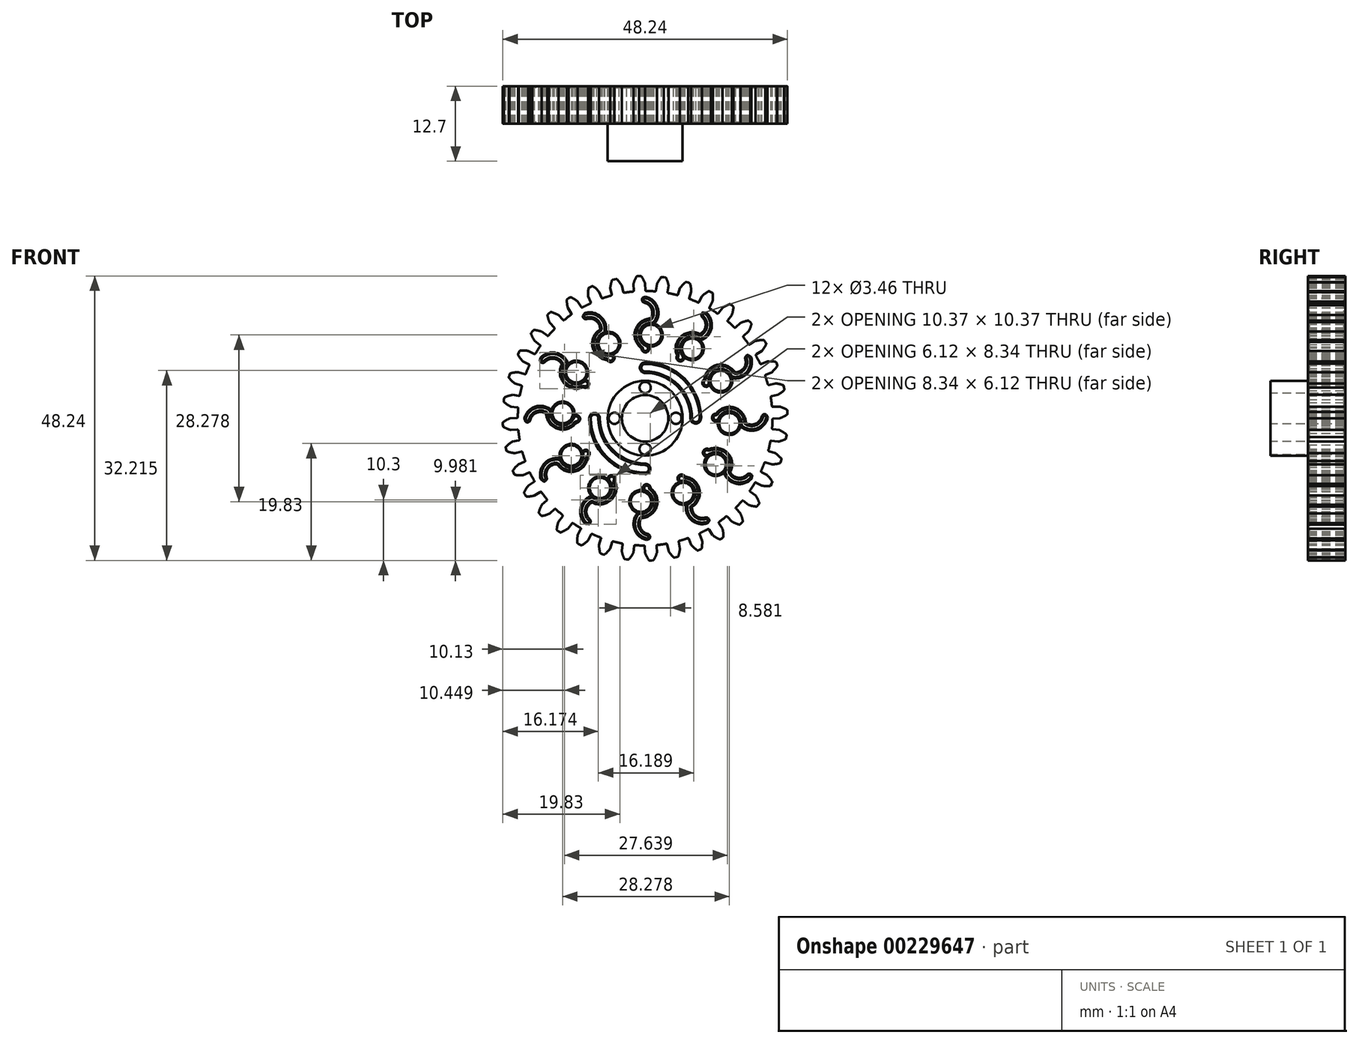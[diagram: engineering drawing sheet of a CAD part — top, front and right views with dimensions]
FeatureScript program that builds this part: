
annotation { "Feature Type Name" : "Feature", "Feature Type Description" : "" }
export const myFeature = defineFeature(function(context is Context, id is Id, definition is map)
    precondition{}
    {
        {
            var Q0;
            Q0=qCreatedBy(makeId("Front.planeOp"),FACE);
            var sketch = newSketch(context, id + "F0", { "sketchPlane" : qUnion([Q0])});
            skArc(sketch, "E0", {"start": v(-2.08, 21.49) * mm, "mid": v(-2.82, 21.4) * mm, "end": v(-3.55, 21.3) * mm});
            skArc(sketch, "E1.trimOffspring", {"start": v(0, 22.86) * mm, "mid": v(-0.28, 23.48) * mm, "end": v(-0.63, 24.05) * mm});
            skLineSegment(sketch, "E2", {"start": v(-0.76, 24.12) * mm, "end": v(-1.05, 24.12) * mm});
            skLineSegment(sketch, "E3", {"start": v(0, 22.86) * mm, "end": v(0.05, 21.73) * mm});
            skLineSegment(sketch, "E4.MirrorCS", {"start": v(-1.35, 24.1) * mm, "end": v(-1.05, 24.12) * mm});
            skArc(sketch, "E5.MirrorCS", {"start": v(-2, 22.77) * mm, "mid": v(-1.77, 23.41) * mm, "end": v(-1.47, 24.02) * mm});
            skLineSegment(sketch, "E6.MirrorCS", {"start": v(-2, 22.77) * mm, "end": v(-1.94, 21.65) * mm});
            skPoint(sketch, "E7.visualSharp", {"position": v(-1.94, 21.5) * mm});
            skArc(sketch, "E7.filletArc", {"start": v(-2.08, 21.49) * mm, "mid": v(-1.98, 21.54) * mm, "end": v(-1.94, 21.65) * mm});
            skPoint(sketch, "E8.visualSharp", {"position": v(0.06, 21.59) * mm});
            skArc(sketch, "E8.filletArc", {"start": v(0.05, 21.73) * mm, "mid": v(0.1, 21.63) * mm, "end": v(0.2, 21.59) * mm});
            skPoint(sketch, "E9.visualSharp", {"position": v(-0.68, 24.12) * mm});
            skArc(sketch, "E9.filletArc", {"start": v(-0.63, 24.05) * mm, "mid": v(-0.69, 24.1) * mm, "end": v(-0.76, 24.12) * mm});
            skPoint(sketch, "E10.visualSharp", {"position": v(-1.43, 24.09) * mm});
            skArc(sketch, "E10.filletArc", {"start": v(-1.35, 24.1) * mm, "mid": v(-1.42, 24.07) * mm, "end": v(-1.47, 24.02) * mm});
            skArc(sketch, "E11.1.0", {"start": v(-5.78, 20.8) * mm, "mid": v(-5.7, 20.87) * mm, "end": v(-5.67, 20.98) * mm});
            skArc(sketch, "E11.1.1", {"start": v(-3.73, 21.41) * mm, "mid": v(-3.66, 21.32) * mm, "end": v(-3.55, 21.3) * mm});
            skPoint(sketch, "E11.1.2", {"position": v(-4.85, 23.64) * mm});
            skLineSegment(sketch, "E11.1.3", {"start": v(-5.92, 22.08) * mm, "end": v(-5.67, 20.98) * mm});
            skArc(sketch, "E11.1.4", {"start": v(-5.92, 22.08) * mm, "mid": v(-5.8, 22.75) * mm, "end": v(-5.62, 23.4) * mm});
            skLineSegment(sketch, "E11.1.5", {"start": v(-5.51, 23.5) * mm, "end": v(-5.23, 23.57) * mm});
            skLineSegment(sketch, "E11.1.6", {"start": v(-3.97, 22.51) * mm, "end": v(-3.73, 21.41) * mm});
            skLineSegment(sketch, "E11.1.7", {"start": v(-4.93, 23.62) * mm, "end": v(-5.23, 23.57) * mm});
            skArc(sketch, "E11.1.8", {"start": v(-3.97, 22.51) * mm, "mid": v(-4.35, 23.07) * mm, "end": v(-4.8, 23.58) * mm});
            skPoint(sketch, "E11.1.9", {"position": v(-5.59, 23.47) * mm});
            skArc(sketch, "E11.1.10", {"start": v(-5.51, 23.5) * mm, "mid": v(-5.58, 23.46) * mm, "end": v(-5.62, 23.4) * mm});
            skArc(sketch, "E11.1.11", {"start": v(-4.8, 23.58) * mm, "mid": v(-4.86, 23.62) * mm, "end": v(-4.93, 23.62) * mm});
            skArc(sketch, "E11.2.0", {"start": v(-9.3, 19.48) * mm, "mid": v(-9.23, 19.56) * mm, "end": v(-9.23, 19.68) * mm});
            skArc(sketch, "E11.2.1", {"start": v(-7.39, 20.44) * mm, "mid": v(-7.3, 20.36) * mm, "end": v(-7.2, 20.36) * mm});
            skPoint(sketch, "E11.2.2", {"position": v(-8.89, 22.43) * mm});
            skLineSegment(sketch, "E11.2.3", {"start": v(-9.66, 20.72) * mm, "end": v(-9.23, 19.68) * mm});
            skArc(sketch, "E11.2.4", {"start": v(-9.66, 20.72) * mm, "mid": v(-9.67, 21.4) * mm, "end": v(-9.6, 22.07) * mm});
            skLineSegment(sketch, "E11.2.5", {"start": v(-9.5, 22.18) * mm, "end": v(-9.24, 22.3) * mm});
            skLineSegment(sketch, "E11.2.6", {"start": v(-7.82, 21.48) * mm, "end": v(-7.39, 20.44) * mm});
            skLineSegment(sketch, "E11.2.7", {"start": v(-8.96, 22.4) * mm, "end": v(-9.24, 22.3) * mm});
            skArc(sketch, "E11.2.8", {"start": v(-7.82, 21.48) * mm, "mid": v(-8.3, 21.96) * mm, "end": v(-8.82, 22.39) * mm});
            skPoint(sketch, "E11.2.9", {"position": v(-9.58, 22.15) * mm});
            skArc(sketch, "E11.2.10", {"start": v(-9.5, 22.18) * mm, "mid": v(-9.57, 22.13) * mm, "end": v(-9.6, 22.07) * mm});
            skArc(sketch, "E11.2.11", {"start": v(-8.82, 22.39) * mm, "mid": v(-8.89, 22.42) * mm, "end": v(-8.96, 22.4) * mm});
            skArc(sketch, "E11.3.0", {"start": v(-12.55, 17.57) * mm, "mid": v(-12.49, 17.66) * mm, "end": v(-12.5, 17.78) * mm});
            skArc(sketch, "E11.3.1", {"start": v(-10.82, 18.85) * mm, "mid": v(-10.73, 18.78) * mm, "end": v(-10.62, 18.8) * mm});
            skPoint(sketch, "E11.3.2", {"position": v(-12.65, 20.55) * mm});
            skLineSegment(sketch, "E11.3.3", {"start": v(-13.11, 18.73) * mm, "end": v(-12.5, 17.78) * mm});
            skArc(sketch, "E11.3.4", {"start": v(-13.11, 18.73) * mm, "mid": v(-13.24, 19.4) * mm, "end": v(-13.28, 20.07) * mm});
            skLineSegment(sketch, "E11.3.5", {"start": v(-13.22, 20.2) * mm, "end": v(-12.97, 20.36) * mm});
            skLineSegment(sketch, "E11.3.6", {"start": v(-11.43, 19.8) * mm, "end": v(-10.82, 18.85) * mm});
            skLineSegment(sketch, "E11.3.7", {"start": v(-12.71, 20.51) * mm, "end": v(-12.97, 20.36) * mm});
            skArc(sketch, "E11.3.8", {"start": v(-11.43, 19.8) * mm, "mid": v(-11.98, 20.2) * mm, "end": v(-12.57, 20.52) * mm});
            skPoint(sketch, "E11.3.9", {"position": v(-13.28, 20.15) * mm});
            skArc(sketch, "E11.3.10", {"start": v(-13.22, 20.2) * mm, "mid": v(-13.26, 20.14) * mm, "end": v(-13.28, 20.07) * mm});
            skArc(sketch, "E11.3.11", {"start": v(-12.57, 20.52) * mm, "mid": v(-12.64, 20.53) * mm, "end": v(-12.71, 20.51) * mm});
            skArc(sketch, "E11.4.0", {"start": v(-15.4, 15.12) * mm, "mid": v(-15.36, 15.23) * mm, "end": v(-15.4, 15.33) * mm});
            skArc(sketch, "E11.4.1", {"start": v(-13.93, 16.68) * mm, "mid": v(-13.83, 16.63) * mm, "end": v(-13.72, 16.67) * mm});
            skPoint(sketch, "E11.4.2", {"position": v(-16.02, 18.04) * mm});
            skLineSegment(sketch, "E11.4.3", {"start": v(-16.16, 16.16) * mm, "end": v(-15.4, 15.33) * mm});
            skArc(sketch, "E11.4.4", {"start": v(-16.16, 16.16) * mm, "mid": v(-16.4, 16.8) * mm, "end": v(-16.56, 17.46) * mm});
            skLineSegment(sketch, "E11.4.5", {"start": v(-16.52, 17.6) * mm, "end": v(-16.31, 17.8) * mm});
            skLineSegment(sketch, "E11.4.6", {"start": v(-14.7, 17.51) * mm, "end": v(-13.93, 16.68) * mm});
            skLineSegment(sketch, "E11.4.7", {"start": v(-16.08, 18) * mm, "end": v(-16.31, 17.8) * mm});
            skArc(sketch, "E11.4.8", {"start": v(-14.7, 17.51) * mm, "mid": v(-15.3, 17.8) * mm, "end": v(-15.95, 18.02) * mm});
            skPoint(sketch, "E11.4.9", {"position": v(-16.58, 17.53) * mm});
            skArc(sketch, "E11.4.10", {"start": v(-16.52, 17.6) * mm, "mid": v(-16.56, 17.53) * mm, "end": v(-16.56, 17.46) * mm});
            skArc(sketch, "E11.4.11", {"start": v(-15.95, 18.02) * mm, "mid": v(-16.02, 18.02) * mm, "end": v(-16.08, 18) * mm});
            skArc(sketch, "E11.5.0", {"start": v(-17.8, 12.22) * mm, "mid": v(-17.77, 12.33) * mm, "end": v(-17.83, 12.43) * mm});
            skArc(sketch, "E11.5.1", {"start": v(-16.62, 14) * mm, "mid": v(-16.5, 13.98) * mm, "end": v(-16.4, 14.03) * mm});
            skPoint(sketch, "E11.5.2", {"position": v(-18.91, 14.99) * mm});
            skLineSegment(sketch, "E11.5.3", {"start": v(-18.73, 13.11) * mm, "end": v(-17.83, 12.43) * mm});
            skArc(sketch, "E11.5.4", {"start": v(-18.73, 13.11) * mm, "mid": v(-19.07, 13.7) * mm, "end": v(-19.34, 14.31) * mm});
            skLineSegment(sketch, "E11.5.5", {"start": v(-19.32, 14.45) * mm, "end": v(-19.15, 14.7) * mm});
            skLineSegment(sketch, "E11.5.6", {"start": v(-17.51, 14.7) * mm, "end": v(-16.62, 14) * mm});
            skLineSegment(sketch, "E11.5.7", {"start": v(-18.96, 14.93) * mm, "end": v(-19.15, 14.7) * mm});
            skArc(sketch, "E11.5.8", {"start": v(-17.51, 14.7) * mm, "mid": v(-18.16, 14.88) * mm, "end": v(-18.83, 14.98) * mm});
            skPoint(sketch, "E11.5.9", {"position": v(-19.37, 14.39) * mm});
            skArc(sketch, "E11.5.10", {"start": v(-19.32, 14.45) * mm, "mid": v(-19.35, 14.39) * mm, "end": v(-19.34, 14.31) * mm});
            skArc(sketch, "E11.5.11", {"start": v(-18.83, 14.98) * mm, "mid": v(-18.9, 14.97) * mm, "end": v(-18.96, 14.93) * mm});
            skArc(sketch, "E11.6.0", {"start": v(-19.65, 8.94) * mm, "mid": v(-19.65, 9.06) * mm, "end": v(-19.72, 9.14) * mm});
            skArc(sketch, "E11.6.1", {"start": v(-18.8, 10.9) * mm, "mid": v(-18.69, 10.9) * mm, "end": v(-18.6, 10.97) * mm});
            skPoint(sketch, "E11.6.2", {"position": v(-21.23, 11.47) * mm});
            skLineSegment(sketch, "E11.6.3", {"start": v(-20.72, 9.66) * mm, "end": v(-19.72, 9.14) * mm});
            skArc(sketch, "E11.6.4", {"start": v(-20.72, 9.66) * mm, "mid": v(-21.16, 10.18) * mm, "end": v(-21.53, 10.74) * mm});
            skLineSegment(sketch, "E11.6.5", {"start": v(-21.54, 10.88) * mm, "end": v(-21.42, 11.15) * mm});
            skLineSegment(sketch, "E11.6.6", {"start": v(-19.8, 11.43) * mm, "end": v(-18.8, 10.9) * mm});
            skLineSegment(sketch, "E11.6.7", {"start": v(-21.27, 11.4) * mm, "end": v(-21.42, 11.15) * mm});
            skArc(sketch, "E11.6.8", {"start": v(-19.8, 11.43) * mm, "mid": v(-20.47, 11.5) * mm, "end": v(-21.15, 11.48) * mm});
            skPoint(sketch, "E11.6.9", {"position": v(-21.57, 10.8) * mm});
            skArc(sketch, "E11.6.10", {"start": v(-21.54, 10.88) * mm, "mid": v(-21.56, 10.8) * mm, "end": v(-21.53, 10.74) * mm});
            skArc(sketch, "E11.6.11", {"start": v(-21.15, 11.48) * mm, "mid": v(-21.22, 11.46) * mm, "end": v(-21.27, 11.4) * mm});
            skArc(sketch, "E11.7.0", {"start": v(-20.9, 5.4) * mm, "mid": v(-20.92, 5.5) * mm, "end": v(-21, 5.58) * mm});
            skArc(sketch, "E11.7.1", {"start": v(-20.4, 7.48) * mm, "mid": v(-20.3, 7.49) * mm, "end": v(-20.22, 7.57) * mm});
            skPoint(sketch, "E11.7.2", {"position": v(-22.9, 7.61) * mm});
            skLineSegment(sketch, "E11.7.3", {"start": v(-22.08, 5.92) * mm, "end": v(-21, 5.58) * mm});
            skArc(sketch, "E11.7.4", {"start": v(-22.08, 5.92) * mm, "mid": v(-22.6, 6.35) * mm, "end": v(-23.07, 6.83) * mm});
            skLineSegment(sketch, "E11.7.5", {"start": v(-23.1, 6.97) * mm, "end": v(-23.03, 7.26) * mm});
            skLineSegment(sketch, "E11.7.6", {"start": v(-21.48, 7.82) * mm, "end": v(-20.4, 7.48) * mm});
            skLineSegment(sketch, "E11.7.7", {"start": v(-22.92, 7.54) * mm, "end": v(-23.03, 7.26) * mm});
            skArc(sketch, "E11.7.8", {"start": v(-21.48, 7.82) * mm, "mid": v(-22.16, 7.77) * mm, "end": v(-22.82, 7.63) * mm});
            skPoint(sketch, "E11.7.9", {"position": v(-23.12, 6.9) * mm});
            skArc(sketch, "E11.7.10", {"start": v(-23.1, 6.97) * mm, "mid": v(-23.1, 6.9) * mm, "end": v(-23.07, 6.83) * mm});
            skArc(sketch, "E11.7.11", {"start": v(-22.82, 7.63) * mm, "mid": v(-22.88, 7.6) * mm, "end": v(-22.92, 7.54) * mm});
            skArc(sketch, "E11.8.0", {"start": v(-21.52, 1.68) * mm, "mid": v(-21.56, 1.8) * mm, "end": v(-21.66, 1.85) * mm});
            skArc(sketch, "E11.8.1", {"start": v(-21.4, 3.82) * mm, "mid": v(-21.29, 3.85) * mm, "end": v(-21.23, 3.95) * mm});
            skPoint(sketch, "E11.8.2", {"position": v(-23.87, 3.52) * mm});
            skLineSegment(sketch, "E11.8.3", {"start": v(-22.77, 2) * mm, "end": v(-21.66, 1.85) * mm});
            skArc(sketch, "E11.8.4", {"start": v(-22.77, 2) * mm, "mid": v(-23.36, 2.32) * mm, "end": v(-23.9, 2.72) * mm});
            skLineSegment(sketch, "E11.8.5", {"start": v(-23.96, 2.86) * mm, "end": v(-23.94, 3.15) * mm});
            skLineSegment(sketch, "E11.8.6", {"start": v(-22.51, 3.97) * mm, "end": v(-21.4, 3.82) * mm});
            skLineSegment(sketch, "E11.8.7", {"start": v(-23.89, 3.44) * mm, "end": v(-23.94, 3.15) * mm});
            skArc(sketch, "E11.8.8", {"start": v(-22.51, 3.97) * mm, "mid": v(-23.17, 3.8) * mm, "end": v(-23.8, 3.56) * mm});
            skPoint(sketch, "E11.8.9", {"position": v(-23.97, 2.78) * mm});
            skArc(sketch, "E11.8.10", {"start": v(-23.96, 2.86) * mm, "mid": v(-23.95, 2.78) * mm, "end": v(-23.9, 2.72) * mm});
            skArc(sketch, "E11.8.11", {"start": v(-23.8, 3.56) * mm, "mid": v(-23.86, 3.51) * mm, "end": v(-23.89, 3.44) * mm});
            skArc(sketch, "E11.9.0", {"start": v(-21.49, -2.08) * mm, "mid": v(-21.54, -1.98) * mm, "end": v(-21.65, -1.94) * mm});
            skArc(sketch, "E11.9.1", {"start": v(-21.73, 0.05) * mm, "mid": v(-21.63, 0.1) * mm, "end": v(-21.59, 0.2) * mm});
            skPoint(sketch, "E11.9.2", {"position": v(-24.12, -0.68) * mm});
            skLineSegment(sketch, "E11.9.3", {"start": v(-22.77, -2) * mm, "end": v(-21.65, -1.94) * mm});
            skArc(sketch, "E11.9.4", {"start": v(-22.77, -2) * mm, "mid": v(-23.41, -1.77) * mm, "end": v(-24.02, -1.47) * mm});
            skLineSegment(sketch, "E11.9.5", {"start": v(-24.1, -1.35) * mm, "end": v(-24.12, -1.05) * mm});
            skLineSegment(sketch, "E11.9.6", {"start": v(-22.86, 0) * mm, "end": v(-21.73, 0.05) * mm});
            skLineSegment(sketch, "E11.9.7", {"start": v(-24.12, -0.76) * mm, "end": v(-24.12, -1.05) * mm});
            skArc(sketch, "E11.9.8", {"start": v(-22.86, 0) * mm, "mid": v(-23.48, -0.28) * mm, "end": v(-24.05, -0.63) * mm});
            skPoint(sketch, "E11.9.9", {"position": v(-24.09, -1.43) * mm});
            skArc(sketch, "E11.9.10", {"start": v(-24.1, -1.35) * mm, "mid": v(-24.07, -1.42) * mm, "end": v(-24.02, -1.47) * mm});
            skArc(sketch, "E11.9.11", {"start": v(-24.05, -0.63) * mm, "mid": v(-24.1, -0.69) * mm, "end": v(-24.12, -0.76) * mm});
            skArc(sketch, "E11.10.0", {"start": v(-20.8, -5.78) * mm, "mid": v(-20.87, -5.7) * mm, "end": v(-20.98, -5.67) * mm});
            skArc(sketch, "E11.10.1", {"start": v(-21.41, -3.73) * mm, "mid": v(-21.32, -3.66) * mm, "end": v(-21.3, -3.55) * mm});
            skPoint(sketch, "E11.10.2", {"position": v(-23.64, -4.85) * mm});
            skLineSegment(sketch, "E11.10.3", {"start": v(-22.08, -5.92) * mm, "end": v(-20.98, -5.67) * mm});
            skArc(sketch, "E11.10.4", {"start": v(-22.08, -5.92) * mm, "mid": v(-22.75, -5.8) * mm, "end": v(-23.4, -5.62) * mm});
            skLineSegment(sketch, "E11.10.5", {"start": v(-23.5, -5.51) * mm, "end": v(-23.57, -5.23) * mm});
            skLineSegment(sketch, "E11.10.6", {"start": v(-22.51, -3.97) * mm, "end": v(-21.41, -3.73) * mm});
            skLineSegment(sketch, "E11.10.7", {"start": v(-23.62, -4.93) * mm, "end": v(-23.57, -5.23) * mm});
            skArc(sketch, "E11.10.8", {"start": v(-22.51, -3.97) * mm, "mid": v(-23.07, -4.35) * mm, "end": v(-23.58, -4.8) * mm});
            skPoint(sketch, "E11.10.9", {"position": v(-23.47, -5.59) * mm});
            skArc(sketch, "E11.10.10", {"start": v(-23.5, -5.51) * mm, "mid": v(-23.46, -5.58) * mm, "end": v(-23.4, -5.62) * mm});
            skArc(sketch, "E11.10.11", {"start": v(-23.58, -4.8) * mm, "mid": v(-23.62, -4.86) * mm, "end": v(-23.62, -4.93) * mm});
            skArc(sketch, "E11.11.0", {"start": v(-19.48, -9.3) * mm, "mid": v(-19.56, -9.23) * mm, "end": v(-19.68, -9.23) * mm});
            skArc(sketch, "E11.11.1", {"start": v(-20.44, -7.39) * mm, "mid": v(-20.36, -7.3) * mm, "end": v(-20.36, -7.2) * mm});
            skPoint(sketch, "E11.11.2", {"position": v(-22.43, -8.89) * mm});
            skLineSegment(sketch, "E11.11.3", {"start": v(-20.72, -9.66) * mm, "end": v(-19.68, -9.23) * mm});
            skArc(sketch, "E11.11.4", {"start": v(-20.72, -9.66) * mm, "mid": v(-21.4, -9.67) * mm, "end": v(-22.07, -9.6) * mm});
            skLineSegment(sketch, "E11.11.5", {"start": v(-22.18, -9.5) * mm, "end": v(-22.3, -9.24) * mm});
            skLineSegment(sketch, "E11.11.6", {"start": v(-21.48, -7.82) * mm, "end": v(-20.44, -7.39) * mm});
            skLineSegment(sketch, "E11.11.7", {"start": v(-22.4, -8.96) * mm, "end": v(-22.3, -9.24) * mm});
            skArc(sketch, "E11.11.8", {"start": v(-21.48, -7.82) * mm, "mid": v(-21.96, -8.3) * mm, "end": v(-22.39, -8.82) * mm});
            skPoint(sketch, "E11.11.9", {"position": v(-22.15, -9.58) * mm});
            skArc(sketch, "E11.11.10", {"start": v(-22.18, -9.5) * mm, "mid": v(-22.13, -9.57) * mm, "end": v(-22.07, -9.6) * mm});
            skArc(sketch, "E11.11.11", {"start": v(-22.39, -8.82) * mm, "mid": v(-22.42, -8.89) * mm, "end": v(-22.4, -8.96) * mm});
            skArc(sketch, "E11.12.0", {"start": v(-17.57, -12.55) * mm, "mid": v(-17.66, -12.49) * mm, "end": v(-17.78, -12.5) * mm});
            skArc(sketch, "E11.12.1", {"start": v(-18.85, -10.82) * mm, "mid": v(-18.78, -10.73) * mm, "end": v(-18.8, -10.62) * mm});
            skPoint(sketch, "E11.12.2", {"position": v(-20.55, -12.65) * mm});
            skLineSegment(sketch, "E11.12.3", {"start": v(-18.73, -13.11) * mm, "end": v(-17.78, -12.5) * mm});
            skArc(sketch, "E11.12.4", {"start": v(-18.73, -13.11) * mm, "mid": v(-19.4, -13.24) * mm, "end": v(-20.07, -13.28) * mm});
            skLineSegment(sketch, "E11.12.5", {"start": v(-20.2, -13.22) * mm, "end": v(-20.36, -12.97) * mm});
            skLineSegment(sketch, "E11.12.6", {"start": v(-19.8, -11.43) * mm, "end": v(-18.85, -10.82) * mm});
            skLineSegment(sketch, "E11.12.7", {"start": v(-20.51, -12.71) * mm, "end": v(-20.36, -12.97) * mm});
            skArc(sketch, "E11.12.8", {"start": v(-19.8, -11.43) * mm, "mid": v(-20.2, -11.98) * mm, "end": v(-20.52, -12.57) * mm});
            skPoint(sketch, "E11.12.9", {"position": v(-20.15, -13.28) * mm});
            skArc(sketch, "E11.12.10", {"start": v(-20.2, -13.22) * mm, "mid": v(-20.14, -13.26) * mm, "end": v(-20.07, -13.28) * mm});
            skArc(sketch, "E11.12.11", {"start": v(-20.52, -12.57) * mm, "mid": v(-20.53, -12.64) * mm, "end": v(-20.51, -12.71) * mm});
            skArc(sketch, "E11.13.0", {"start": v(-15.12, -15.4) * mm, "mid": v(-15.23, -15.36) * mm, "end": v(-15.33, -15.4) * mm});
            skArc(sketch, "E11.13.1", {"start": v(-16.68, -13.93) * mm, "mid": v(-16.63, -13.83) * mm, "end": v(-16.67, -13.72) * mm});
            skPoint(sketch, "E11.13.2", {"position": v(-18.04, -16.02) * mm});
            skLineSegment(sketch, "E11.13.3", {"start": v(-16.16, -16.16) * mm, "end": v(-15.33, -15.4) * mm});
            skArc(sketch, "E11.13.4", {"start": v(-16.16, -16.16) * mm, "mid": v(-16.8, -16.4) * mm, "end": v(-17.46, -16.56) * mm});
            skLineSegment(sketch, "E11.13.5", {"start": v(-17.6, -16.52) * mm, "end": v(-17.8, -16.31) * mm});
            skLineSegment(sketch, "E11.13.6", {"start": v(-17.51, -14.7) * mm, "end": v(-16.68, -13.93) * mm});
            skLineSegment(sketch, "E11.13.7", {"start": v(-18, -16.08) * mm, "end": v(-17.8, -16.31) * mm});
            skArc(sketch, "E11.13.8", {"start": v(-17.51, -14.7) * mm, "mid": v(-17.8, -15.3) * mm, "end": v(-18.02, -15.95) * mm});
            skPoint(sketch, "E11.13.9", {"position": v(-17.53, -16.58) * mm});
            skArc(sketch, "E11.13.10", {"start": v(-17.6, -16.52) * mm, "mid": v(-17.53, -16.56) * mm, "end": v(-17.46, -16.56) * mm});
            skArc(sketch, "E11.13.11", {"start": v(-18.02, -15.95) * mm, "mid": v(-18.02, -16.02) * mm, "end": v(-18, -16.08) * mm});
            skArc(sketch, "E11.14.0", {"start": v(-12.22, -17.8) * mm, "mid": v(-12.33, -17.77) * mm, "end": v(-12.43, -17.83) * mm});
            skArc(sketch, "E11.14.1", {"start": v(-14, -16.62) * mm, "mid": v(-13.98, -16.5) * mm, "end": v(-14.03, -16.4) * mm});
            skPoint(sketch, "E11.14.2", {"position": v(-14.99, -18.91) * mm});
            skLineSegment(sketch, "E11.14.3", {"start": v(-13.11, -18.73) * mm, "end": v(-12.43, -17.83) * mm});
            skArc(sketch, "E11.14.4", {"start": v(-13.11, -18.73) * mm, "mid": v(-13.7, -19.07) * mm, "end": v(-14.31, -19.34) * mm});
            skLineSegment(sketch, "E11.14.5", {"start": v(-14.45, -19.32) * mm, "end": v(-14.7, -19.15) * mm});
            skLineSegment(sketch, "E11.14.6", {"start": v(-14.7, -17.51) * mm, "end": v(-14, -16.62) * mm});
            skLineSegment(sketch, "E11.14.7", {"start": v(-14.93, -18.96) * mm, "end": v(-14.7, -19.15) * mm});
            skArc(sketch, "E11.14.8", {"start": v(-14.7, -17.51) * mm, "mid": v(-14.88, -18.16) * mm, "end": v(-14.98, -18.83) * mm});
            skPoint(sketch, "E11.14.9", {"position": v(-14.39, -19.37) * mm});
            skArc(sketch, "E11.14.10", {"start": v(-14.45, -19.32) * mm, "mid": v(-14.39, -19.35) * mm, "end": v(-14.31, -19.34) * mm});
            skArc(sketch, "E11.14.11", {"start": v(-14.98, -18.83) * mm, "mid": v(-14.97, -18.9) * mm, "end": v(-14.93, -18.96) * mm});
            skArc(sketch, "E11.15.0", {"start": v(-8.94, -19.65) * mm, "mid": v(-9.06, -19.65) * mm, "end": v(-9.14, -19.72) * mm});
            skArc(sketch, "E11.15.1", {"start": v(-10.9, -18.8) * mm, "mid": v(-10.9, -18.69) * mm, "end": v(-10.97, -18.6) * mm});
            skPoint(sketch, "E11.15.2", {"position": v(-11.47, -21.23) * mm});
            skLineSegment(sketch, "E11.15.3", {"start": v(-9.66, -20.72) * mm, "end": v(-9.14, -19.72) * mm});
            skArc(sketch, "E11.15.4", {"start": v(-9.66, -20.72) * mm, "mid": v(-10.18, -21.16) * mm, "end": v(-10.74, -21.53) * mm});
            skLineSegment(sketch, "E11.15.5", {"start": v(-10.88, -21.54) * mm, "end": v(-11.15, -21.42) * mm});
            skLineSegment(sketch, "E11.15.6", {"start": v(-11.43, -19.8) * mm, "end": v(-10.9, -18.8) * mm});
            skLineSegment(sketch, "E11.15.7", {"start": v(-11.4, -21.27) * mm, "end": v(-11.15, -21.42) * mm});
            skArc(sketch, "E11.15.8", {"start": v(-11.43, -19.8) * mm, "mid": v(-11.5, -20.47) * mm, "end": v(-11.48, -21.15) * mm});
            skPoint(sketch, "E11.15.9", {"position": v(-10.8, -21.57) * mm});
            skArc(sketch, "E11.15.10", {"start": v(-10.88, -21.54) * mm, "mid": v(-10.8, -21.56) * mm, "end": v(-10.74, -21.53) * mm});
            skArc(sketch, "E11.15.11", {"start": v(-11.48, -21.15) * mm, "mid": v(-11.46, -21.22) * mm, "end": v(-11.4, -21.27) * mm});
            skArc(sketch, "E11.16.0", {"start": v(-5.4, -20.9) * mm, "mid": v(-5.5, -20.92) * mm, "end": v(-5.58, -21) * mm});
            skArc(sketch, "E11.16.1", {"start": v(-7.48, -20.4) * mm, "mid": v(-7.49, -20.3) * mm, "end": v(-7.57, -20.22) * mm});
            skPoint(sketch, "E11.16.2", {"position": v(-7.61, -22.9) * mm});
            skLineSegment(sketch, "E11.16.3", {"start": v(-5.92, -22.08) * mm, "end": v(-5.58, -21) * mm});
            skArc(sketch, "E11.16.4", {"start": v(-5.92, -22.08) * mm, "mid": v(-6.35, -22.6) * mm, "end": v(-6.83, -23.07) * mm});
            skLineSegment(sketch, "E11.16.5", {"start": v(-6.97, -23.1) * mm, "end": v(-7.26, -23.03) * mm});
            skLineSegment(sketch, "E11.16.6", {"start": v(-7.82, -21.48) * mm, "end": v(-7.48, -20.4) * mm});
            skLineSegment(sketch, "E11.16.7", {"start": v(-7.54, -22.92) * mm, "end": v(-7.26, -23.03) * mm});
            skArc(sketch, "E11.16.8", {"start": v(-7.82, -21.48) * mm, "mid": v(-7.77, -22.16) * mm, "end": v(-7.63, -22.82) * mm});
            skPoint(sketch, "E11.16.9", {"position": v(-6.9, -23.12) * mm});
            skArc(sketch, "E11.16.10", {"start": v(-6.97, -23.1) * mm, "mid": v(-6.9, -23.1) * mm, "end": v(-6.83, -23.07) * mm});
            skArc(sketch, "E11.16.11", {"start": v(-7.63, -22.82) * mm, "mid": v(-7.6, -22.88) * mm, "end": v(-7.54, -22.92) * mm});
            skArc(sketch, "E11.17.0", {"start": v(-1.68, -21.52) * mm, "mid": v(-1.8, -21.56) * mm, "end": v(-1.85, -21.66) * mm});
            skArc(sketch, "E11.17.1", {"start": v(-3.82, -21.4) * mm, "mid": v(-3.85, -21.29) * mm, "end": v(-3.95, -21.23) * mm});
            skPoint(sketch, "E11.17.2", {"position": v(-3.52, -23.87) * mm});
            skLineSegment(sketch, "E11.17.3", {"start": v(-2, -22.77) * mm, "end": v(-1.85, -21.66) * mm});
            skArc(sketch, "E11.17.4", {"start": v(-2, -22.77) * mm, "mid": v(-2.32, -23.36) * mm, "end": v(-2.72, -23.9) * mm});
            skLineSegment(sketch, "E11.17.5", {"start": v(-2.86, -23.96) * mm, "end": v(-3.15, -23.94) * mm});
            skLineSegment(sketch, "E11.17.6", {"start": v(-3.97, -22.51) * mm, "end": v(-3.82, -21.4) * mm});
            skLineSegment(sketch, "E11.17.7", {"start": v(-3.44, -23.89) * mm, "end": v(-3.15, -23.94) * mm});
            skArc(sketch, "E11.17.8", {"start": v(-3.97, -22.51) * mm, "mid": v(-3.8, -23.17) * mm, "end": v(-3.56, -23.8) * mm});
            skPoint(sketch, "E11.17.9", {"position": v(-2.78, -23.97) * mm});
            skArc(sketch, "E11.17.10", {"start": v(-2.86, -23.96) * mm, "mid": v(-2.78, -23.95) * mm, "end": v(-2.72, -23.9) * mm});
            skArc(sketch, "E11.17.11", {"start": v(-3.56, -23.8) * mm, "mid": v(-3.51, -23.86) * mm, "end": v(-3.44, -23.89) * mm});
            skArc(sketch, "E11.18.0", {"start": v(2.08, -21.49) * mm, "mid": v(1.98, -21.54) * mm, "end": v(1.94, -21.65) * mm});
            skArc(sketch, "E11.18.1", {"start": v(-0.05, -21.73) * mm, "mid": v(-0.1, -21.63) * mm, "end": v(-0.2, -21.59) * mm});
            skPoint(sketch, "E11.18.2", {"position": v(0.68, -24.12) * mm});
            skLineSegment(sketch, "E11.18.3", {"start": v(2, -22.77) * mm, "end": v(1.94, -21.65) * mm});
            skArc(sketch, "E11.18.4", {"start": v(2, -22.77) * mm, "mid": v(1.77, -23.41) * mm, "end": v(1.47, -24.02) * mm});
            skLineSegment(sketch, "E11.18.5", {"start": v(1.35, -24.1) * mm, "end": v(1.05, -24.12) * mm});
            skLineSegment(sketch, "E11.18.6", {"start": v(0, -22.86) * mm, "end": v(-0.05, -21.73) * mm});
            skLineSegment(sketch, "E11.18.7", {"start": v(0.76, -24.12) * mm, "end": v(1.05, -24.12) * mm});
            skArc(sketch, "E11.18.8", {"start": v(0, -22.86) * mm, "mid": v(0.28, -23.48) * mm, "end": v(0.63, -24.05) * mm});
            skPoint(sketch, "E11.18.9", {"position": v(1.43, -24.09) * mm});
            skArc(sketch, "E11.18.10", {"start": v(1.35, -24.1) * mm, "mid": v(1.42, -24.07) * mm, "end": v(1.47, -24.02) * mm});
            skArc(sketch, "E11.18.11", {"start": v(0.63, -24.05) * mm, "mid": v(0.69, -24.1) * mm, "end": v(0.76, -24.12) * mm});
            skArc(sketch, "E11.19.0", {"start": v(5.78, -20.8) * mm, "mid": v(5.7, -20.87) * mm, "end": v(5.67, -20.98) * mm});
            skArc(sketch, "E11.19.1", {"start": v(3.73, -21.41) * mm, "mid": v(3.66, -21.32) * mm, "end": v(3.55, -21.3) * mm});
            skPoint(sketch, "E11.19.2", {"position": v(4.85, -23.64) * mm});
            skLineSegment(sketch, "E11.19.3", {"start": v(5.92, -22.08) * mm, "end": v(5.67, -20.98) * mm});
            skArc(sketch, "E11.19.4", {"start": v(5.92, -22.08) * mm, "mid": v(5.8, -22.75) * mm, "end": v(5.62, -23.4) * mm});
            skLineSegment(sketch, "E11.19.5", {"start": v(5.51, -23.5) * mm, "end": v(5.23, -23.57) * mm});
            skLineSegment(sketch, "E11.19.6", {"start": v(3.97, -22.51) * mm, "end": v(3.73, -21.41) * mm});
            skLineSegment(sketch, "E11.19.7", {"start": v(4.93, -23.62) * mm, "end": v(5.23, -23.57) * mm});
            skArc(sketch, "E11.19.8", {"start": v(3.97, -22.51) * mm, "mid": v(4.35, -23.07) * mm, "end": v(4.8, -23.58) * mm});
            skPoint(sketch, "E11.19.9", {"position": v(5.59, -23.47) * mm});
            skArc(sketch, "E11.19.10", {"start": v(5.51, -23.5) * mm, "mid": v(5.58, -23.46) * mm, "end": v(5.62, -23.4) * mm});
            skArc(sketch, "E11.19.11", {"start": v(4.8, -23.58) * mm, "mid": v(4.86, -23.62) * mm, "end": v(4.93, -23.62) * mm});
            skArc(sketch, "E11.20.0", {"start": v(9.3, -19.48) * mm, "mid": v(9.23, -19.56) * mm, "end": v(9.23, -19.68) * mm});
            skArc(sketch, "E11.20.1", {"start": v(7.39, -20.44) * mm, "mid": v(7.3, -20.36) * mm, "end": v(7.2, -20.36) * mm});
            skPoint(sketch, "E11.20.2", {"position": v(8.89, -22.43) * mm});
            skLineSegment(sketch, "E11.20.3", {"start": v(9.66, -20.72) * mm, "end": v(9.23, -19.68) * mm});
            skArc(sketch, "E11.20.4", {"start": v(9.66, -20.72) * mm, "mid": v(9.67, -21.4) * mm, "end": v(9.6, -22.07) * mm});
            skLineSegment(sketch, "E11.20.5", {"start": v(9.5, -22.18) * mm, "end": v(9.24, -22.3) * mm});
            skLineSegment(sketch, "E11.20.6", {"start": v(7.82, -21.48) * mm, "end": v(7.39, -20.44) * mm});
            skLineSegment(sketch, "E11.20.7", {"start": v(8.96, -22.4) * mm, "end": v(9.24, -22.3) * mm});
            skArc(sketch, "E11.20.8", {"start": v(7.82, -21.48) * mm, "mid": v(8.3, -21.96) * mm, "end": v(8.82, -22.39) * mm});
            skPoint(sketch, "E11.20.9", {"position": v(9.58, -22.15) * mm});
            skArc(sketch, "E11.20.10", {"start": v(9.5, -22.18) * mm, "mid": v(9.57, -22.13) * mm, "end": v(9.6, -22.07) * mm});
            skArc(sketch, "E11.20.11", {"start": v(8.82, -22.39) * mm, "mid": v(8.89, -22.42) * mm, "end": v(8.96, -22.4) * mm});
            skArc(sketch, "E11.21.0", {"start": v(12.55, -17.57) * mm, "mid": v(12.49, -17.66) * mm, "end": v(12.5, -17.78) * mm});
            skArc(sketch, "E11.21.1", {"start": v(10.82, -18.85) * mm, "mid": v(10.73, -18.78) * mm, "end": v(10.62, -18.8) * mm});
            skPoint(sketch, "E11.21.2", {"position": v(12.65, -20.55) * mm});
            skLineSegment(sketch, "E11.21.3", {"start": v(13.11, -18.73) * mm, "end": v(12.5, -17.78) * mm});
            skArc(sketch, "E11.21.4", {"start": v(13.11, -18.73) * mm, "mid": v(13.24, -19.4) * mm, "end": v(13.28, -20.07) * mm});
            skLineSegment(sketch, "E11.21.5", {"start": v(13.22, -20.2) * mm, "end": v(12.97, -20.36) * mm});
            skLineSegment(sketch, "E11.21.6", {"start": v(11.43, -19.8) * mm, "end": v(10.82, -18.85) * mm});
            skLineSegment(sketch, "E11.21.7", {"start": v(12.71, -20.51) * mm, "end": v(12.97, -20.36) * mm});
            skArc(sketch, "E11.21.8", {"start": v(11.43, -19.8) * mm, "mid": v(11.98, -20.2) * mm, "end": v(12.57, -20.52) * mm});
            skPoint(sketch, "E11.21.9", {"position": v(13.28, -20.15) * mm});
            skArc(sketch, "E11.21.10", {"start": v(13.22, -20.2) * mm, "mid": v(13.26, -20.14) * mm, "end": v(13.28, -20.07) * mm});
            skArc(sketch, "E11.21.11", {"start": v(12.57, -20.52) * mm, "mid": v(12.64, -20.53) * mm, "end": v(12.71, -20.51) * mm});
            skArc(sketch, "E11.22.0", {"start": v(15.4, -15.12) * mm, "mid": v(15.36, -15.23) * mm, "end": v(15.4, -15.33) * mm});
            skArc(sketch, "E11.22.1", {"start": v(13.93, -16.68) * mm, "mid": v(13.83, -16.63) * mm, "end": v(13.72, -16.67) * mm});
            skPoint(sketch, "E11.22.2", {"position": v(16.02, -18.04) * mm});
            skLineSegment(sketch, "E11.22.3", {"start": v(16.16, -16.16) * mm, "end": v(15.4, -15.33) * mm});
            skArc(sketch, "E11.22.4", {"start": v(16.16, -16.16) * mm, "mid": v(16.4, -16.8) * mm, "end": v(16.56, -17.46) * mm});
            skLineSegment(sketch, "E11.22.5", {"start": v(16.52, -17.6) * mm, "end": v(16.31, -17.8) * mm});
            skLineSegment(sketch, "E11.22.6", {"start": v(14.7, -17.51) * mm, "end": v(13.93, -16.68) * mm});
            skLineSegment(sketch, "E11.22.7", {"start": v(16.08, -18) * mm, "end": v(16.31, -17.8) * mm});
            skArc(sketch, "E11.22.8", {"start": v(14.7, -17.51) * mm, "mid": v(15.3, -17.8) * mm, "end": v(15.95, -18.02) * mm});
            skPoint(sketch, "E11.22.9", {"position": v(16.58, -17.53) * mm});
            skArc(sketch, "E11.22.10", {"start": v(16.52, -17.6) * mm, "mid": v(16.56, -17.53) * mm, "end": v(16.56, -17.46) * mm});
            skArc(sketch, "E11.22.11", {"start": v(15.95, -18.02) * mm, "mid": v(16.02, -18.02) * mm, "end": v(16.08, -18) * mm});
            skArc(sketch, "E11.23.0", {"start": v(17.8, -12.22) * mm, "mid": v(17.77, -12.33) * mm, "end": v(17.83, -12.43) * mm});
            skArc(sketch, "E11.23.1", {"start": v(16.62, -14) * mm, "mid": v(16.5, -13.98) * mm, "end": v(16.4, -14.03) * mm});
            skPoint(sketch, "E11.23.2", {"position": v(18.91, -14.99) * mm});
            skLineSegment(sketch, "E11.23.3", {"start": v(18.73, -13.11) * mm, "end": v(17.83, -12.43) * mm});
            skArc(sketch, "E11.23.4", {"start": v(18.73, -13.11) * mm, "mid": v(19.07, -13.7) * mm, "end": v(19.34, -14.31) * mm});
            skLineSegment(sketch, "E11.23.5", {"start": v(19.32, -14.45) * mm, "end": v(19.15, -14.7) * mm});
            skLineSegment(sketch, "E11.23.6", {"start": v(17.51, -14.7) * mm, "end": v(16.62, -14) * mm});
            skLineSegment(sketch, "E11.23.7", {"start": v(18.96, -14.93) * mm, "end": v(19.15, -14.7) * mm});
            skArc(sketch, "E11.23.8", {"start": v(17.51, -14.7) * mm, "mid": v(18.16, -14.88) * mm, "end": v(18.83, -14.98) * mm});
            skPoint(sketch, "E11.23.9", {"position": v(19.37, -14.39) * mm});
            skArc(sketch, "E11.23.10", {"start": v(19.32, -14.45) * mm, "mid": v(19.35, -14.39) * mm, "end": v(19.34, -14.31) * mm});
            skArc(sketch, "E11.23.11", {"start": v(18.83, -14.98) * mm, "mid": v(18.9, -14.97) * mm, "end": v(18.96, -14.93) * mm});
            skArc(sketch, "E11.24.0", {"start": v(19.65, -8.94) * mm, "mid": v(19.65, -9.06) * mm, "end": v(19.72, -9.14) * mm});
            skArc(sketch, "E11.24.1", {"start": v(18.8, -10.9) * mm, "mid": v(18.69, -10.9) * mm, "end": v(18.6, -10.97) * mm});
            skPoint(sketch, "E11.24.2", {"position": v(21.23, -11.47) * mm});
            skLineSegment(sketch, "E11.24.3", {"start": v(20.72, -9.66) * mm, "end": v(19.72, -9.14) * mm});
            skArc(sketch, "E11.24.4", {"start": v(20.72, -9.66) * mm, "mid": v(21.16, -10.18) * mm, "end": v(21.53, -10.74) * mm});
            skLineSegment(sketch, "E11.24.5", {"start": v(21.54, -10.88) * mm, "end": v(21.42, -11.15) * mm});
            skLineSegment(sketch, "E11.24.6", {"start": v(19.8, -11.43) * mm, "end": v(18.8, -10.9) * mm});
            skLineSegment(sketch, "E11.24.7", {"start": v(21.27, -11.4) * mm, "end": v(21.42, -11.15) * mm});
            skArc(sketch, "E11.24.8", {"start": v(19.8, -11.43) * mm, "mid": v(20.47, -11.5) * mm, "end": v(21.15, -11.48) * mm});
            skPoint(sketch, "E11.24.9", {"position": v(21.57, -10.8) * mm});
            skArc(sketch, "E11.24.10", {"start": v(21.54, -10.88) * mm, "mid": v(21.56, -10.8) * mm, "end": v(21.53, -10.74) * mm});
            skArc(sketch, "E11.24.11", {"start": v(21.15, -11.48) * mm, "mid": v(21.22, -11.46) * mm, "end": v(21.27, -11.4) * mm});
            skArc(sketch, "E11.25.0", {"start": v(20.9, -5.4) * mm, "mid": v(20.92, -5.5) * mm, "end": v(21, -5.58) * mm});
            skArc(sketch, "E11.25.1", {"start": v(20.4, -7.48) * mm, "mid": v(20.3, -7.49) * mm, "end": v(20.22, -7.57) * mm});
            skPoint(sketch, "E11.25.2", {"position": v(22.9, -7.61) * mm});
            skLineSegment(sketch, "E11.25.3", {"start": v(22.08, -5.92) * mm, "end": v(21, -5.58) * mm});
            skArc(sketch, "E11.25.4", {"start": v(22.08, -5.92) * mm, "mid": v(22.6, -6.35) * mm, "end": v(23.07, -6.83) * mm});
            skLineSegment(sketch, "E11.25.5", {"start": v(23.1, -6.97) * mm, "end": v(23.03, -7.26) * mm});
            skLineSegment(sketch, "E11.25.6", {"start": v(21.48, -7.82) * mm, "end": v(20.4, -7.48) * mm});
            skLineSegment(sketch, "E11.25.7", {"start": v(22.92, -7.54) * mm, "end": v(23.03, -7.26) * mm});
            skArc(sketch, "E11.25.8", {"start": v(21.48, -7.82) * mm, "mid": v(22.16, -7.77) * mm, "end": v(22.82, -7.63) * mm});
            skPoint(sketch, "E11.25.9", {"position": v(23.12, -6.9) * mm});
            skArc(sketch, "E11.25.10", {"start": v(23.1, -6.97) * mm, "mid": v(23.1, -6.9) * mm, "end": v(23.07, -6.83) * mm});
            skArc(sketch, "E11.25.11", {"start": v(22.82, -7.63) * mm, "mid": v(22.88, -7.6) * mm, "end": v(22.92, -7.54) * mm});
            skArc(sketch, "E11.26.0", {"start": v(21.52, -1.68) * mm, "mid": v(21.56, -1.8) * mm, "end": v(21.66, -1.85) * mm});
            skArc(sketch, "E11.26.1", {"start": v(21.4, -3.82) * mm, "mid": v(21.29, -3.85) * mm, "end": v(21.23, -3.95) * mm});
            skPoint(sketch, "E11.26.2", {"position": v(23.87, -3.52) * mm});
            skLineSegment(sketch, "E11.26.3", {"start": v(22.77, -2) * mm, "end": v(21.66, -1.85) * mm});
            skArc(sketch, "E11.26.4", {"start": v(22.77, -2) * mm, "mid": v(23.36, -2.32) * mm, "end": v(23.9, -2.72) * mm});
            skLineSegment(sketch, "E11.26.5", {"start": v(23.96, -2.86) * mm, "end": v(23.94, -3.15) * mm});
            skLineSegment(sketch, "E11.26.6", {"start": v(22.51, -3.97) * mm, "end": v(21.4, -3.82) * mm});
            skLineSegment(sketch, "E11.26.7", {"start": v(23.89, -3.44) * mm, "end": v(23.94, -3.15) * mm});
            skArc(sketch, "E11.26.8", {"start": v(22.51, -3.97) * mm, "mid": v(23.17, -3.8) * mm, "end": v(23.8, -3.56) * mm});
            skPoint(sketch, "E11.26.9", {"position": v(23.97, -2.78) * mm});
            skArc(sketch, "E11.26.10", {"start": v(23.96, -2.86) * mm, "mid": v(23.95, -2.78) * mm, "end": v(23.9, -2.72) * mm});
            skArc(sketch, "E11.26.11", {"start": v(23.8, -3.56) * mm, "mid": v(23.86, -3.51) * mm, "end": v(23.89, -3.44) * mm});
            skArc(sketch, "E11.27.0", {"start": v(21.49, 2.08) * mm, "mid": v(21.54, 1.98) * mm, "end": v(21.65, 1.94) * mm});
            skArc(sketch, "E11.27.1", {"start": v(21.73, -0.05) * mm, "mid": v(21.63, -0.1) * mm, "end": v(21.59, -0.2) * mm});
            skPoint(sketch, "E11.27.2", {"position": v(24.12, 0.68) * mm});
            skLineSegment(sketch, "E11.27.3", {"start": v(22.77, 2) * mm, "end": v(21.65, 1.94) * mm});
            skArc(sketch, "E11.27.4", {"start": v(22.77, 2) * mm, "mid": v(23.41, 1.77) * mm, "end": v(24.02, 1.47) * mm});
            skLineSegment(sketch, "E11.27.5", {"start": v(24.1, 1.35) * mm, "end": v(24.12, 1.05) * mm});
            skLineSegment(sketch, "E11.27.6", {"start": v(22.86, 0) * mm, "end": v(21.73, -0.05) * mm});
            skLineSegment(sketch, "E11.27.7", {"start": v(24.12, 0.76) * mm, "end": v(24.12, 1.05) * mm});
            skArc(sketch, "E11.27.8", {"start": v(22.86, 0) * mm, "mid": v(23.48, 0.28) * mm, "end": v(24.05, 0.63) * mm});
            skPoint(sketch, "E11.27.9", {"position": v(24.09, 1.43) * mm});
            skArc(sketch, "E11.27.10", {"start": v(24.1, 1.35) * mm, "mid": v(24.07, 1.42) * mm, "end": v(24.02, 1.47) * mm});
            skArc(sketch, "E11.27.11", {"start": v(24.05, 0.63) * mm, "mid": v(24.1, 0.69) * mm, "end": v(24.12, 0.76) * mm});
            skArc(sketch, "E11.28.0", {"start": v(20.8, 5.78) * mm, "mid": v(20.87, 5.7) * mm, "end": v(20.98, 5.67) * mm});
            skArc(sketch, "E11.28.1", {"start": v(21.41, 3.73) * mm, "mid": v(21.32, 3.66) * mm, "end": v(21.3, 3.55) * mm});
            skPoint(sketch, "E11.28.2", {"position": v(23.64, 4.85) * mm});
            skLineSegment(sketch, "E11.28.3", {"start": v(22.08, 5.92) * mm, "end": v(20.98, 5.67) * mm});
            skArc(sketch, "E11.28.4", {"start": v(22.08, 5.92) * mm, "mid": v(22.75, 5.8) * mm, "end": v(23.4, 5.62) * mm});
            skLineSegment(sketch, "E11.28.5", {"start": v(23.5, 5.51) * mm, "end": v(23.57, 5.23) * mm});
            skLineSegment(sketch, "E11.28.6", {"start": v(22.51, 3.97) * mm, "end": v(21.41, 3.73) * mm});
            skLineSegment(sketch, "E11.28.7", {"start": v(23.62, 4.93) * mm, "end": v(23.57, 5.23) * mm});
            skArc(sketch, "E11.28.8", {"start": v(22.51, 3.97) * mm, "mid": v(23.07, 4.35) * mm, "end": v(23.58, 4.8) * mm});
            skPoint(sketch, "E11.28.9", {"position": v(23.47, 5.59) * mm});
            skArc(sketch, "E11.28.10", {"start": v(23.5, 5.51) * mm, "mid": v(23.46, 5.58) * mm, "end": v(23.4, 5.62) * mm});
            skArc(sketch, "E11.28.11", {"start": v(23.58, 4.8) * mm, "mid": v(23.62, 4.86) * mm, "end": v(23.62, 4.93) * mm});
            skArc(sketch, "E11.29.0", {"start": v(19.48, 9.3) * mm, "mid": v(19.56, 9.23) * mm, "end": v(19.68, 9.23) * mm});
            skArc(sketch, "E11.29.1", {"start": v(20.44, 7.39) * mm, "mid": v(20.36, 7.3) * mm, "end": v(20.36, 7.2) * mm});
            skPoint(sketch, "E11.29.2", {"position": v(22.43, 8.89) * mm});
            skLineSegment(sketch, "E11.29.3", {"start": v(20.72, 9.66) * mm, "end": v(19.68, 9.23) * mm});
            skArc(sketch, "E11.29.4", {"start": v(20.72, 9.66) * mm, "mid": v(21.4, 9.67) * mm, "end": v(22.07, 9.6) * mm});
            skLineSegment(sketch, "E11.29.5", {"start": v(22.18, 9.5) * mm, "end": v(22.3, 9.24) * mm});
            skLineSegment(sketch, "E11.29.6", {"start": v(21.48, 7.82) * mm, "end": v(20.44, 7.39) * mm});
            skLineSegment(sketch, "E11.29.7", {"start": v(22.4, 8.96) * mm, "end": v(22.3, 9.24) * mm});
            skArc(sketch, "E11.29.8", {"start": v(21.48, 7.82) * mm, "mid": v(21.96, 8.3) * mm, "end": v(22.39, 8.82) * mm});
            skPoint(sketch, "E11.29.9", {"position": v(22.15, 9.58) * mm});
            skArc(sketch, "E11.29.10", {"start": v(22.18, 9.5) * mm, "mid": v(22.13, 9.57) * mm, "end": v(22.07, 9.6) * mm});
            skArc(sketch, "E11.29.11", {"start": v(22.39, 8.82) * mm, "mid": v(22.42, 8.89) * mm, "end": v(22.4, 8.96) * mm});
            skArc(sketch, "E11.30.0", {"start": v(17.57, 12.55) * mm, "mid": v(17.66, 12.49) * mm, "end": v(17.78, 12.5) * mm});
            skArc(sketch, "E11.30.1", {"start": v(18.85, 10.82) * mm, "mid": v(18.78, 10.73) * mm, "end": v(18.8, 10.62) * mm});
            skPoint(sketch, "E11.30.2", {"position": v(20.55, 12.65) * mm});
            skLineSegment(sketch, "E11.30.3", {"start": v(18.73, 13.11) * mm, "end": v(17.78, 12.5) * mm});
            skArc(sketch, "E11.30.4", {"start": v(18.73, 13.11) * mm, "mid": v(19.4, 13.24) * mm, "end": v(20.07, 13.28) * mm});
            skLineSegment(sketch, "E11.30.5", {"start": v(20.2, 13.22) * mm, "end": v(20.36, 12.97) * mm});
            skLineSegment(sketch, "E11.30.6", {"start": v(19.8, 11.43) * mm, "end": v(18.85, 10.82) * mm});
            skLineSegment(sketch, "E11.30.7", {"start": v(20.51, 12.71) * mm, "end": v(20.36, 12.97) * mm});
            skArc(sketch, "E11.30.8", {"start": v(19.8, 11.43) * mm, "mid": v(20.2, 11.98) * mm, "end": v(20.52, 12.57) * mm});
            skPoint(sketch, "E11.30.9", {"position": v(20.15, 13.28) * mm});
            skArc(sketch, "E11.30.10", {"start": v(20.2, 13.22) * mm, "mid": v(20.14, 13.26) * mm, "end": v(20.07, 13.28) * mm});
            skArc(sketch, "E11.30.11", {"start": v(20.52, 12.57) * mm, "mid": v(20.53, 12.64) * mm, "end": v(20.51, 12.71) * mm});
            skArc(sketch, "E11.31.0", {"start": v(15.12, 15.4) * mm, "mid": v(15.23, 15.36) * mm, "end": v(15.33, 15.4) * mm});
            skArc(sketch, "E11.31.1", {"start": v(16.68, 13.93) * mm, "mid": v(16.63, 13.83) * mm, "end": v(16.67, 13.72) * mm});
            skPoint(sketch, "E11.31.2", {"position": v(18.04, 16.02) * mm});
            skLineSegment(sketch, "E11.31.3", {"start": v(16.16, 16.16) * mm, "end": v(15.33, 15.4) * mm});
            skArc(sketch, "E11.31.4", {"start": v(16.16, 16.16) * mm, "mid": v(16.8, 16.4) * mm, "end": v(17.46, 16.56) * mm});
            skLineSegment(sketch, "E11.31.5", {"start": v(17.6, 16.52) * mm, "end": v(17.8, 16.31) * mm});
            skLineSegment(sketch, "E11.31.6", {"start": v(17.51, 14.7) * mm, "end": v(16.68, 13.93) * mm});
            skLineSegment(sketch, "E11.31.7", {"start": v(18, 16.08) * mm, "end": v(17.8, 16.31) * mm});
            skArc(sketch, "E11.31.8", {"start": v(17.51, 14.7) * mm, "mid": v(17.8, 15.3) * mm, "end": v(18.02, 15.95) * mm});
            skPoint(sketch, "E11.31.9", {"position": v(17.53, 16.58) * mm});
            skArc(sketch, "E11.31.10", {"start": v(17.6, 16.52) * mm, "mid": v(17.53, 16.56) * mm, "end": v(17.46, 16.56) * mm});
            skArc(sketch, "E11.31.11", {"start": v(18.02, 15.95) * mm, "mid": v(18.02, 16.02) * mm, "end": v(18, 16.08) * mm});
            skArc(sketch, "E11.32.0", {"start": v(12.22, 17.8) * mm, "mid": v(12.33, 17.77) * mm, "end": v(12.43, 17.83) * mm});
            skArc(sketch, "E11.32.1", {"start": v(14, 16.62) * mm, "mid": v(13.98, 16.5) * mm, "end": v(14.03, 16.4) * mm});
            skPoint(sketch, "E11.32.2", {"position": v(14.99, 18.91) * mm});
            skLineSegment(sketch, "E11.32.3", {"start": v(13.11, 18.73) * mm, "end": v(12.43, 17.83) * mm});
            skArc(sketch, "E11.32.4", {"start": v(13.11, 18.73) * mm, "mid": v(13.7, 19.07) * mm, "end": v(14.31, 19.34) * mm});
            skLineSegment(sketch, "E11.32.5", {"start": v(14.45, 19.32) * mm, "end": v(14.7, 19.15) * mm});
            skLineSegment(sketch, "E11.32.6", {"start": v(14.7, 17.51) * mm, "end": v(14, 16.62) * mm});
            skLineSegment(sketch, "E11.32.7", {"start": v(14.93, 18.96) * mm, "end": v(14.7, 19.15) * mm});
            skArc(sketch, "E11.32.8", {"start": v(14.7, 17.51) * mm, "mid": v(14.88, 18.16) * mm, "end": v(14.98, 18.83) * mm});
            skPoint(sketch, "E11.32.9", {"position": v(14.39, 19.37) * mm});
            skArc(sketch, "E11.32.10", {"start": v(14.45, 19.32) * mm, "mid": v(14.39, 19.35) * mm, "end": v(14.31, 19.34) * mm});
            skArc(sketch, "E11.32.11", {"start": v(14.98, 18.83) * mm, "mid": v(14.97, 18.9) * mm, "end": v(14.93, 18.96) * mm});
            skArc(sketch, "E11.33.0", {"start": v(8.94, 19.65) * mm, "mid": v(9.06, 19.65) * mm, "end": v(9.14, 19.72) * mm});
            skArc(sketch, "E11.33.1", {"start": v(10.9, 18.8) * mm, "mid": v(10.9, 18.69) * mm, "end": v(10.97, 18.6) * mm});
            skPoint(sketch, "E11.33.2", {"position": v(11.47, 21.23) * mm});
            skLineSegment(sketch, "E11.33.3", {"start": v(9.66, 20.72) * mm, "end": v(9.14, 19.72) * mm});
            skArc(sketch, "E11.33.4", {"start": v(9.66, 20.72) * mm, "mid": v(10.18, 21.16) * mm, "end": v(10.74, 21.53) * mm});
            skLineSegment(sketch, "E11.33.5", {"start": v(10.88, 21.54) * mm, "end": v(11.15, 21.42) * mm});
            skLineSegment(sketch, "E11.33.6", {"start": v(11.43, 19.8) * mm, "end": v(10.9, 18.8) * mm});
            skLineSegment(sketch, "E11.33.7", {"start": v(11.4, 21.27) * mm, "end": v(11.15, 21.42) * mm});
            skArc(sketch, "E11.33.8", {"start": v(11.43, 19.8) * mm, "mid": v(11.5, 20.47) * mm, "end": v(11.48, 21.15) * mm});
            skPoint(sketch, "E11.33.9", {"position": v(10.8, 21.57) * mm});
            skArc(sketch, "E11.33.10", {"start": v(10.88, 21.54) * mm, "mid": v(10.8, 21.56) * mm, "end": v(10.74, 21.53) * mm});
            skArc(sketch, "E11.33.11", {"start": v(11.48, 21.15) * mm, "mid": v(11.46, 21.22) * mm, "end": v(11.4, 21.27) * mm});
            skArc(sketch, "E11.34.0", {"start": v(5.4, 20.9) * mm, "mid": v(5.5, 20.92) * mm, "end": v(5.58, 21) * mm});
            skArc(sketch, "E11.34.1", {"start": v(7.48, 20.4) * mm, "mid": v(7.49, 20.3) * mm, "end": v(7.57, 20.22) * mm});
            skPoint(sketch, "E11.34.2", {"position": v(7.61, 22.9) * mm});
            skLineSegment(sketch, "E11.34.3", {"start": v(5.92, 22.08) * mm, "end": v(5.58, 21) * mm});
            skArc(sketch, "E11.34.4", {"start": v(5.92, 22.08) * mm, "mid": v(6.35, 22.6) * mm, "end": v(6.83, 23.07) * mm});
            skLineSegment(sketch, "E11.34.5", {"start": v(6.97, 23.1) * mm, "end": v(7.26, 23.03) * mm});
            skLineSegment(sketch, "E11.34.6", {"start": v(7.82, 21.48) * mm, "end": v(7.48, 20.4) * mm});
            skLineSegment(sketch, "E11.34.7", {"start": v(7.54, 22.92) * mm, "end": v(7.26, 23.03) * mm});
            skArc(sketch, "E11.34.8", {"start": v(7.82, 21.48) * mm, "mid": v(7.77, 22.16) * mm, "end": v(7.63, 22.82) * mm});
            skPoint(sketch, "E11.34.9", {"position": v(6.9, 23.12) * mm});
            skArc(sketch, "E11.34.10", {"start": v(6.97, 23.1) * mm, "mid": v(6.9, 23.1) * mm, "end": v(6.83, 23.07) * mm});
            skArc(sketch, "E11.34.11", {"start": v(7.63, 22.82) * mm, "mid": v(7.6, 22.88) * mm, "end": v(7.54, 22.92) * mm});
            skArc(sketch, "E11.35.0", {"start": v(1.68, 21.52) * mm, "mid": v(1.8, 21.56) * mm, "end": v(1.85, 21.66) * mm});
            skArc(sketch, "E11.35.1", {"start": v(3.82, 21.4) * mm, "mid": v(3.85, 21.29) * mm, "end": v(3.95, 21.23) * mm});
            skPoint(sketch, "E11.35.2", {"position": v(3.52, 23.87) * mm});
            skLineSegment(sketch, "E11.35.3", {"start": v(2, 22.77) * mm, "end": v(1.85, 21.66) * mm});
            skArc(sketch, "E11.35.4", {"start": v(2, 22.77) * mm, "mid": v(2.32, 23.36) * mm, "end": v(2.72, 23.9) * mm});
            skLineSegment(sketch, "E11.35.5", {"start": v(2.86, 23.96) * mm, "end": v(3.15, 23.94) * mm});
            skLineSegment(sketch, "E11.35.6", {"start": v(3.97, 22.51) * mm, "end": v(3.82, 21.4) * mm});
            skLineSegment(sketch, "E11.35.7", {"start": v(3.44, 23.89) * mm, "end": v(3.15, 23.94) * mm});
            skArc(sketch, "E11.35.8", {"start": v(3.97, 22.51) * mm, "mid": v(3.8, 23.17) * mm, "end": v(3.56, 23.8) * mm});
            skPoint(sketch, "E11.35.9", {"position": v(2.78, 23.97) * mm});
            skArc(sketch, "E11.35.10", {"start": v(2.86, 23.96) * mm, "mid": v(2.78, 23.95) * mm, "end": v(2.72, 23.9) * mm});
            skArc(sketch, "E11.35.11", {"start": v(3.56, 23.8) * mm, "mid": v(3.51, 23.86) * mm, "end": v(3.44, 23.89) * mm});
            skArc(sketch, "E12.trimOffspring", {"start": v(-5.78, 20.8) * mm, "mid": v(-6.5, 20.6) * mm, "end": v(-7.2, 20.36) * mm});
            skArc(sketch, "E13.trimOffspring", {"start": v(-9.3, 19.48) * mm, "mid": v(-9.97, 19.15) * mm, "end": v(-10.62, 18.8) * mm});
            skArc(sketch, "E14.trimOffspring", {"start": v(-12.55, 17.57) * mm, "mid": v(-13.14, 17.13) * mm, "end": v(-13.72, 16.67) * mm});
            skArc(sketch, "E15.trimOffspring", {"start": v(-15.4, 15.12) * mm, "mid": v(-15.92, 14.59) * mm, "end": v(-16.4, 14.03) * mm});
            skArc(sketch, "E16.trimOffspring", {"start": v(-17.8, 12.22) * mm, "mid": v(-18.2, 11.6) * mm, "end": v(-18.6, 10.97) * mm});
            skArc(sketch, "E17.trimOffspring", {"start": v(-19.65, 8.94) * mm, "mid": v(-19.95, 8.26) * mm, "end": v(-20.22, 7.57) * mm});
            skArc(sketch, "E18.trimOffspring", {"start": v(-20.9, 5.4) * mm, "mid": v(-21.08, 4.67) * mm, "end": v(-21.23, 3.95) * mm});
            skArc(sketch, "E19.trimOffspring", {"start": v(-21.52, 1.68) * mm, "mid": v(-21.57, 0.94) * mm, "end": v(-21.59, 0.2) * mm});
            skArc(sketch, "E20.trimOffspring", {"start": v(-21.49, -2.08) * mm, "mid": v(-21.4, -2.82) * mm, "end": v(-21.3, -3.55) * mm});
            skArc(sketch, "E21.trimOffspring", {"start": v(-20.8, -5.78) * mm, "mid": v(-20.6, -6.5) * mm, "end": v(-20.36, -7.2) * mm});
            skArc(sketch, "E22.trimOffspring", {"start": v(-19.48, -9.3) * mm, "mid": v(-19.15, -9.97) * mm, "end": v(-18.8, -10.62) * mm});
            skArc(sketch, "E23.trimOffspring", {"start": v(-17.57, -12.55) * mm, "mid": v(-17.13, -13.14) * mm, "end": v(-16.67, -13.72) * mm});
            skArc(sketch, "E24.trimOffspring", {"start": v(-15.12, -15.4) * mm, "mid": v(-14.59, -15.92) * mm, "end": v(-14.03, -16.4) * mm});
            skArc(sketch, "E25.trimOffspring", {"start": v(-12.22, -17.8) * mm, "mid": v(-11.6, -18.2) * mm, "end": v(-10.97, -18.6) * mm});
            skArc(sketch, "E26.trimOffspring", {"start": v(-8.94, -19.65) * mm, "mid": v(-8.26, -19.95) * mm, "end": v(-7.57, -20.22) * mm});
            skArc(sketch, "E27.trimOffspring", {"start": v(-5.4, -20.9) * mm, "mid": v(-4.67, -21.08) * mm, "end": v(-3.95, -21.23) * mm});
            skArc(sketch, "E28.trimOffspring", {"start": v(-1.68, -21.52) * mm, "mid": v(-0.94, -21.57) * mm, "end": v(-0.2, -21.59) * mm});
            skArc(sketch, "E29.trimOffspring", {"start": v(2.08, -21.49) * mm, "mid": v(2.82, -21.4) * mm, "end": v(3.55, -21.3) * mm});
            skArc(sketch, "E30.trimOffspring", {"start": v(5.78, -20.8) * mm, "mid": v(6.5, -20.6) * mm, "end": v(7.2, -20.36) * mm});
            skArc(sketch, "E31.trimOffspring", {"start": v(9.3, -19.48) * mm, "mid": v(9.97, -19.15) * mm, "end": v(10.62, -18.8) * mm});
            skArc(sketch, "E32.trimOffspring", {"start": v(12.55, -17.57) * mm, "mid": v(13.14, -17.13) * mm, "end": v(13.72, -16.67) * mm});
            skArc(sketch, "E33.trimOffspring", {"start": v(15.4, -15.12) * mm, "mid": v(15.92, -14.59) * mm, "end": v(16.4, -14.03) * mm});
            skArc(sketch, "E34.trimOffspring", {"start": v(17.8, -12.22) * mm, "mid": v(18.2, -11.6) * mm, "end": v(18.6, -10.97) * mm});
            skArc(sketch, "E35.trimOffspring", {"start": v(19.65, -8.94) * mm, "mid": v(19.95, -8.26) * mm, "end": v(20.22, -7.57) * mm});
            skArc(sketch, "E36.trimOffspring", {"start": v(20.9, -5.4) * mm, "mid": v(21.08, -4.67) * mm, "end": v(21.23, -3.95) * mm});
            skArc(sketch, "E37.trimOffspring", {"start": v(21.52, -1.68) * mm, "mid": v(21.57, -0.94) * mm, "end": v(21.59, -0.2) * mm});
            skArc(sketch, "E38.trimOffspring", {"start": v(21.49, 2.08) * mm, "mid": v(21.4, 2.82) * mm, "end": v(21.3, 3.55) * mm});
            skArc(sketch, "E39.trimOffspring", {"start": v(20.8, 5.78) * mm, "mid": v(20.6, 6.5) * mm, "end": v(20.36, 7.2) * mm});
            skArc(sketch, "E40.trimOffspring", {"start": v(19.48, 9.3) * mm, "mid": v(19.15, 9.97) * mm, "end": v(18.8, 10.62) * mm});
            skArc(sketch, "E41.trimOffspring", {"start": v(15.12, 15.4) * mm, "mid": v(14.59, 15.92) * mm, "end": v(14.03, 16.4) * mm});
            skArc(sketch, "E42.trimOffspring", {"start": v(17.57, 12.55) * mm, "mid": v(17.13, 13.14) * mm, "end": v(16.67, 13.72) * mm});
            skArc(sketch, "E43.trimOffspring", {"start": v(12.22, 17.8) * mm, "mid": v(11.6, 18.2) * mm, "end": v(10.97, 18.6) * mm});
            skArc(sketch, "E44.trimOffspring", {"start": v(8.94, 19.65) * mm, "mid": v(8.26, 19.95) * mm, "end": v(7.57, 20.22) * mm});
            skArc(sketch, "E45.trimOffspring", {"start": v(5.4, 20.9) * mm, "mid": v(4.67, 21.08) * mm, "end": v(3.95, 21.23) * mm});
            skArc(sketch, "E46.trimOffspring", {"start": v(1.68, 21.52) * mm, "mid": v(0.94, 21.57) * mm, "end": v(0.2, 21.59) * mm});
            skSolve(sketch);
        }
        {
            var Q0;
            Q0 = qSketchRegion(id + "F0", true);
            var Q1;
            Q1=makeQuery(id+"F0.imprint","IMPRINT",FACE,{"disambiguationData":[TD([[makeQuery(id+"F0.imprint","IMPRINT",EDGE,{"derivedFrom":sQuery(id+"F0.wireOp",EDGE,"E0")}),1.0]])]});
            extrude(context, id + "F1", {"entities" : qUnion([Q0, Q1]), "depth" : 6.35 * mm});
        }
        {
            var Q0;
            Q0=makeQuery(id+"F1.opExtrude","CAP_FACE",FACE,{"disambiguationData":[OSD([sQuery(id+"F0.wireOp",EDGE,"E0"),sQuery(id+"F0.wireOp",EDGE,"E1.trimOffspring"),sQuery(id+"F0.wireOp",EDGE,"E2"),sQuery(id+"F0.wireOp",EDGE,"E3"),sQuery(id+"F0.wireOp",EDGE,"E4.MirrorCS"),sQuery(id+"F0.wireOp",EDGE,"E5.MirrorCS"),sQuery(id+"F0.wireOp",EDGE,"E6.MirrorCS"),sQuery(id+"F0.wireOp",EDGE,"E7.filletArc"),sQuery(id+"F0.wireOp",EDGE,"E8.filletArc"),sQuery(id+"F0.wireOp",EDGE,"E9.filletArc"),sQuery(id+"F0.wireOp",EDGE,"E10.filletArc"),sQuery(id+"F0.wireOp",EDGE,"E11.1.0"),sQuery(id+"F0.wireOp",EDGE,"E11.1.1"),sQuery(id+"F0.wireOp",EDGE,"E11.1.3"),sQuery(id+"F0.wireOp",EDGE,"E11.1.4"),sQuery(id+"F0.wireOp",EDGE,"E11.1.5"),sQuery(id+"F0.wireOp",EDGE,"E11.1.6"),sQuery(id+"F0.wireOp",EDGE,"E11.1.7"),sQuery(id+"F0.wireOp",EDGE,"E11.1.8"),sQuery(id+"F0.wireOp",EDGE,"E11.1.10"),sQuery(id+"F0.wireOp",EDGE,"E11.1.11"),sQuery(id+"F0.wireOp",EDGE,"E11.2.0"),sQuery(id+"F0.wireOp",EDGE,"E11.2.1"),sQuery(id+"F0.wireOp",EDGE,"E11.2.3"),sQuery(id+"F0.wireOp",EDGE,"E11.2.4"),sQuery(id+"F0.wireOp",EDGE,"E11.2.5"),sQuery(id+"F0.wireOp",EDGE,"E11.2.6"),sQuery(id+"F0.wireOp",EDGE,"E11.2.7"),sQuery(id+"F0.wireOp",EDGE,"E11.2.8"),sQuery(id+"F0.wireOp",EDGE,"E11.2.10"),sQuery(id+"F0.wireOp",EDGE,"E11.2.11"),sQuery(id+"F0.wireOp",EDGE,"E11.3.0"),sQuery(id+"F0.wireOp",EDGE,"E11.3.1"),sQuery(id+"F0.wireOp",EDGE,"E11.3.3"),sQuery(id+"F0.wireOp",EDGE,"E11.3.4"),sQuery(id+"F0.wireOp",EDGE,"E11.3.5"),sQuery(id+"F0.wireOp",EDGE,"E11.3.6"),sQuery(id+"F0.wireOp",EDGE,"E11.3.7"),sQuery(id+"F0.wireOp",EDGE,"E11.3.8"),sQuery(id+"F0.wireOp",EDGE,"E11.3.10"),sQuery(id+"F0.wireOp",EDGE,"E11.3.11"),sQuery(id+"F0.wireOp",EDGE,"E11.4.0"),sQuery(id+"F0.wireOp",EDGE,"E11.4.1"),sQuery(id+"F0.wireOp",EDGE,"E11.4.3"),sQuery(id+"F0.wireOp",EDGE,"E11.4.4"),sQuery(id+"F0.wireOp",EDGE,"E11.4.5"),sQuery(id+"F0.wireOp",EDGE,"E11.4.6"),sQuery(id+"F0.wireOp",EDGE,"E11.4.7"),sQuery(id+"F0.wireOp",EDGE,"E11.4.8"),sQuery(id+"F0.wireOp",EDGE,"E11.4.10"),sQuery(id+"F0.wireOp",EDGE,"E11.4.11"),sQuery(id+"F0.wireOp",EDGE,"E11.5.0"),sQuery(id+"F0.wireOp",EDGE,"E11.5.1"),sQuery(id+"F0.wireOp",EDGE,"E11.5.3"),sQuery(id+"F0.wireOp",EDGE,"E11.5.4"),sQuery(id+"F0.wireOp",EDGE,"E11.5.5"),sQuery(id+"F0.wireOp",EDGE,"E11.5.6"),sQuery(id+"F0.wireOp",EDGE,"E11.5.7"),sQuery(id+"F0.wireOp",EDGE,"E11.5.8"),sQuery(id+"F0.wireOp",EDGE,"E11.5.10"),sQuery(id+"F0.wireOp",EDGE,"E11.5.11"),sQuery(id+"F0.wireOp",EDGE,"E11.6.0"),sQuery(id+"F0.wireOp",EDGE,"E11.6.1"),sQuery(id+"F0.wireOp",EDGE,"E11.6.3"),sQuery(id+"F0.wireOp",EDGE,"E11.6.4"),sQuery(id+"F0.wireOp",EDGE,"E11.6.5"),sQuery(id+"F0.wireOp",EDGE,"E11.6.6"),sQuery(id+"F0.wireOp",EDGE,"E11.6.7"),sQuery(id+"F0.wireOp",EDGE,"E11.6.8"),sQuery(id+"F0.wireOp",EDGE,"E11.6.10"),sQuery(id+"F0.wireOp",EDGE,"E11.6.11"),sQuery(id+"F0.wireOp",EDGE,"E11.7.0"),sQuery(id+"F0.wireOp",EDGE,"E11.7.1"),sQuery(id+"F0.wireOp",EDGE,"E11.7.3"),sQuery(id+"F0.wireOp",EDGE,"E11.7.4"),sQuery(id+"F0.wireOp",EDGE,"E11.7.5"),sQuery(id+"F0.wireOp",EDGE,"E11.7.6"),sQuery(id+"F0.wireOp",EDGE,"E11.7.7"),sQuery(id+"F0.wireOp",EDGE,"E11.7.8"),sQuery(id+"F0.wireOp",EDGE,"E11.7.10"),sQuery(id+"F0.wireOp",EDGE,"E11.7.11"),sQuery(id+"F0.wireOp",EDGE,"E11.8.0"),sQuery(id+"F0.wireOp",EDGE,"E11.8.1"),sQuery(id+"F0.wireOp",EDGE,"E11.8.3"),sQuery(id+"F0.wireOp",EDGE,"E11.8.4"),sQuery(id+"F0.wireOp",EDGE,"E11.8.5"),sQuery(id+"F0.wireOp",EDGE,"E11.8.6"),sQuery(id+"F0.wireOp",EDGE,"E11.8.7"),sQuery(id+"F0.wireOp",EDGE,"E11.8.8"),sQuery(id+"F0.wireOp",EDGE,"E11.8.10"),sQuery(id+"F0.wireOp",EDGE,"E11.8.11"),sQuery(id+"F0.wireOp",EDGE,"E11.9.0"),sQuery(id+"F0.wireOp",EDGE,"E11.9.1"),sQuery(id+"F0.wireOp",EDGE,"E11.9.3"),sQuery(id+"F0.wireOp",EDGE,"E11.9.4"),sQuery(id+"F0.wireOp",EDGE,"E11.9.5"),sQuery(id+"F0.wireOp",EDGE,"E11.9.6"),sQuery(id+"F0.wireOp",EDGE,"E11.9.7"),sQuery(id+"F0.wireOp",EDGE,"E11.9.8"),sQuery(id+"F0.wireOp",EDGE,"E11.9.10"),sQuery(id+"F0.wireOp",EDGE,"E11.9.11"),sQuery(id+"F0.wireOp",EDGE,"E11.10.0"),sQuery(id+"F0.wireOp",EDGE,"E11.10.1"),sQuery(id+"F0.wireOp",EDGE,"E11.10.3"),sQuery(id+"F0.wireOp",EDGE,"E11.10.4"),sQuery(id+"F0.wireOp",EDGE,"E11.10.5"),sQuery(id+"F0.wireOp",EDGE,"E11.10.6"),sQuery(id+"F0.wireOp",EDGE,"E11.10.7"),sQuery(id+"F0.wireOp",EDGE,"E11.10.8"),sQuery(id+"F0.wireOp",EDGE,"E11.10.10"),sQuery(id+"F0.wireOp",EDGE,"E11.10.11"),sQuery(id+"F0.wireOp",EDGE,"E11.11.0"),sQuery(id+"F0.wireOp",EDGE,"E11.11.1"),sQuery(id+"F0.wireOp",EDGE,"E11.11.3"),sQuery(id+"F0.wireOp",EDGE,"E11.11.4"),sQuery(id+"F0.wireOp",EDGE,"E11.11.5"),sQuery(id+"F0.wireOp",EDGE,"E11.11.6"),sQuery(id+"F0.wireOp",EDGE,"E11.11.7"),sQuery(id+"F0.wireOp",EDGE,"E11.11.8"),sQuery(id+"F0.wireOp",EDGE,"E11.11.10"),sQuery(id+"F0.wireOp",EDGE,"E11.11.11"),sQuery(id+"F0.wireOp",EDGE,"E11.12.0"),sQuery(id+"F0.wireOp",EDGE,"E11.12.1"),sQuery(id+"F0.wireOp",EDGE,"E11.12.3"),sQuery(id+"F0.wireOp",EDGE,"E11.12.4"),sQuery(id+"F0.wireOp",EDGE,"E11.12.5"),sQuery(id+"F0.wireOp",EDGE,"E11.12.6"),sQuery(id+"F0.wireOp",EDGE,"E11.12.7"),sQuery(id+"F0.wireOp",EDGE,"E11.12.8"),sQuery(id+"F0.wireOp",EDGE,"E11.12.10"),sQuery(id+"F0.wireOp",EDGE,"E11.12.11"),sQuery(id+"F0.wireOp",EDGE,"E11.13.0"),sQuery(id+"F0.wireOp",EDGE,"E11.13.1"),sQuery(id+"F0.wireOp",EDGE,"E11.13.3"),sQuery(id+"F0.wireOp",EDGE,"E11.13.4"),sQuery(id+"F0.wireOp",EDGE,"E11.13.5"),sQuery(id+"F0.wireOp",EDGE,"E11.13.6"),sQuery(id+"F0.wireOp",EDGE,"E11.13.7"),sQuery(id+"F0.wireOp",EDGE,"E11.13.8"),sQuery(id+"F0.wireOp",EDGE,"E11.13.10"),sQuery(id+"F0.wireOp",EDGE,"E11.13.11"),sQuery(id+"F0.wireOp",EDGE,"E11.14.0"),sQuery(id+"F0.wireOp",EDGE,"E11.14.1"),sQuery(id+"F0.wireOp",EDGE,"E11.14.3"),sQuery(id+"F0.wireOp",EDGE,"E11.14.4"),sQuery(id+"F0.wireOp",EDGE,"E11.14.5"),sQuery(id+"F0.wireOp",EDGE,"E11.14.6"),sQuery(id+"F0.wireOp",EDGE,"E11.14.7"),sQuery(id+"F0.wireOp",EDGE,"E11.14.8"),sQuery(id+"F0.wireOp",EDGE,"E11.14.10"),sQuery(id+"F0.wireOp",EDGE,"E11.14.11"),sQuery(id+"F0.wireOp",EDGE,"E11.15.0"),sQuery(id+"F0.wireOp",EDGE,"E11.15.1"),sQuery(id+"F0.wireOp",EDGE,"E11.15.3"),sQuery(id+"F0.wireOp",EDGE,"E11.15.4"),sQuery(id+"F0.wireOp",EDGE,"E11.15.5"),sQuery(id+"F0.wireOp",EDGE,"E11.15.6"),sQuery(id+"F0.wireOp",EDGE,"E11.15.7"),sQuery(id+"F0.wireOp",EDGE,"E11.15.8"),sQuery(id+"F0.wireOp",EDGE,"E11.15.10"),sQuery(id+"F0.wireOp",EDGE,"E11.15.11"),sQuery(id+"F0.wireOp",EDGE,"E11.16.0"),sQuery(id+"F0.wireOp",EDGE,"E11.16.1"),sQuery(id+"F0.wireOp",EDGE,"E11.16.3"),sQuery(id+"F0.wireOp",EDGE,"E11.16.4"),sQuery(id+"F0.wireOp",EDGE,"E11.16.5"),sQuery(id+"F0.wireOp",EDGE,"E11.16.6"),sQuery(id+"F0.wireOp",EDGE,"E11.16.7"),sQuery(id+"F0.wireOp",EDGE,"E11.16.8"),sQuery(id+"F0.wireOp",EDGE,"E11.16.10"),sQuery(id+"F0.wireOp",EDGE,"E11.16.11"),sQuery(id+"F0.wireOp",EDGE,"E11.17.0"),sQuery(id+"F0.wireOp",EDGE,"E11.17.1"),sQuery(id+"F0.wireOp",EDGE,"E11.17.3"),sQuery(id+"F0.wireOp",EDGE,"E11.17.4"),sQuery(id+"F0.wireOp",EDGE,"E11.17.5"),sQuery(id+"F0.wireOp",EDGE,"E11.17.6"),sQuery(id+"F0.wireOp",EDGE,"E11.17.7"),sQuery(id+"F0.wireOp",EDGE,"E11.17.8"),sQuery(id+"F0.wireOp",EDGE,"E11.17.10"),sQuery(id+"F0.wireOp",EDGE,"E11.17.11"),sQuery(id+"F0.wireOp",EDGE,"E11.18.0"),sQuery(id+"F0.wireOp",EDGE,"E11.18.1"),sQuery(id+"F0.wireOp",EDGE,"E11.18.3"),sQuery(id+"F0.wireOp",EDGE,"E11.18.4"),sQuery(id+"F0.wireOp",EDGE,"E11.18.5"),sQuery(id+"F0.wireOp",EDGE,"E11.18.6"),sQuery(id+"F0.wireOp",EDGE,"E11.18.7"),sQuery(id+"F0.wireOp",EDGE,"E11.18.8"),sQuery(id+"F0.wireOp",EDGE,"E11.18.10"),sQuery(id+"F0.wireOp",EDGE,"E11.18.11"),sQuery(id+"F0.wireOp",EDGE,"E11.19.0"),sQuery(id+"F0.wireOp",EDGE,"E11.19.1"),sQuery(id+"F0.wireOp",EDGE,"E11.19.3"),sQuery(id+"F0.wireOp",EDGE,"E11.19.4"),sQuery(id+"F0.wireOp",EDGE,"E11.19.5"),sQuery(id+"F0.wireOp",EDGE,"E11.19.6"),sQuery(id+"F0.wireOp",EDGE,"E11.19.7"),sQuery(id+"F0.wireOp",EDGE,"E11.19.8"),sQuery(id+"F0.wireOp",EDGE,"E11.19.10"),sQuery(id+"F0.wireOp",EDGE,"E11.19.11"),sQuery(id+"F0.wireOp",EDGE,"E11.20.0"),sQuery(id+"F0.wireOp",EDGE,"E11.20.1"),sQuery(id+"F0.wireOp",EDGE,"E11.20.3"),sQuery(id+"F0.wireOp",EDGE,"E11.20.4"),sQuery(id+"F0.wireOp",EDGE,"E11.20.5"),sQuery(id+"F0.wireOp",EDGE,"E11.20.6"),sQuery(id+"F0.wireOp",EDGE,"E11.20.7"),sQuery(id+"F0.wireOp",EDGE,"E11.20.8"),sQuery(id+"F0.wireOp",EDGE,"E11.20.10"),sQuery(id+"F0.wireOp",EDGE,"E11.20.11"),sQuery(id+"F0.wireOp",EDGE,"E11.21.0"),sQuery(id+"F0.wireOp",EDGE,"E11.21.1"),sQuery(id+"F0.wireOp",EDGE,"E11.21.3"),sQuery(id+"F0.wireOp",EDGE,"E11.21.4"),sQuery(id+"F0.wireOp",EDGE,"E11.21.5"),sQuery(id+"F0.wireOp",EDGE,"E11.21.6"),sQuery(id+"F0.wireOp",EDGE,"E11.21.7"),sQuery(id+"F0.wireOp",EDGE,"E11.21.8"),sQuery(id+"F0.wireOp",EDGE,"E11.21.10"),sQuery(id+"F0.wireOp",EDGE,"E11.21.11"),sQuery(id+"F0.wireOp",EDGE,"E11.22.0"),sQuery(id+"F0.wireOp",EDGE,"E11.22.1"),sQuery(id+"F0.wireOp",EDGE,"E11.22.3"),sQuery(id+"F0.wireOp",EDGE,"E11.22.4"),sQuery(id+"F0.wireOp",EDGE,"E11.22.5"),sQuery(id+"F0.wireOp",EDGE,"E11.22.6"),sQuery(id+"F0.wireOp",EDGE,"E11.22.7"),sQuery(id+"F0.wireOp",EDGE,"E11.22.8"),sQuery(id+"F0.wireOp",EDGE,"E11.22.10"),sQuery(id+"F0.wireOp",EDGE,"E11.22.11"),sQuery(id+"F0.wireOp",EDGE,"E11.23.0"),sQuery(id+"F0.wireOp",EDGE,"E11.23.1"),sQuery(id+"F0.wireOp",EDGE,"E11.23.3"),sQuery(id+"F0.wireOp",EDGE,"E11.23.4"),sQuery(id+"F0.wireOp",EDGE,"E11.23.5"),sQuery(id+"F0.wireOp",EDGE,"E11.23.6"),sQuery(id+"F0.wireOp",EDGE,"E11.23.7"),sQuery(id+"F0.wireOp",EDGE,"E11.23.8"),sQuery(id+"F0.wireOp",EDGE,"E11.23.10"),sQuery(id+"F0.wireOp",EDGE,"E11.23.11"),sQuery(id+"F0.wireOp",EDGE,"E11.24.0"),sQuery(id+"F0.wireOp",EDGE,"E11.24.1"),sQuery(id+"F0.wireOp",EDGE,"E11.24.3"),sQuery(id+"F0.wireOp",EDGE,"E11.24.4"),sQuery(id+"F0.wireOp",EDGE,"E11.24.5"),sQuery(id+"F0.wireOp",EDGE,"E11.24.6"),sQuery(id+"F0.wireOp",EDGE,"E11.24.7"),sQuery(id+"F0.wireOp",EDGE,"E11.24.8"),sQuery(id+"F0.wireOp",EDGE,"E11.24.10"),sQuery(id+"F0.wireOp",EDGE,"E11.24.11"),sQuery(id+"F0.wireOp",EDGE,"E11.25.0"),sQuery(id+"F0.wireOp",EDGE,"E11.25.1"),sQuery(id+"F0.wireOp",EDGE,"E11.25.3"),sQuery(id+"F0.wireOp",EDGE,"E11.25.4"),sQuery(id+"F0.wireOp",EDGE,"E11.25.5"),sQuery(id+"F0.wireOp",EDGE,"E11.25.6"),sQuery(id+"F0.wireOp",EDGE,"E11.25.7"),sQuery(id+"F0.wireOp",EDGE,"E11.25.8"),sQuery(id+"F0.wireOp",EDGE,"E11.25.10"),sQuery(id+"F0.wireOp",EDGE,"E11.25.11"),sQuery(id+"F0.wireOp",EDGE,"E11.26.0"),sQuery(id+"F0.wireOp",EDGE,"E11.26.1"),sQuery(id+"F0.wireOp",EDGE,"E11.26.3"),sQuery(id+"F0.wireOp",EDGE,"E11.26.4"),sQuery(id+"F0.wireOp",EDGE,"E11.26.5"),sQuery(id+"F0.wireOp",EDGE,"E11.26.6"),sQuery(id+"F0.wireOp",EDGE,"E11.26.7"),sQuery(id+"F0.wireOp",EDGE,"E11.26.8"),sQuery(id+"F0.wireOp",EDGE,"E11.26.10"),sQuery(id+"F0.wireOp",EDGE,"E11.26.11"),sQuery(id+"F0.wireOp",EDGE,"E11.27.0"),sQuery(id+"F0.wireOp",EDGE,"E11.27.1"),sQuery(id+"F0.wireOp",EDGE,"E11.27.3"),sQuery(id+"F0.wireOp",EDGE,"E11.27.4"),sQuery(id+"F0.wireOp",EDGE,"E11.27.5"),sQuery(id+"F0.wireOp",EDGE,"E11.27.6"),sQuery(id+"F0.wireOp",EDGE,"E11.27.7"),sQuery(id+"F0.wireOp",EDGE,"E11.27.8"),sQuery(id+"F0.wireOp",EDGE,"E11.27.10"),sQuery(id+"F0.wireOp",EDGE,"E11.27.11"),sQuery(id+"F0.wireOp",EDGE,"E11.28.0"),sQuery(id+"F0.wireOp",EDGE,"E11.28.1"),sQuery(id+"F0.wireOp",EDGE,"E11.28.3"),sQuery(id+"F0.wireOp",EDGE,"E11.28.4"),sQuery(id+"F0.wireOp",EDGE,"E11.28.5"),sQuery(id+"F0.wireOp",EDGE,"E11.28.6"),sQuery(id+"F0.wireOp",EDGE,"E11.28.7"),sQuery(id+"F0.wireOp",EDGE,"E11.28.8"),sQuery(id+"F0.wireOp",EDGE,"E11.28.10"),sQuery(id+"F0.wireOp",EDGE,"E11.28.11"),sQuery(id+"F0.wireOp",EDGE,"E11.29.0"),sQuery(id+"F0.wireOp",EDGE,"E11.29.1"),sQuery(id+"F0.wireOp",EDGE,"E11.29.3"),sQuery(id+"F0.wireOp",EDGE,"E11.29.4"),sQuery(id+"F0.wireOp",EDGE,"E11.29.5"),sQuery(id+"F0.wireOp",EDGE,"E11.29.6"),sQuery(id+"F0.wireOp",EDGE,"E11.29.7"),sQuery(id+"F0.wireOp",EDGE,"E11.29.8"),sQuery(id+"F0.wireOp",EDGE,"E11.29.10"),sQuery(id+"F0.wireOp",EDGE,"E11.29.11"),sQuery(id+"F0.wireOp",EDGE,"E11.30.0"),sQuery(id+"F0.wireOp",EDGE,"E11.30.1"),sQuery(id+"F0.wireOp",EDGE,"E11.30.3"),sQuery(id+"F0.wireOp",EDGE,"E11.30.4"),sQuery(id+"F0.wireOp",EDGE,"E11.30.5"),sQuery(id+"F0.wireOp",EDGE,"E11.30.6"),sQuery(id+"F0.wireOp",EDGE,"E11.30.7"),sQuery(id+"F0.wireOp",EDGE,"E11.30.8"),sQuery(id+"F0.wireOp",EDGE,"E11.30.10"),sQuery(id+"F0.wireOp",EDGE,"E11.30.11"),sQuery(id+"F0.wireOp",EDGE,"E11.31.0"),sQuery(id+"F0.wireOp",EDGE,"E11.31.1"),sQuery(id+"F0.wireOp",EDGE,"E11.31.3"),sQuery(id+"F0.wireOp",EDGE,"E11.31.4"),sQuery(id+"F0.wireOp",EDGE,"E11.31.5"),sQuery(id+"F0.wireOp",EDGE,"E11.31.6"),sQuery(id+"F0.wireOp",EDGE,"E11.31.7"),sQuery(id+"F0.wireOp",EDGE,"E11.31.8"),sQuery(id+"F0.wireOp",EDGE,"E11.31.10"),sQuery(id+"F0.wireOp",EDGE,"E11.31.11"),sQuery(id+"F0.wireOp",EDGE,"E11.32.0"),sQuery(id+"F0.wireOp",EDGE,"E11.32.1"),sQuery(id+"F0.wireOp",EDGE,"E11.32.3"),sQuery(id+"F0.wireOp",EDGE,"E11.32.4"),sQuery(id+"F0.wireOp",EDGE,"E11.32.5"),sQuery(id+"F0.wireOp",EDGE,"E11.32.6"),sQuery(id+"F0.wireOp",EDGE,"E11.32.7"),sQuery(id+"F0.wireOp",EDGE,"E11.32.8"),sQuery(id+"F0.wireOp",EDGE,"E11.32.10"),sQuery(id+"F0.wireOp",EDGE,"E11.32.11"),sQuery(id+"F0.wireOp",EDGE,"E11.33.0"),sQuery(id+"F0.wireOp",EDGE,"E11.33.1"),sQuery(id+"F0.wireOp",EDGE,"E11.33.3"),sQuery(id+"F0.wireOp",EDGE,"E11.33.4"),sQuery(id+"F0.wireOp",EDGE,"E11.33.5"),sQuery(id+"F0.wireOp",EDGE,"E11.33.6"),sQuery(id+"F0.wireOp",EDGE,"E11.33.7"),sQuery(id+"F0.wireOp",EDGE,"E11.33.8"),sQuery(id+"F0.wireOp",EDGE,"E11.33.10"),sQuery(id+"F0.wireOp",EDGE,"E11.33.11"),sQuery(id+"F0.wireOp",EDGE,"E11.34.0"),sQuery(id+"F0.wireOp",EDGE,"E11.34.1"),sQuery(id+"F0.wireOp",EDGE,"E11.34.3"),sQuery(id+"F0.wireOp",EDGE,"E11.34.4"),sQuery(id+"F0.wireOp",EDGE,"E11.34.5"),sQuery(id+"F0.wireOp",EDGE,"E11.34.6"),sQuery(id+"F0.wireOp",EDGE,"E11.34.7"),sQuery(id+"F0.wireOp",EDGE,"E11.34.8"),sQuery(id+"F0.wireOp",EDGE,"E11.34.10"),sQuery(id+"F0.wireOp",EDGE,"E11.34.11"),sQuery(id+"F0.wireOp",EDGE,"E11.35.0"),sQuery(id+"F0.wireOp",EDGE,"E11.35.1"),sQuery(id+"F0.wireOp",EDGE,"E11.35.3"),sQuery(id+"F0.wireOp",EDGE,"E11.35.4"),sQuery(id+"F0.wireOp",EDGE,"E11.35.5"),sQuery(id+"F0.wireOp",EDGE,"E11.35.6"),sQuery(id+"F0.wireOp",EDGE,"E11.35.7"),sQuery(id+"F0.wireOp",EDGE,"E11.35.8"),sQuery(id+"F0.wireOp",EDGE,"E11.35.10"),sQuery(id+"F0.wireOp",EDGE,"E11.35.11"),sQuery(id+"F0.wireOp",EDGE,"E12.trimOffspring"),sQuery(id+"F0.wireOp",EDGE,"E13.trimOffspring"),sQuery(id+"F0.wireOp",EDGE,"E14.trimOffspring"),sQuery(id+"F0.wireOp",EDGE,"E15.trimOffspring"),sQuery(id+"F0.wireOp",EDGE,"E16.trimOffspring"),sQuery(id+"F0.wireOp",EDGE,"E17.trimOffspring"),sQuery(id+"F0.wireOp",EDGE,"E18.trimOffspring"),sQuery(id+"F0.wireOp",EDGE,"E19.trimOffspring"),sQuery(id+"F0.wireOp",EDGE,"E20.trimOffspring"),sQuery(id+"F0.wireOp",EDGE,"E21.trimOffspring"),sQuery(id+"F0.wireOp",EDGE,"E22.trimOffspring"),sQuery(id+"F0.wireOp",EDGE,"E23.trimOffspring"),sQuery(id+"F0.wireOp",EDGE,"E24.trimOffspring"),sQuery(id+"F0.wireOp",EDGE,"E25.trimOffspring"),sQuery(id+"F0.wireOp",EDGE,"E26.trimOffspring"),sQuery(id+"F0.wireOp",EDGE,"E27.trimOffspring"),sQuery(id+"F0.wireOp",EDGE,"E28.trimOffspring"),sQuery(id+"F0.wireOp",EDGE,"E29.trimOffspring"),sQuery(id+"F0.wireOp",EDGE,"E30.trimOffspring"),sQuery(id+"F0.wireOp",EDGE,"E31.trimOffspring"),sQuery(id+"F0.wireOp",EDGE,"E32.trimOffspring"),sQuery(id+"F0.wireOp",EDGE,"E33.trimOffspring"),sQuery(id+"F0.wireOp",EDGE,"E34.trimOffspring"),sQuery(id+"F0.wireOp",EDGE,"E35.trimOffspring"),sQuery(id+"F0.wireOp",EDGE,"E36.trimOffspring"),sQuery(id+"F0.wireOp",EDGE,"E37.trimOffspring"),sQuery(id+"F0.wireOp",EDGE,"E38.trimOffspring"),sQuery(id+"F0.wireOp",EDGE,"E39.trimOffspring"),sQuery(id+"F0.wireOp",EDGE,"E40.trimOffspring"),sQuery(id+"F0.wireOp",EDGE,"E41.trimOffspring"),sQuery(id+"F0.wireOp",EDGE,"E42.trimOffspring"),sQuery(id+"F0.wireOp",EDGE,"E43.trimOffspring"),sQuery(id+"F0.wireOp",EDGE,"E44.trimOffspring"),sQuery(id+"F0.wireOp",EDGE,"E45.trimOffspring"),sQuery(id+"F0.wireOp",EDGE,"E46.trimOffspring")])],"isStart":false});
            var sketch = newSketch(context, id + "F2", { "sketchPlane" : qUnion([Q0])});
            skCircle(sketch, "E47", {"center": v(0, 0) * mm, "radius": 6.35 * mm});
            skPoint(sketch, "E48", {"position": v(0, 17.07) * mm});
            skPoint(sketch, "E49", {"position": v(1.27, 15.16) * mm});
            skPoint(sketch, "E50", {"position": v(0, 13.26) * mm});
            skPoint(sketch, "E51", {"position": v(-1.27, 11.35) * mm});
            skPoint(sketch, "E52", {"position": v(0, 9.45) * mm});
            skArc(sketch, "E53", {"start": v(1.04, 13.4) * mm, "mid": v(-1.2, 11.88) * mm, "end": v(0, 9.45) * mm});
            skArc(sketch, "E54", {"start": v(0.83, 13.9) * mm, "mid": v(1.2, 15.69) * mm, "end": v(0, 17.07) * mm});
            skArc(sketch, "E55", {"start": v(1.04, 13.4) * mm, "mid": v(1.67, 15.77) * mm, "end": v(0, 17.58) * mm});
            skArc(sketch, "E56", {"start": v(0.83, 13.9) * mm, "mid": v(-1.71, 11.77) * mm, "end": v(0, 8.94) * mm});
            skArc(sketch, "E57", {"start": v(0, 8.94) * mm, "mid": v(0.17, 9.2) * mm, "end": v(0, 9.45) * mm});
            skPoint(sketch, "E57.second.point", {"position": v(0, 8.94) * mm});
            skPoint(sketch, "E57.third.point", {"position": v(0.09, 9) * mm});
            skArc(sketch, "E58", {"start": v(0, 17.58) * mm, "mid": v(-0.17, 17.32) * mm, "end": v(0, 17.07) * mm});
            skPoint(sketch, "E58.second.point", {"position": v(0, 17.58) * mm});
            skPoint(sketch, "E58.third.point", {"position": v(-0.17, 17.35) * mm});
            skCircle(sketch, "E59", {"center": v(0.8, 11.35) * mm, "radius": 1.73 * mm});
            skSolve(sketch);
        }
        {
            var Q0;
            Q0=makeQuery(id+"F2.imprint","IMPRINT",FACE,{"disambiguationData":[TD([[makeQuery(id+"F2.imprint","IMPRINT",EDGE,{"derivedFrom":sQuery(id+"F2.wireOp",EDGE,"E47")}),1.0]])]});
            extrude(context, id + "F3", {"entities" : qUnion([Q0]), "operationType" : NewBodyOperationType.ADD, "depth" : 6.35 * mm});
        }
        {
            var Q0;
            Q0=makeQuery(id+"F3.opExtrude","CAP_FACE",FACE,{"disambiguationData":[OSD([sQuery(id+"F2.wireOp",EDGE,"E47")])],"isStart":false});
            var sketch = newSketch(context, id + "F4", { "sketchPlane" : qUnion([Q0])});
            skPoint(sketch, "E60", {"position": v(0, 0) * mm});
            skPoint(sketch, "E61", {"position": v(0, 5.22) * mm});
            skPoint(sketch, "E62.1.0", {"position": v(-5.22, 0) * mm});
            skPoint(sketch, "E62.2.0", {"position": v(0, -5.22) * mm});
            skPoint(sketch, "E62.3.0", {"position": v(5.22, 0) * mm});
            skSolve(sketch);
        }
        {
            var Q0;
            Q0=sQuery(id+"F4.wireOp",VERTEX,"E60");
            var Q1;
            Q1=makeQuery(id+"F1.opExtrude","SWEPT_BODY",BODY,{"disambiguationData":[OSD([sQuery(id+"F0.wireOp",EDGE,"E0"),sQuery(id+"F0.wireOp",EDGE,"E1.trimOffspring"),sQuery(id+"F0.wireOp",EDGE,"E2"),sQuery(id+"F0.wireOp",EDGE,"E3"),sQuery(id+"F0.wireOp",EDGE,"E4.MirrorCS"),sQuery(id+"F0.wireOp",EDGE,"E5.MirrorCS"),sQuery(id+"F0.wireOp",EDGE,"E6.MirrorCS"),sQuery(id+"F0.wireOp",EDGE,"E7.filletArc"),sQuery(id+"F0.wireOp",EDGE,"E8.filletArc"),sQuery(id+"F0.wireOp",EDGE,"E9.filletArc"),sQuery(id+"F0.wireOp",EDGE,"E10.filletArc"),sQuery(id+"F0.wireOp",EDGE,"E11.1.0"),sQuery(id+"F0.wireOp",EDGE,"E11.1.1"),sQuery(id+"F0.wireOp",EDGE,"E11.1.3"),sQuery(id+"F0.wireOp",EDGE,"E11.1.4"),sQuery(id+"F0.wireOp",EDGE,"E11.1.5"),sQuery(id+"F0.wireOp",EDGE,"E11.1.6"),sQuery(id+"F0.wireOp",EDGE,"E11.1.7"),sQuery(id+"F0.wireOp",EDGE,"E11.1.8"),sQuery(id+"F0.wireOp",EDGE,"E11.1.10"),sQuery(id+"F0.wireOp",EDGE,"E11.1.11"),sQuery(id+"F0.wireOp",EDGE,"E11.2.0"),sQuery(id+"F0.wireOp",EDGE,"E11.2.1"),sQuery(id+"F0.wireOp",EDGE,"E11.2.3"),sQuery(id+"F0.wireOp",EDGE,"E11.2.4"),sQuery(id+"F0.wireOp",EDGE,"E11.2.5"),sQuery(id+"F0.wireOp",EDGE,"E11.2.6"),sQuery(id+"F0.wireOp",EDGE,"E11.2.7"),sQuery(id+"F0.wireOp",EDGE,"E11.2.8"),sQuery(id+"F0.wireOp",EDGE,"E11.2.10"),sQuery(id+"F0.wireOp",EDGE,"E11.2.11"),sQuery(id+"F0.wireOp",EDGE,"E11.3.0"),sQuery(id+"F0.wireOp",EDGE,"E11.3.1"),sQuery(id+"F0.wireOp",EDGE,"E11.3.3"),sQuery(id+"F0.wireOp",EDGE,"E11.3.4"),sQuery(id+"F0.wireOp",EDGE,"E11.3.5"),sQuery(id+"F0.wireOp",EDGE,"E11.3.6"),sQuery(id+"F0.wireOp",EDGE,"E11.3.7"),sQuery(id+"F0.wireOp",EDGE,"E11.3.8"),sQuery(id+"F0.wireOp",EDGE,"E11.3.10"),sQuery(id+"F0.wireOp",EDGE,"E11.3.11"),sQuery(id+"F0.wireOp",EDGE,"E11.4.0"),sQuery(id+"F0.wireOp",EDGE,"E11.4.1"),sQuery(id+"F0.wireOp",EDGE,"E11.4.3"),sQuery(id+"F0.wireOp",EDGE,"E11.4.4"),sQuery(id+"F0.wireOp",EDGE,"E11.4.5"),sQuery(id+"F0.wireOp",EDGE,"E11.4.6"),sQuery(id+"F0.wireOp",EDGE,"E11.4.7"),sQuery(id+"F0.wireOp",EDGE,"E11.4.8"),sQuery(id+"F0.wireOp",EDGE,"E11.4.10"),sQuery(id+"F0.wireOp",EDGE,"E11.4.11"),sQuery(id+"F0.wireOp",EDGE,"E11.5.0"),sQuery(id+"F0.wireOp",EDGE,"E11.5.1"),sQuery(id+"F0.wireOp",EDGE,"E11.5.3"),sQuery(id+"F0.wireOp",EDGE,"E11.5.4"),sQuery(id+"F0.wireOp",EDGE,"E11.5.5"),sQuery(id+"F0.wireOp",EDGE,"E11.5.6"),sQuery(id+"F0.wireOp",EDGE,"E11.5.7"),sQuery(id+"F0.wireOp",EDGE,"E11.5.8"),sQuery(id+"F0.wireOp",EDGE,"E11.5.10"),sQuery(id+"F0.wireOp",EDGE,"E11.5.11"),sQuery(id+"F0.wireOp",EDGE,"E11.6.0"),sQuery(id+"F0.wireOp",EDGE,"E11.6.1"),sQuery(id+"F0.wireOp",EDGE,"E11.6.3"),sQuery(id+"F0.wireOp",EDGE,"E11.6.4"),sQuery(id+"F0.wireOp",EDGE,"E11.6.5"),sQuery(id+"F0.wireOp",EDGE,"E11.6.6"),sQuery(id+"F0.wireOp",EDGE,"E11.6.7"),sQuery(id+"F0.wireOp",EDGE,"E11.6.8"),sQuery(id+"F0.wireOp",EDGE,"E11.6.10"),sQuery(id+"F0.wireOp",EDGE,"E11.6.11"),sQuery(id+"F0.wireOp",EDGE,"E11.7.0"),sQuery(id+"F0.wireOp",EDGE,"E11.7.1"),sQuery(id+"F0.wireOp",EDGE,"E11.7.3"),sQuery(id+"F0.wireOp",EDGE,"E11.7.4"),sQuery(id+"F0.wireOp",EDGE,"E11.7.5"),sQuery(id+"F0.wireOp",EDGE,"E11.7.6"),sQuery(id+"F0.wireOp",EDGE,"E11.7.7"),sQuery(id+"F0.wireOp",EDGE,"E11.7.8"),sQuery(id+"F0.wireOp",EDGE,"E11.7.10"),sQuery(id+"F0.wireOp",EDGE,"E11.7.11"),sQuery(id+"F0.wireOp",EDGE,"E11.8.0"),sQuery(id+"F0.wireOp",EDGE,"E11.8.1"),sQuery(id+"F0.wireOp",EDGE,"E11.8.3"),sQuery(id+"F0.wireOp",EDGE,"E11.8.4"),sQuery(id+"F0.wireOp",EDGE,"E11.8.5"),sQuery(id+"F0.wireOp",EDGE,"E11.8.6"),sQuery(id+"F0.wireOp",EDGE,"E11.8.7"),sQuery(id+"F0.wireOp",EDGE,"E11.8.8"),sQuery(id+"F0.wireOp",EDGE,"E11.8.10"),sQuery(id+"F0.wireOp",EDGE,"E11.8.11"),sQuery(id+"F0.wireOp",EDGE,"E11.9.0"),sQuery(id+"F0.wireOp",EDGE,"E11.9.1"),sQuery(id+"F0.wireOp",EDGE,"E11.9.3"),sQuery(id+"F0.wireOp",EDGE,"E11.9.4"),sQuery(id+"F0.wireOp",EDGE,"E11.9.5"),sQuery(id+"F0.wireOp",EDGE,"E11.9.6"),sQuery(id+"F0.wireOp",EDGE,"E11.9.7"),sQuery(id+"F0.wireOp",EDGE,"E11.9.8"),sQuery(id+"F0.wireOp",EDGE,"E11.9.10"),sQuery(id+"F0.wireOp",EDGE,"E11.9.11"),sQuery(id+"F0.wireOp",EDGE,"E11.10.0"),sQuery(id+"F0.wireOp",EDGE,"E11.10.1"),sQuery(id+"F0.wireOp",EDGE,"E11.10.3"),sQuery(id+"F0.wireOp",EDGE,"E11.10.4"),sQuery(id+"F0.wireOp",EDGE,"E11.10.5"),sQuery(id+"F0.wireOp",EDGE,"E11.10.6"),sQuery(id+"F0.wireOp",EDGE,"E11.10.7"),sQuery(id+"F0.wireOp",EDGE,"E11.10.8"),sQuery(id+"F0.wireOp",EDGE,"E11.10.10"),sQuery(id+"F0.wireOp",EDGE,"E11.10.11"),sQuery(id+"F0.wireOp",EDGE,"E11.11.0"),sQuery(id+"F0.wireOp",EDGE,"E11.11.1"),sQuery(id+"F0.wireOp",EDGE,"E11.11.3"),sQuery(id+"F0.wireOp",EDGE,"E11.11.4"),sQuery(id+"F0.wireOp",EDGE,"E11.11.5"),sQuery(id+"F0.wireOp",EDGE,"E11.11.6"),sQuery(id+"F0.wireOp",EDGE,"E11.11.7"),sQuery(id+"F0.wireOp",EDGE,"E11.11.8"),sQuery(id+"F0.wireOp",EDGE,"E11.11.10"),sQuery(id+"F0.wireOp",EDGE,"E11.11.11"),sQuery(id+"F0.wireOp",EDGE,"E11.12.0"),sQuery(id+"F0.wireOp",EDGE,"E11.12.1"),sQuery(id+"F0.wireOp",EDGE,"E11.12.3"),sQuery(id+"F0.wireOp",EDGE,"E11.12.4"),sQuery(id+"F0.wireOp",EDGE,"E11.12.5"),sQuery(id+"F0.wireOp",EDGE,"E11.12.6"),sQuery(id+"F0.wireOp",EDGE,"E11.12.7"),sQuery(id+"F0.wireOp",EDGE,"E11.12.8"),sQuery(id+"F0.wireOp",EDGE,"E11.12.10"),sQuery(id+"F0.wireOp",EDGE,"E11.12.11"),sQuery(id+"F0.wireOp",EDGE,"E11.13.0"),sQuery(id+"F0.wireOp",EDGE,"E11.13.1"),sQuery(id+"F0.wireOp",EDGE,"E11.13.3"),sQuery(id+"F0.wireOp",EDGE,"E11.13.4"),sQuery(id+"F0.wireOp",EDGE,"E11.13.5"),sQuery(id+"F0.wireOp",EDGE,"E11.13.6"),sQuery(id+"F0.wireOp",EDGE,"E11.13.7"),sQuery(id+"F0.wireOp",EDGE,"E11.13.8"),sQuery(id+"F0.wireOp",EDGE,"E11.13.10"),sQuery(id+"F0.wireOp",EDGE,"E11.13.11"),sQuery(id+"F0.wireOp",EDGE,"E11.14.0"),sQuery(id+"F0.wireOp",EDGE,"E11.14.1"),sQuery(id+"F0.wireOp",EDGE,"E11.14.3"),sQuery(id+"F0.wireOp",EDGE,"E11.14.4"),sQuery(id+"F0.wireOp",EDGE,"E11.14.5"),sQuery(id+"F0.wireOp",EDGE,"E11.14.6"),sQuery(id+"F0.wireOp",EDGE,"E11.14.7"),sQuery(id+"F0.wireOp",EDGE,"E11.14.8"),sQuery(id+"F0.wireOp",EDGE,"E11.14.10"),sQuery(id+"F0.wireOp",EDGE,"E11.14.11"),sQuery(id+"F0.wireOp",EDGE,"E11.15.0"),sQuery(id+"F0.wireOp",EDGE,"E11.15.1"),sQuery(id+"F0.wireOp",EDGE,"E11.15.3"),sQuery(id+"F0.wireOp",EDGE,"E11.15.4"),sQuery(id+"F0.wireOp",EDGE,"E11.15.5"),sQuery(id+"F0.wireOp",EDGE,"E11.15.6"),sQuery(id+"F0.wireOp",EDGE,"E11.15.7"),sQuery(id+"F0.wireOp",EDGE,"E11.15.8"),sQuery(id+"F0.wireOp",EDGE,"E11.15.10"),sQuery(id+"F0.wireOp",EDGE,"E11.15.11"),sQuery(id+"F0.wireOp",EDGE,"E11.16.0"),sQuery(id+"F0.wireOp",EDGE,"E11.16.1"),sQuery(id+"F0.wireOp",EDGE,"E11.16.3"),sQuery(id+"F0.wireOp",EDGE,"E11.16.4"),sQuery(id+"F0.wireOp",EDGE,"E11.16.5"),sQuery(id+"F0.wireOp",EDGE,"E11.16.6"),sQuery(id+"F0.wireOp",EDGE,"E11.16.7"),sQuery(id+"F0.wireOp",EDGE,"E11.16.8"),sQuery(id+"F0.wireOp",EDGE,"E11.16.10"),sQuery(id+"F0.wireOp",EDGE,"E11.16.11"),sQuery(id+"F0.wireOp",EDGE,"E11.17.0"),sQuery(id+"F0.wireOp",EDGE,"E11.17.1"),sQuery(id+"F0.wireOp",EDGE,"E11.17.3"),sQuery(id+"F0.wireOp",EDGE,"E11.17.4"),sQuery(id+"F0.wireOp",EDGE,"E11.17.5"),sQuery(id+"F0.wireOp",EDGE,"E11.17.6"),sQuery(id+"F0.wireOp",EDGE,"E11.17.7"),sQuery(id+"F0.wireOp",EDGE,"E11.17.8"),sQuery(id+"F0.wireOp",EDGE,"E11.17.10"),sQuery(id+"F0.wireOp",EDGE,"E11.17.11"),sQuery(id+"F0.wireOp",EDGE,"E11.18.0"),sQuery(id+"F0.wireOp",EDGE,"E11.18.1"),sQuery(id+"F0.wireOp",EDGE,"E11.18.3"),sQuery(id+"F0.wireOp",EDGE,"E11.18.4"),sQuery(id+"F0.wireOp",EDGE,"E11.18.5"),sQuery(id+"F0.wireOp",EDGE,"E11.18.6"),sQuery(id+"F0.wireOp",EDGE,"E11.18.7"),sQuery(id+"F0.wireOp",EDGE,"E11.18.8"),sQuery(id+"F0.wireOp",EDGE,"E11.18.10"),sQuery(id+"F0.wireOp",EDGE,"E11.18.11"),sQuery(id+"F0.wireOp",EDGE,"E11.19.0"),sQuery(id+"F0.wireOp",EDGE,"E11.19.1"),sQuery(id+"F0.wireOp",EDGE,"E11.19.3"),sQuery(id+"F0.wireOp",EDGE,"E11.19.4"),sQuery(id+"F0.wireOp",EDGE,"E11.19.5"),sQuery(id+"F0.wireOp",EDGE,"E11.19.6"),sQuery(id+"F0.wireOp",EDGE,"E11.19.7"),sQuery(id+"F0.wireOp",EDGE,"E11.19.8"),sQuery(id+"F0.wireOp",EDGE,"E11.19.10"),sQuery(id+"F0.wireOp",EDGE,"E11.19.11"),sQuery(id+"F0.wireOp",EDGE,"E11.20.0"),sQuery(id+"F0.wireOp",EDGE,"E11.20.1"),sQuery(id+"F0.wireOp",EDGE,"E11.20.3"),sQuery(id+"F0.wireOp",EDGE,"E11.20.4"),sQuery(id+"F0.wireOp",EDGE,"E11.20.5"),sQuery(id+"F0.wireOp",EDGE,"E11.20.6"),sQuery(id+"F0.wireOp",EDGE,"E11.20.7"),sQuery(id+"F0.wireOp",EDGE,"E11.20.8"),sQuery(id+"F0.wireOp",EDGE,"E11.20.10"),sQuery(id+"F0.wireOp",EDGE,"E11.20.11"),sQuery(id+"F0.wireOp",EDGE,"E11.21.0"),sQuery(id+"F0.wireOp",EDGE,"E11.21.1"),sQuery(id+"F0.wireOp",EDGE,"E11.21.3"),sQuery(id+"F0.wireOp",EDGE,"E11.21.4"),sQuery(id+"F0.wireOp",EDGE,"E11.21.5"),sQuery(id+"F0.wireOp",EDGE,"E11.21.6"),sQuery(id+"F0.wireOp",EDGE,"E11.21.7"),sQuery(id+"F0.wireOp",EDGE,"E11.21.8"),sQuery(id+"F0.wireOp",EDGE,"E11.21.10"),sQuery(id+"F0.wireOp",EDGE,"E11.21.11"),sQuery(id+"F0.wireOp",EDGE,"E11.22.0"),sQuery(id+"F0.wireOp",EDGE,"E11.22.1"),sQuery(id+"F0.wireOp",EDGE,"E11.22.3"),sQuery(id+"F0.wireOp",EDGE,"E11.22.4"),sQuery(id+"F0.wireOp",EDGE,"E11.22.5"),sQuery(id+"F0.wireOp",EDGE,"E11.22.6"),sQuery(id+"F0.wireOp",EDGE,"E11.22.7"),sQuery(id+"F0.wireOp",EDGE,"E11.22.8"),sQuery(id+"F0.wireOp",EDGE,"E11.22.10"),sQuery(id+"F0.wireOp",EDGE,"E11.22.11"),sQuery(id+"F0.wireOp",EDGE,"E11.23.0"),sQuery(id+"F0.wireOp",EDGE,"E11.23.1"),sQuery(id+"F0.wireOp",EDGE,"E11.23.3"),sQuery(id+"F0.wireOp",EDGE,"E11.23.4"),sQuery(id+"F0.wireOp",EDGE,"E11.23.5"),sQuery(id+"F0.wireOp",EDGE,"E11.23.6"),sQuery(id+"F0.wireOp",EDGE,"E11.23.7"),sQuery(id+"F0.wireOp",EDGE,"E11.23.8"),sQuery(id+"F0.wireOp",EDGE,"E11.23.10"),sQuery(id+"F0.wireOp",EDGE,"E11.23.11"),sQuery(id+"F0.wireOp",EDGE,"E11.24.0"),sQuery(id+"F0.wireOp",EDGE,"E11.24.1"),sQuery(id+"F0.wireOp",EDGE,"E11.24.3"),sQuery(id+"F0.wireOp",EDGE,"E11.24.4"),sQuery(id+"F0.wireOp",EDGE,"E11.24.5"),sQuery(id+"F0.wireOp",EDGE,"E11.24.6"),sQuery(id+"F0.wireOp",EDGE,"E11.24.7"),sQuery(id+"F0.wireOp",EDGE,"E11.24.8"),sQuery(id+"F0.wireOp",EDGE,"E11.24.10"),sQuery(id+"F0.wireOp",EDGE,"E11.24.11"),sQuery(id+"F0.wireOp",EDGE,"E11.25.0"),sQuery(id+"F0.wireOp",EDGE,"E11.25.1"),sQuery(id+"F0.wireOp",EDGE,"E11.25.3"),sQuery(id+"F0.wireOp",EDGE,"E11.25.4"),sQuery(id+"F0.wireOp",EDGE,"E11.25.5"),sQuery(id+"F0.wireOp",EDGE,"E11.25.6"),sQuery(id+"F0.wireOp",EDGE,"E11.25.7"),sQuery(id+"F0.wireOp",EDGE,"E11.25.8"),sQuery(id+"F0.wireOp",EDGE,"E11.25.10"),sQuery(id+"F0.wireOp",EDGE,"E11.25.11"),sQuery(id+"F0.wireOp",EDGE,"E11.26.0"),sQuery(id+"F0.wireOp",EDGE,"E11.26.1"),sQuery(id+"F0.wireOp",EDGE,"E11.26.3"),sQuery(id+"F0.wireOp",EDGE,"E11.26.4"),sQuery(id+"F0.wireOp",EDGE,"E11.26.5"),sQuery(id+"F0.wireOp",EDGE,"E11.26.6"),sQuery(id+"F0.wireOp",EDGE,"E11.26.7"),sQuery(id+"F0.wireOp",EDGE,"E11.26.8"),sQuery(id+"F0.wireOp",EDGE,"E11.26.10"),sQuery(id+"F0.wireOp",EDGE,"E11.26.11"),sQuery(id+"F0.wireOp",EDGE,"E11.27.0"),sQuery(id+"F0.wireOp",EDGE,"E11.27.1"),sQuery(id+"F0.wireOp",EDGE,"E11.27.3"),sQuery(id+"F0.wireOp",EDGE,"E11.27.4"),sQuery(id+"F0.wireOp",EDGE,"E11.27.5"),sQuery(id+"F0.wireOp",EDGE,"E11.27.6"),sQuery(id+"F0.wireOp",EDGE,"E11.27.7"),sQuery(id+"F0.wireOp",EDGE,"E11.27.8"),sQuery(id+"F0.wireOp",EDGE,"E11.27.10"),sQuery(id+"F0.wireOp",EDGE,"E11.27.11"),sQuery(id+"F0.wireOp",EDGE,"E11.28.0"),sQuery(id+"F0.wireOp",EDGE,"E11.28.1"),sQuery(id+"F0.wireOp",EDGE,"E11.28.3"),sQuery(id+"F0.wireOp",EDGE,"E11.28.4"),sQuery(id+"F0.wireOp",EDGE,"E11.28.5"),sQuery(id+"F0.wireOp",EDGE,"E11.28.6"),sQuery(id+"F0.wireOp",EDGE,"E11.28.7"),sQuery(id+"F0.wireOp",EDGE,"E11.28.8"),sQuery(id+"F0.wireOp",EDGE,"E11.28.10"),sQuery(id+"F0.wireOp",EDGE,"E11.28.11"),sQuery(id+"F0.wireOp",EDGE,"E11.29.0"),sQuery(id+"F0.wireOp",EDGE,"E11.29.1"),sQuery(id+"F0.wireOp",EDGE,"E11.29.3"),sQuery(id+"F0.wireOp",EDGE,"E11.29.4"),sQuery(id+"F0.wireOp",EDGE,"E11.29.5"),sQuery(id+"F0.wireOp",EDGE,"E11.29.6"),sQuery(id+"F0.wireOp",EDGE,"E11.29.7"),sQuery(id+"F0.wireOp",EDGE,"E11.29.8"),sQuery(id+"F0.wireOp",EDGE,"E11.29.10"),sQuery(id+"F0.wireOp",EDGE,"E11.29.11"),sQuery(id+"F0.wireOp",EDGE,"E11.30.0"),sQuery(id+"F0.wireOp",EDGE,"E11.30.1"),sQuery(id+"F0.wireOp",EDGE,"E11.30.3"),sQuery(id+"F0.wireOp",EDGE,"E11.30.4"),sQuery(id+"F0.wireOp",EDGE,"E11.30.5"),sQuery(id+"F0.wireOp",EDGE,"E11.30.6"),sQuery(id+"F0.wireOp",EDGE,"E11.30.7"),sQuery(id+"F0.wireOp",EDGE,"E11.30.8"),sQuery(id+"F0.wireOp",EDGE,"E11.30.10"),sQuery(id+"F0.wireOp",EDGE,"E11.30.11"),sQuery(id+"F0.wireOp",EDGE,"E11.31.0"),sQuery(id+"F0.wireOp",EDGE,"E11.31.1"),sQuery(id+"F0.wireOp",EDGE,"E11.31.3"),sQuery(id+"F0.wireOp",EDGE,"E11.31.4"),sQuery(id+"F0.wireOp",EDGE,"E11.31.5"),sQuery(id+"F0.wireOp",EDGE,"E11.31.6"),sQuery(id+"F0.wireOp",EDGE,"E11.31.7"),sQuery(id+"F0.wireOp",EDGE,"E11.31.8"),sQuery(id+"F0.wireOp",EDGE,"E11.31.10"),sQuery(id+"F0.wireOp",EDGE,"E11.31.11"),sQuery(id+"F0.wireOp",EDGE,"E11.32.0"),sQuery(id+"F0.wireOp",EDGE,"E11.32.1"),sQuery(id+"F0.wireOp",EDGE,"E11.32.3"),sQuery(id+"F0.wireOp",EDGE,"E11.32.4"),sQuery(id+"F0.wireOp",EDGE,"E11.32.5"),sQuery(id+"F0.wireOp",EDGE,"E11.32.6"),sQuery(id+"F0.wireOp",EDGE,"E11.32.7"),sQuery(id+"F0.wireOp",EDGE,"E11.32.8"),sQuery(id+"F0.wireOp",EDGE,"E11.32.10"),sQuery(id+"F0.wireOp",EDGE,"E11.32.11"),sQuery(id+"F0.wireOp",EDGE,"E11.33.0"),sQuery(id+"F0.wireOp",EDGE,"E11.33.1"),sQuery(id+"F0.wireOp",EDGE,"E11.33.3"),sQuery(id+"F0.wireOp",EDGE,"E11.33.4"),sQuery(id+"F0.wireOp",EDGE,"E11.33.5"),sQuery(id+"F0.wireOp",EDGE,"E11.33.6"),sQuery(id+"F0.wireOp",EDGE,"E11.33.7"),sQuery(id+"F0.wireOp",EDGE,"E11.33.8"),sQuery(id+"F0.wireOp",EDGE,"E11.33.10"),sQuery(id+"F0.wireOp",EDGE,"E11.33.11"),sQuery(id+"F0.wireOp",EDGE,"E11.34.0"),sQuery(id+"F0.wireOp",EDGE,"E11.34.1"),sQuery(id+"F0.wireOp",EDGE,"E11.34.3"),sQuery(id+"F0.wireOp",EDGE,"E11.34.4"),sQuery(id+"F0.wireOp",EDGE,"E11.34.5"),sQuery(id+"F0.wireOp",EDGE,"E11.34.6"),sQuery(id+"F0.wireOp",EDGE,"E11.34.7"),sQuery(id+"F0.wireOp",EDGE,"E11.34.8"),sQuery(id+"F0.wireOp",EDGE,"E11.34.10"),sQuery(id+"F0.wireOp",EDGE,"E11.34.11"),sQuery(id+"F0.wireOp",EDGE,"E11.35.0"),sQuery(id+"F0.wireOp",EDGE,"E11.35.1"),sQuery(id+"F0.wireOp",EDGE,"E11.35.3"),sQuery(id+"F0.wireOp",EDGE,"E11.35.4"),sQuery(id+"F0.wireOp",EDGE,"E11.35.5"),sQuery(id+"F0.wireOp",EDGE,"E11.35.6"),sQuery(id+"F0.wireOp",EDGE,"E11.35.7"),sQuery(id+"F0.wireOp",EDGE,"E11.35.8"),sQuery(id+"F0.wireOp",EDGE,"E11.35.10"),sQuery(id+"F0.wireOp",EDGE,"E11.35.11"),sQuery(id+"F0.wireOp",EDGE,"E12.trimOffspring"),sQuery(id+"F0.wireOp",EDGE,"E13.trimOffspring"),sQuery(id+"F0.wireOp",EDGE,"E14.trimOffspring"),sQuery(id+"F0.wireOp",EDGE,"E15.trimOffspring"),sQuery(id+"F0.wireOp",EDGE,"E16.trimOffspring"),sQuery(id+"F0.wireOp",EDGE,"E17.trimOffspring"),sQuery(id+"F0.wireOp",EDGE,"E18.trimOffspring"),sQuery(id+"F0.wireOp",EDGE,"E19.trimOffspring"),sQuery(id+"F0.wireOp",EDGE,"E20.trimOffspring"),sQuery(id+"F0.wireOp",EDGE,"E21.trimOffspring"),sQuery(id+"F0.wireOp",EDGE,"E22.trimOffspring"),sQuery(id+"F0.wireOp",EDGE,"E23.trimOffspring"),sQuery(id+"F0.wireOp",EDGE,"E24.trimOffspring"),sQuery(id+"F0.wireOp",EDGE,"E25.trimOffspring"),sQuery(id+"F0.wireOp",EDGE,"E26.trimOffspring"),sQuery(id+"F0.wireOp",EDGE,"E27.trimOffspring"),sQuery(id+"F0.wireOp",EDGE,"E28.trimOffspring"),sQuery(id+"F0.wireOp",EDGE,"E29.trimOffspring"),sQuery(id+"F0.wireOp",EDGE,"E30.trimOffspring"),sQuery(id+"F0.wireOp",EDGE,"E31.trimOffspring"),sQuery(id+"F0.wireOp",EDGE,"E32.trimOffspring"),sQuery(id+"F0.wireOp",EDGE,"E33.trimOffspring"),sQuery(id+"F0.wireOp",EDGE,"E34.trimOffspring"),sQuery(id+"F0.wireOp",EDGE,"E35.trimOffspring"),sQuery(id+"F0.wireOp",EDGE,"E36.trimOffspring"),sQuery(id+"F0.wireOp",EDGE,"E37.trimOffspring"),sQuery(id+"F0.wireOp",EDGE,"E38.trimOffspring"),sQuery(id+"F0.wireOp",EDGE,"E39.trimOffspring"),sQuery(id+"F0.wireOp",EDGE,"E40.trimOffspring"),sQuery(id+"F0.wireOp",EDGE,"E41.trimOffspring"),sQuery(id+"F0.wireOp",EDGE,"E42.trimOffspring"),sQuery(id+"F0.wireOp",EDGE,"E43.trimOffspring"),sQuery(id+"F0.wireOp",EDGE,"E44.trimOffspring"),sQuery(id+"F0.wireOp",EDGE,"E45.trimOffspring"),sQuery(id+"F0.wireOp",EDGE,"E46.trimOffspring")])]});
            hole(context, id + "F5", {"style" : HoleStyle.SIMPLE, "endStyle" : HoleEndStyle.THROUGH, "holeDiameter" : 7.87 * mm, "locations" : qUnion([Q0]), "scope" : qUnion([Q1]), "isTappedThrough" : true});
        }
        {
            var Q0;
            Q0=sQuery(id+"F4.wireOp",VERTEX,"E61");
            var Q1;
            Q1=sQuery(id+"F4.wireOp",VERTEX,"E62.3.0");
            var Q2;
            Q2=sQuery(id+"F4.wireOp",VERTEX,"E62.2.0");
            var Q3;
            Q3=sQuery(id+"F4.wireOp",VERTEX,"E62.1.0");
            var Q4;
            Q4=makeQuery(id+"F1.opExtrude","SWEPT_BODY",BODY,{"disambiguationData":[OSD([sQuery(id+"F0.wireOp",EDGE,"E0"),sQuery(id+"F0.wireOp",EDGE,"E1.trimOffspring"),sQuery(id+"F0.wireOp",EDGE,"E2"),sQuery(id+"F0.wireOp",EDGE,"E3"),sQuery(id+"F0.wireOp",EDGE,"E4.MirrorCS"),sQuery(id+"F0.wireOp",EDGE,"E5.MirrorCS"),sQuery(id+"F0.wireOp",EDGE,"E6.MirrorCS"),sQuery(id+"F0.wireOp",EDGE,"E7.filletArc"),sQuery(id+"F0.wireOp",EDGE,"E8.filletArc"),sQuery(id+"F0.wireOp",EDGE,"E9.filletArc"),sQuery(id+"F0.wireOp",EDGE,"E10.filletArc"),sQuery(id+"F0.wireOp",EDGE,"E11.1.0"),sQuery(id+"F0.wireOp",EDGE,"E11.1.1"),sQuery(id+"F0.wireOp",EDGE,"E11.1.3"),sQuery(id+"F0.wireOp",EDGE,"E11.1.4"),sQuery(id+"F0.wireOp",EDGE,"E11.1.5"),sQuery(id+"F0.wireOp",EDGE,"E11.1.6"),sQuery(id+"F0.wireOp",EDGE,"E11.1.7"),sQuery(id+"F0.wireOp",EDGE,"E11.1.8"),sQuery(id+"F0.wireOp",EDGE,"E11.1.10"),sQuery(id+"F0.wireOp",EDGE,"E11.1.11"),sQuery(id+"F0.wireOp",EDGE,"E11.2.0"),sQuery(id+"F0.wireOp",EDGE,"E11.2.1"),sQuery(id+"F0.wireOp",EDGE,"E11.2.3"),sQuery(id+"F0.wireOp",EDGE,"E11.2.4"),sQuery(id+"F0.wireOp",EDGE,"E11.2.5"),sQuery(id+"F0.wireOp",EDGE,"E11.2.6"),sQuery(id+"F0.wireOp",EDGE,"E11.2.7"),sQuery(id+"F0.wireOp",EDGE,"E11.2.8"),sQuery(id+"F0.wireOp",EDGE,"E11.2.10"),sQuery(id+"F0.wireOp",EDGE,"E11.2.11"),sQuery(id+"F0.wireOp",EDGE,"E11.3.0"),sQuery(id+"F0.wireOp",EDGE,"E11.3.1"),sQuery(id+"F0.wireOp",EDGE,"E11.3.3"),sQuery(id+"F0.wireOp",EDGE,"E11.3.4"),sQuery(id+"F0.wireOp",EDGE,"E11.3.5"),sQuery(id+"F0.wireOp",EDGE,"E11.3.6"),sQuery(id+"F0.wireOp",EDGE,"E11.3.7"),sQuery(id+"F0.wireOp",EDGE,"E11.3.8"),sQuery(id+"F0.wireOp",EDGE,"E11.3.10"),sQuery(id+"F0.wireOp",EDGE,"E11.3.11"),sQuery(id+"F0.wireOp",EDGE,"E11.4.0"),sQuery(id+"F0.wireOp",EDGE,"E11.4.1"),sQuery(id+"F0.wireOp",EDGE,"E11.4.3"),sQuery(id+"F0.wireOp",EDGE,"E11.4.4"),sQuery(id+"F0.wireOp",EDGE,"E11.4.5"),sQuery(id+"F0.wireOp",EDGE,"E11.4.6"),sQuery(id+"F0.wireOp",EDGE,"E11.4.7"),sQuery(id+"F0.wireOp",EDGE,"E11.4.8"),sQuery(id+"F0.wireOp",EDGE,"E11.4.10"),sQuery(id+"F0.wireOp",EDGE,"E11.4.11"),sQuery(id+"F0.wireOp",EDGE,"E11.5.0"),sQuery(id+"F0.wireOp",EDGE,"E11.5.1"),sQuery(id+"F0.wireOp",EDGE,"E11.5.3"),sQuery(id+"F0.wireOp",EDGE,"E11.5.4"),sQuery(id+"F0.wireOp",EDGE,"E11.5.5"),sQuery(id+"F0.wireOp",EDGE,"E11.5.6"),sQuery(id+"F0.wireOp",EDGE,"E11.5.7"),sQuery(id+"F0.wireOp",EDGE,"E11.5.8"),sQuery(id+"F0.wireOp",EDGE,"E11.5.10"),sQuery(id+"F0.wireOp",EDGE,"E11.5.11"),sQuery(id+"F0.wireOp",EDGE,"E11.6.0"),sQuery(id+"F0.wireOp",EDGE,"E11.6.1"),sQuery(id+"F0.wireOp",EDGE,"E11.6.3"),sQuery(id+"F0.wireOp",EDGE,"E11.6.4"),sQuery(id+"F0.wireOp",EDGE,"E11.6.5"),sQuery(id+"F0.wireOp",EDGE,"E11.6.6"),sQuery(id+"F0.wireOp",EDGE,"E11.6.7"),sQuery(id+"F0.wireOp",EDGE,"E11.6.8"),sQuery(id+"F0.wireOp",EDGE,"E11.6.10"),sQuery(id+"F0.wireOp",EDGE,"E11.6.11"),sQuery(id+"F0.wireOp",EDGE,"E11.7.0"),sQuery(id+"F0.wireOp",EDGE,"E11.7.1"),sQuery(id+"F0.wireOp",EDGE,"E11.7.3"),sQuery(id+"F0.wireOp",EDGE,"E11.7.4"),sQuery(id+"F0.wireOp",EDGE,"E11.7.5"),sQuery(id+"F0.wireOp",EDGE,"E11.7.6"),sQuery(id+"F0.wireOp",EDGE,"E11.7.7"),sQuery(id+"F0.wireOp",EDGE,"E11.7.8"),sQuery(id+"F0.wireOp",EDGE,"E11.7.10"),sQuery(id+"F0.wireOp",EDGE,"E11.7.11"),sQuery(id+"F0.wireOp",EDGE,"E11.8.0"),sQuery(id+"F0.wireOp",EDGE,"E11.8.1"),sQuery(id+"F0.wireOp",EDGE,"E11.8.3"),sQuery(id+"F0.wireOp",EDGE,"E11.8.4"),sQuery(id+"F0.wireOp",EDGE,"E11.8.5"),sQuery(id+"F0.wireOp",EDGE,"E11.8.6"),sQuery(id+"F0.wireOp",EDGE,"E11.8.7"),sQuery(id+"F0.wireOp",EDGE,"E11.8.8"),sQuery(id+"F0.wireOp",EDGE,"E11.8.10"),sQuery(id+"F0.wireOp",EDGE,"E11.8.11"),sQuery(id+"F0.wireOp",EDGE,"E11.9.0"),sQuery(id+"F0.wireOp",EDGE,"E11.9.1"),sQuery(id+"F0.wireOp",EDGE,"E11.9.3"),sQuery(id+"F0.wireOp",EDGE,"E11.9.4"),sQuery(id+"F0.wireOp",EDGE,"E11.9.5"),sQuery(id+"F0.wireOp",EDGE,"E11.9.6"),sQuery(id+"F0.wireOp",EDGE,"E11.9.7"),sQuery(id+"F0.wireOp",EDGE,"E11.9.8"),sQuery(id+"F0.wireOp",EDGE,"E11.9.10"),sQuery(id+"F0.wireOp",EDGE,"E11.9.11"),sQuery(id+"F0.wireOp",EDGE,"E11.10.0"),sQuery(id+"F0.wireOp",EDGE,"E11.10.1"),sQuery(id+"F0.wireOp",EDGE,"E11.10.3"),sQuery(id+"F0.wireOp",EDGE,"E11.10.4"),sQuery(id+"F0.wireOp",EDGE,"E11.10.5"),sQuery(id+"F0.wireOp",EDGE,"E11.10.6"),sQuery(id+"F0.wireOp",EDGE,"E11.10.7"),sQuery(id+"F0.wireOp",EDGE,"E11.10.8"),sQuery(id+"F0.wireOp",EDGE,"E11.10.10"),sQuery(id+"F0.wireOp",EDGE,"E11.10.11"),sQuery(id+"F0.wireOp",EDGE,"E11.11.0"),sQuery(id+"F0.wireOp",EDGE,"E11.11.1"),sQuery(id+"F0.wireOp",EDGE,"E11.11.3"),sQuery(id+"F0.wireOp",EDGE,"E11.11.4"),sQuery(id+"F0.wireOp",EDGE,"E11.11.5"),sQuery(id+"F0.wireOp",EDGE,"E11.11.6"),sQuery(id+"F0.wireOp",EDGE,"E11.11.7"),sQuery(id+"F0.wireOp",EDGE,"E11.11.8"),sQuery(id+"F0.wireOp",EDGE,"E11.11.10"),sQuery(id+"F0.wireOp",EDGE,"E11.11.11"),sQuery(id+"F0.wireOp",EDGE,"E11.12.0"),sQuery(id+"F0.wireOp",EDGE,"E11.12.1"),sQuery(id+"F0.wireOp",EDGE,"E11.12.3"),sQuery(id+"F0.wireOp",EDGE,"E11.12.4"),sQuery(id+"F0.wireOp",EDGE,"E11.12.5"),sQuery(id+"F0.wireOp",EDGE,"E11.12.6"),sQuery(id+"F0.wireOp",EDGE,"E11.12.7"),sQuery(id+"F0.wireOp",EDGE,"E11.12.8"),sQuery(id+"F0.wireOp",EDGE,"E11.12.10"),sQuery(id+"F0.wireOp",EDGE,"E11.12.11"),sQuery(id+"F0.wireOp",EDGE,"E11.13.0"),sQuery(id+"F0.wireOp",EDGE,"E11.13.1"),sQuery(id+"F0.wireOp",EDGE,"E11.13.3"),sQuery(id+"F0.wireOp",EDGE,"E11.13.4"),sQuery(id+"F0.wireOp",EDGE,"E11.13.5"),sQuery(id+"F0.wireOp",EDGE,"E11.13.6"),sQuery(id+"F0.wireOp",EDGE,"E11.13.7"),sQuery(id+"F0.wireOp",EDGE,"E11.13.8"),sQuery(id+"F0.wireOp",EDGE,"E11.13.10"),sQuery(id+"F0.wireOp",EDGE,"E11.13.11"),sQuery(id+"F0.wireOp",EDGE,"E11.14.0"),sQuery(id+"F0.wireOp",EDGE,"E11.14.1"),sQuery(id+"F0.wireOp",EDGE,"E11.14.3"),sQuery(id+"F0.wireOp",EDGE,"E11.14.4"),sQuery(id+"F0.wireOp",EDGE,"E11.14.5"),sQuery(id+"F0.wireOp",EDGE,"E11.14.6"),sQuery(id+"F0.wireOp",EDGE,"E11.14.7"),sQuery(id+"F0.wireOp",EDGE,"E11.14.8"),sQuery(id+"F0.wireOp",EDGE,"E11.14.10"),sQuery(id+"F0.wireOp",EDGE,"E11.14.11"),sQuery(id+"F0.wireOp",EDGE,"E11.15.0"),sQuery(id+"F0.wireOp",EDGE,"E11.15.1"),sQuery(id+"F0.wireOp",EDGE,"E11.15.3"),sQuery(id+"F0.wireOp",EDGE,"E11.15.4"),sQuery(id+"F0.wireOp",EDGE,"E11.15.5"),sQuery(id+"F0.wireOp",EDGE,"E11.15.6"),sQuery(id+"F0.wireOp",EDGE,"E11.15.7"),sQuery(id+"F0.wireOp",EDGE,"E11.15.8"),sQuery(id+"F0.wireOp",EDGE,"E11.15.10"),sQuery(id+"F0.wireOp",EDGE,"E11.15.11"),sQuery(id+"F0.wireOp",EDGE,"E11.16.0"),sQuery(id+"F0.wireOp",EDGE,"E11.16.1"),sQuery(id+"F0.wireOp",EDGE,"E11.16.3"),sQuery(id+"F0.wireOp",EDGE,"E11.16.4"),sQuery(id+"F0.wireOp",EDGE,"E11.16.5"),sQuery(id+"F0.wireOp",EDGE,"E11.16.6"),sQuery(id+"F0.wireOp",EDGE,"E11.16.7"),sQuery(id+"F0.wireOp",EDGE,"E11.16.8"),sQuery(id+"F0.wireOp",EDGE,"E11.16.10"),sQuery(id+"F0.wireOp",EDGE,"E11.16.11"),sQuery(id+"F0.wireOp",EDGE,"E11.17.0"),sQuery(id+"F0.wireOp",EDGE,"E11.17.1"),sQuery(id+"F0.wireOp",EDGE,"E11.17.3"),sQuery(id+"F0.wireOp",EDGE,"E11.17.4"),sQuery(id+"F0.wireOp",EDGE,"E11.17.5"),sQuery(id+"F0.wireOp",EDGE,"E11.17.6"),sQuery(id+"F0.wireOp",EDGE,"E11.17.7"),sQuery(id+"F0.wireOp",EDGE,"E11.17.8"),sQuery(id+"F0.wireOp",EDGE,"E11.17.10"),sQuery(id+"F0.wireOp",EDGE,"E11.17.11"),sQuery(id+"F0.wireOp",EDGE,"E11.18.0"),sQuery(id+"F0.wireOp",EDGE,"E11.18.1"),sQuery(id+"F0.wireOp",EDGE,"E11.18.3"),sQuery(id+"F0.wireOp",EDGE,"E11.18.4"),sQuery(id+"F0.wireOp",EDGE,"E11.18.5"),sQuery(id+"F0.wireOp",EDGE,"E11.18.6"),sQuery(id+"F0.wireOp",EDGE,"E11.18.7"),sQuery(id+"F0.wireOp",EDGE,"E11.18.8"),sQuery(id+"F0.wireOp",EDGE,"E11.18.10"),sQuery(id+"F0.wireOp",EDGE,"E11.18.11"),sQuery(id+"F0.wireOp",EDGE,"E11.19.0"),sQuery(id+"F0.wireOp",EDGE,"E11.19.1"),sQuery(id+"F0.wireOp",EDGE,"E11.19.3"),sQuery(id+"F0.wireOp",EDGE,"E11.19.4"),sQuery(id+"F0.wireOp",EDGE,"E11.19.5"),sQuery(id+"F0.wireOp",EDGE,"E11.19.6"),sQuery(id+"F0.wireOp",EDGE,"E11.19.7"),sQuery(id+"F0.wireOp",EDGE,"E11.19.8"),sQuery(id+"F0.wireOp",EDGE,"E11.19.10"),sQuery(id+"F0.wireOp",EDGE,"E11.19.11"),sQuery(id+"F0.wireOp",EDGE,"E11.20.0"),sQuery(id+"F0.wireOp",EDGE,"E11.20.1"),sQuery(id+"F0.wireOp",EDGE,"E11.20.3"),sQuery(id+"F0.wireOp",EDGE,"E11.20.4"),sQuery(id+"F0.wireOp",EDGE,"E11.20.5"),sQuery(id+"F0.wireOp",EDGE,"E11.20.6"),sQuery(id+"F0.wireOp",EDGE,"E11.20.7"),sQuery(id+"F0.wireOp",EDGE,"E11.20.8"),sQuery(id+"F0.wireOp",EDGE,"E11.20.10"),sQuery(id+"F0.wireOp",EDGE,"E11.20.11"),sQuery(id+"F0.wireOp",EDGE,"E11.21.0"),sQuery(id+"F0.wireOp",EDGE,"E11.21.1"),sQuery(id+"F0.wireOp",EDGE,"E11.21.3"),sQuery(id+"F0.wireOp",EDGE,"E11.21.4"),sQuery(id+"F0.wireOp",EDGE,"E11.21.5"),sQuery(id+"F0.wireOp",EDGE,"E11.21.6"),sQuery(id+"F0.wireOp",EDGE,"E11.21.7"),sQuery(id+"F0.wireOp",EDGE,"E11.21.8"),sQuery(id+"F0.wireOp",EDGE,"E11.21.10"),sQuery(id+"F0.wireOp",EDGE,"E11.21.11"),sQuery(id+"F0.wireOp",EDGE,"E11.22.0"),sQuery(id+"F0.wireOp",EDGE,"E11.22.1"),sQuery(id+"F0.wireOp",EDGE,"E11.22.3"),sQuery(id+"F0.wireOp",EDGE,"E11.22.4"),sQuery(id+"F0.wireOp",EDGE,"E11.22.5"),sQuery(id+"F0.wireOp",EDGE,"E11.22.6"),sQuery(id+"F0.wireOp",EDGE,"E11.22.7"),sQuery(id+"F0.wireOp",EDGE,"E11.22.8"),sQuery(id+"F0.wireOp",EDGE,"E11.22.10"),sQuery(id+"F0.wireOp",EDGE,"E11.22.11"),sQuery(id+"F0.wireOp",EDGE,"E11.23.0"),sQuery(id+"F0.wireOp",EDGE,"E11.23.1"),sQuery(id+"F0.wireOp",EDGE,"E11.23.3"),sQuery(id+"F0.wireOp",EDGE,"E11.23.4"),sQuery(id+"F0.wireOp",EDGE,"E11.23.5"),sQuery(id+"F0.wireOp",EDGE,"E11.23.6"),sQuery(id+"F0.wireOp",EDGE,"E11.23.7"),sQuery(id+"F0.wireOp",EDGE,"E11.23.8"),sQuery(id+"F0.wireOp",EDGE,"E11.23.10"),sQuery(id+"F0.wireOp",EDGE,"E11.23.11"),sQuery(id+"F0.wireOp",EDGE,"E11.24.0"),sQuery(id+"F0.wireOp",EDGE,"E11.24.1"),sQuery(id+"F0.wireOp",EDGE,"E11.24.3"),sQuery(id+"F0.wireOp",EDGE,"E11.24.4"),sQuery(id+"F0.wireOp",EDGE,"E11.24.5"),sQuery(id+"F0.wireOp",EDGE,"E11.24.6"),sQuery(id+"F0.wireOp",EDGE,"E11.24.7"),sQuery(id+"F0.wireOp",EDGE,"E11.24.8"),sQuery(id+"F0.wireOp",EDGE,"E11.24.10"),sQuery(id+"F0.wireOp",EDGE,"E11.24.11"),sQuery(id+"F0.wireOp",EDGE,"E11.25.0"),sQuery(id+"F0.wireOp",EDGE,"E11.25.1"),sQuery(id+"F0.wireOp",EDGE,"E11.25.3"),sQuery(id+"F0.wireOp",EDGE,"E11.25.4"),sQuery(id+"F0.wireOp",EDGE,"E11.25.5"),sQuery(id+"F0.wireOp",EDGE,"E11.25.6"),sQuery(id+"F0.wireOp",EDGE,"E11.25.7"),sQuery(id+"F0.wireOp",EDGE,"E11.25.8"),sQuery(id+"F0.wireOp",EDGE,"E11.25.10"),sQuery(id+"F0.wireOp",EDGE,"E11.25.11"),sQuery(id+"F0.wireOp",EDGE,"E11.26.0"),sQuery(id+"F0.wireOp",EDGE,"E11.26.1"),sQuery(id+"F0.wireOp",EDGE,"E11.26.3"),sQuery(id+"F0.wireOp",EDGE,"E11.26.4"),sQuery(id+"F0.wireOp",EDGE,"E11.26.5"),sQuery(id+"F0.wireOp",EDGE,"E11.26.6"),sQuery(id+"F0.wireOp",EDGE,"E11.26.7"),sQuery(id+"F0.wireOp",EDGE,"E11.26.8"),sQuery(id+"F0.wireOp",EDGE,"E11.26.10"),sQuery(id+"F0.wireOp",EDGE,"E11.26.11"),sQuery(id+"F0.wireOp",EDGE,"E11.27.0"),sQuery(id+"F0.wireOp",EDGE,"E11.27.1"),sQuery(id+"F0.wireOp",EDGE,"E11.27.3"),sQuery(id+"F0.wireOp",EDGE,"E11.27.4"),sQuery(id+"F0.wireOp",EDGE,"E11.27.5"),sQuery(id+"F0.wireOp",EDGE,"E11.27.6"),sQuery(id+"F0.wireOp",EDGE,"E11.27.7"),sQuery(id+"F0.wireOp",EDGE,"E11.27.8"),sQuery(id+"F0.wireOp",EDGE,"E11.27.10"),sQuery(id+"F0.wireOp",EDGE,"E11.27.11"),sQuery(id+"F0.wireOp",EDGE,"E11.28.0"),sQuery(id+"F0.wireOp",EDGE,"E11.28.1"),sQuery(id+"F0.wireOp",EDGE,"E11.28.3"),sQuery(id+"F0.wireOp",EDGE,"E11.28.4"),sQuery(id+"F0.wireOp",EDGE,"E11.28.5"),sQuery(id+"F0.wireOp",EDGE,"E11.28.6"),sQuery(id+"F0.wireOp",EDGE,"E11.28.7"),sQuery(id+"F0.wireOp",EDGE,"E11.28.8"),sQuery(id+"F0.wireOp",EDGE,"E11.28.10"),sQuery(id+"F0.wireOp",EDGE,"E11.28.11"),sQuery(id+"F0.wireOp",EDGE,"E11.29.0"),sQuery(id+"F0.wireOp",EDGE,"E11.29.1"),sQuery(id+"F0.wireOp",EDGE,"E11.29.3"),sQuery(id+"F0.wireOp",EDGE,"E11.29.4"),sQuery(id+"F0.wireOp",EDGE,"E11.29.5"),sQuery(id+"F0.wireOp",EDGE,"E11.29.6"),sQuery(id+"F0.wireOp",EDGE,"E11.29.7"),sQuery(id+"F0.wireOp",EDGE,"E11.29.8"),sQuery(id+"F0.wireOp",EDGE,"E11.29.10"),sQuery(id+"F0.wireOp",EDGE,"E11.29.11"),sQuery(id+"F0.wireOp",EDGE,"E11.30.0"),sQuery(id+"F0.wireOp",EDGE,"E11.30.1"),sQuery(id+"F0.wireOp",EDGE,"E11.30.3"),sQuery(id+"F0.wireOp",EDGE,"E11.30.4"),sQuery(id+"F0.wireOp",EDGE,"E11.30.5"),sQuery(id+"F0.wireOp",EDGE,"E11.30.6"),sQuery(id+"F0.wireOp",EDGE,"E11.30.7"),sQuery(id+"F0.wireOp",EDGE,"E11.30.8"),sQuery(id+"F0.wireOp",EDGE,"E11.30.10"),sQuery(id+"F0.wireOp",EDGE,"E11.30.11"),sQuery(id+"F0.wireOp",EDGE,"E11.31.0"),sQuery(id+"F0.wireOp",EDGE,"E11.31.1"),sQuery(id+"F0.wireOp",EDGE,"E11.31.3"),sQuery(id+"F0.wireOp",EDGE,"E11.31.4"),sQuery(id+"F0.wireOp",EDGE,"E11.31.5"),sQuery(id+"F0.wireOp",EDGE,"E11.31.6"),sQuery(id+"F0.wireOp",EDGE,"E11.31.7"),sQuery(id+"F0.wireOp",EDGE,"E11.31.8"),sQuery(id+"F0.wireOp",EDGE,"E11.31.10"),sQuery(id+"F0.wireOp",EDGE,"E11.31.11"),sQuery(id+"F0.wireOp",EDGE,"E11.32.0"),sQuery(id+"F0.wireOp",EDGE,"E11.32.1"),sQuery(id+"F0.wireOp",EDGE,"E11.32.3"),sQuery(id+"F0.wireOp",EDGE,"E11.32.4"),sQuery(id+"F0.wireOp",EDGE,"E11.32.5"),sQuery(id+"F0.wireOp",EDGE,"E11.32.6"),sQuery(id+"F0.wireOp",EDGE,"E11.32.7"),sQuery(id+"F0.wireOp",EDGE,"E11.32.8"),sQuery(id+"F0.wireOp",EDGE,"E11.32.10"),sQuery(id+"F0.wireOp",EDGE,"E11.32.11"),sQuery(id+"F0.wireOp",EDGE,"E11.33.0"),sQuery(id+"F0.wireOp",EDGE,"E11.33.1"),sQuery(id+"F0.wireOp",EDGE,"E11.33.3"),sQuery(id+"F0.wireOp",EDGE,"E11.33.4"),sQuery(id+"F0.wireOp",EDGE,"E11.33.5"),sQuery(id+"F0.wireOp",EDGE,"E11.33.6"),sQuery(id+"F0.wireOp",EDGE,"E11.33.7"),sQuery(id+"F0.wireOp",EDGE,"E11.33.8"),sQuery(id+"F0.wireOp",EDGE,"E11.33.10"),sQuery(id+"F0.wireOp",EDGE,"E11.33.11"),sQuery(id+"F0.wireOp",EDGE,"E11.34.0"),sQuery(id+"F0.wireOp",EDGE,"E11.34.1"),sQuery(id+"F0.wireOp",EDGE,"E11.34.3"),sQuery(id+"F0.wireOp",EDGE,"E11.34.4"),sQuery(id+"F0.wireOp",EDGE,"E11.34.5"),sQuery(id+"F0.wireOp",EDGE,"E11.34.6"),sQuery(id+"F0.wireOp",EDGE,"E11.34.7"),sQuery(id+"F0.wireOp",EDGE,"E11.34.8"),sQuery(id+"F0.wireOp",EDGE,"E11.34.10"),sQuery(id+"F0.wireOp",EDGE,"E11.34.11"),sQuery(id+"F0.wireOp",EDGE,"E11.35.0"),sQuery(id+"F0.wireOp",EDGE,"E11.35.1"),sQuery(id+"F0.wireOp",EDGE,"E11.35.3"),sQuery(id+"F0.wireOp",EDGE,"E11.35.4"),sQuery(id+"F0.wireOp",EDGE,"E11.35.5"),sQuery(id+"F0.wireOp",EDGE,"E11.35.6"),sQuery(id+"F0.wireOp",EDGE,"E11.35.7"),sQuery(id+"F0.wireOp",EDGE,"E11.35.8"),sQuery(id+"F0.wireOp",EDGE,"E11.35.10"),sQuery(id+"F0.wireOp",EDGE,"E11.35.11"),sQuery(id+"F0.wireOp",EDGE,"E12.trimOffspring"),sQuery(id+"F0.wireOp",EDGE,"E13.trimOffspring"),sQuery(id+"F0.wireOp",EDGE,"E14.trimOffspring"),sQuery(id+"F0.wireOp",EDGE,"E15.trimOffspring"),sQuery(id+"F0.wireOp",EDGE,"E16.trimOffspring"),sQuery(id+"F0.wireOp",EDGE,"E17.trimOffspring"),sQuery(id+"F0.wireOp",EDGE,"E18.trimOffspring"),sQuery(id+"F0.wireOp",EDGE,"E19.trimOffspring"),sQuery(id+"F0.wireOp",EDGE,"E20.trimOffspring"),sQuery(id+"F0.wireOp",EDGE,"E21.trimOffspring"),sQuery(id+"F0.wireOp",EDGE,"E22.trimOffspring"),sQuery(id+"F0.wireOp",EDGE,"E23.trimOffspring"),sQuery(id+"F0.wireOp",EDGE,"E24.trimOffspring"),sQuery(id+"F0.wireOp",EDGE,"E25.trimOffspring"),sQuery(id+"F0.wireOp",EDGE,"E26.trimOffspring"),sQuery(id+"F0.wireOp",EDGE,"E27.trimOffspring"),sQuery(id+"F0.wireOp",EDGE,"E28.trimOffspring"),sQuery(id+"F0.wireOp",EDGE,"E29.trimOffspring"),sQuery(id+"F0.wireOp",EDGE,"E30.trimOffspring"),sQuery(id+"F0.wireOp",EDGE,"E31.trimOffspring"),sQuery(id+"F0.wireOp",EDGE,"E32.trimOffspring"),sQuery(id+"F0.wireOp",EDGE,"E33.trimOffspring"),sQuery(id+"F0.wireOp",EDGE,"E34.trimOffspring"),sQuery(id+"F0.wireOp",EDGE,"E35.trimOffspring"),sQuery(id+"F0.wireOp",EDGE,"E36.trimOffspring"),sQuery(id+"F0.wireOp",EDGE,"E37.trimOffspring"),sQuery(id+"F0.wireOp",EDGE,"E38.trimOffspring"),sQuery(id+"F0.wireOp",EDGE,"E39.trimOffspring"),sQuery(id+"F0.wireOp",EDGE,"E40.trimOffspring"),sQuery(id+"F0.wireOp",EDGE,"E41.trimOffspring"),sQuery(id+"F0.wireOp",EDGE,"E42.trimOffspring"),sQuery(id+"F0.wireOp",EDGE,"E43.trimOffspring"),sQuery(id+"F0.wireOp",EDGE,"E44.trimOffspring"),sQuery(id+"F0.wireOp",EDGE,"E45.trimOffspring"),sQuery(id+"F0.wireOp",EDGE,"E46.trimOffspring")])]});
            hole(context, id + "F6", {"style" : HoleStyle.SIMPLE, "endStyle" : HoleEndStyle.THROUGH, "holeDiameter" : 1.9 * mm, "locations" : qUnion([Q0, Q1, Q2, Q3]), "scope" : qUnion([Q4]), "isTappedThrough" : true});
        }
        {
            var Q0;
            Q0=makeQuery(id+"F1.opExtrude","CAP_FACE",FACE,{"disambiguationData":[OSD([sQuery(id+"F0.wireOp",EDGE,"E0"),sQuery(id+"F0.wireOp",EDGE,"E1.trimOffspring"),sQuery(id+"F0.wireOp",EDGE,"E2"),sQuery(id+"F0.wireOp",EDGE,"E3"),sQuery(id+"F0.wireOp",EDGE,"E4.MirrorCS"),sQuery(id+"F0.wireOp",EDGE,"E5.MirrorCS"),sQuery(id+"F0.wireOp",EDGE,"E6.MirrorCS"),sQuery(id+"F0.wireOp",EDGE,"E7.filletArc"),sQuery(id+"F0.wireOp",EDGE,"E8.filletArc"),sQuery(id+"F0.wireOp",EDGE,"E9.filletArc"),sQuery(id+"F0.wireOp",EDGE,"E10.filletArc"),sQuery(id+"F0.wireOp",EDGE,"E11.1.0"),sQuery(id+"F0.wireOp",EDGE,"E11.1.1"),sQuery(id+"F0.wireOp",EDGE,"E11.1.3"),sQuery(id+"F0.wireOp",EDGE,"E11.1.4"),sQuery(id+"F0.wireOp",EDGE,"E11.1.5"),sQuery(id+"F0.wireOp",EDGE,"E11.1.6"),sQuery(id+"F0.wireOp",EDGE,"E11.1.7"),sQuery(id+"F0.wireOp",EDGE,"E11.1.8"),sQuery(id+"F0.wireOp",EDGE,"E11.1.10"),sQuery(id+"F0.wireOp",EDGE,"E11.1.11"),sQuery(id+"F0.wireOp",EDGE,"E11.2.0"),sQuery(id+"F0.wireOp",EDGE,"E11.2.1"),sQuery(id+"F0.wireOp",EDGE,"E11.2.3"),sQuery(id+"F0.wireOp",EDGE,"E11.2.4"),sQuery(id+"F0.wireOp",EDGE,"E11.2.5"),sQuery(id+"F0.wireOp",EDGE,"E11.2.6"),sQuery(id+"F0.wireOp",EDGE,"E11.2.7"),sQuery(id+"F0.wireOp",EDGE,"E11.2.8"),sQuery(id+"F0.wireOp",EDGE,"E11.2.10"),sQuery(id+"F0.wireOp",EDGE,"E11.2.11"),sQuery(id+"F0.wireOp",EDGE,"E11.3.0"),sQuery(id+"F0.wireOp",EDGE,"E11.3.1"),sQuery(id+"F0.wireOp",EDGE,"E11.3.3"),sQuery(id+"F0.wireOp",EDGE,"E11.3.4"),sQuery(id+"F0.wireOp",EDGE,"E11.3.5"),sQuery(id+"F0.wireOp",EDGE,"E11.3.6"),sQuery(id+"F0.wireOp",EDGE,"E11.3.7"),sQuery(id+"F0.wireOp",EDGE,"E11.3.8"),sQuery(id+"F0.wireOp",EDGE,"E11.3.10"),sQuery(id+"F0.wireOp",EDGE,"E11.3.11"),sQuery(id+"F0.wireOp",EDGE,"E11.4.0"),sQuery(id+"F0.wireOp",EDGE,"E11.4.1"),sQuery(id+"F0.wireOp",EDGE,"E11.4.3"),sQuery(id+"F0.wireOp",EDGE,"E11.4.4"),sQuery(id+"F0.wireOp",EDGE,"E11.4.5"),sQuery(id+"F0.wireOp",EDGE,"E11.4.6"),sQuery(id+"F0.wireOp",EDGE,"E11.4.7"),sQuery(id+"F0.wireOp",EDGE,"E11.4.8"),sQuery(id+"F0.wireOp",EDGE,"E11.4.10"),sQuery(id+"F0.wireOp",EDGE,"E11.4.11"),sQuery(id+"F0.wireOp",EDGE,"E11.5.0"),sQuery(id+"F0.wireOp",EDGE,"E11.5.1"),sQuery(id+"F0.wireOp",EDGE,"E11.5.3"),sQuery(id+"F0.wireOp",EDGE,"E11.5.4"),sQuery(id+"F0.wireOp",EDGE,"E11.5.5"),sQuery(id+"F0.wireOp",EDGE,"E11.5.6"),sQuery(id+"F0.wireOp",EDGE,"E11.5.7"),sQuery(id+"F0.wireOp",EDGE,"E11.5.8"),sQuery(id+"F0.wireOp",EDGE,"E11.5.10"),sQuery(id+"F0.wireOp",EDGE,"E11.5.11"),sQuery(id+"F0.wireOp",EDGE,"E11.6.0"),sQuery(id+"F0.wireOp",EDGE,"E11.6.1"),sQuery(id+"F0.wireOp",EDGE,"E11.6.3"),sQuery(id+"F0.wireOp",EDGE,"E11.6.4"),sQuery(id+"F0.wireOp",EDGE,"E11.6.5"),sQuery(id+"F0.wireOp",EDGE,"E11.6.6"),sQuery(id+"F0.wireOp",EDGE,"E11.6.7"),sQuery(id+"F0.wireOp",EDGE,"E11.6.8"),sQuery(id+"F0.wireOp",EDGE,"E11.6.10"),sQuery(id+"F0.wireOp",EDGE,"E11.6.11"),sQuery(id+"F0.wireOp",EDGE,"E11.7.0"),sQuery(id+"F0.wireOp",EDGE,"E11.7.1"),sQuery(id+"F0.wireOp",EDGE,"E11.7.3"),sQuery(id+"F0.wireOp",EDGE,"E11.7.4"),sQuery(id+"F0.wireOp",EDGE,"E11.7.5"),sQuery(id+"F0.wireOp",EDGE,"E11.7.6"),sQuery(id+"F0.wireOp",EDGE,"E11.7.7"),sQuery(id+"F0.wireOp",EDGE,"E11.7.8"),sQuery(id+"F0.wireOp",EDGE,"E11.7.10"),sQuery(id+"F0.wireOp",EDGE,"E11.7.11"),sQuery(id+"F0.wireOp",EDGE,"E11.8.0"),sQuery(id+"F0.wireOp",EDGE,"E11.8.1"),sQuery(id+"F0.wireOp",EDGE,"E11.8.3"),sQuery(id+"F0.wireOp",EDGE,"E11.8.4"),sQuery(id+"F0.wireOp",EDGE,"E11.8.5"),sQuery(id+"F0.wireOp",EDGE,"E11.8.6"),sQuery(id+"F0.wireOp",EDGE,"E11.8.7"),sQuery(id+"F0.wireOp",EDGE,"E11.8.8"),sQuery(id+"F0.wireOp",EDGE,"E11.8.10"),sQuery(id+"F0.wireOp",EDGE,"E11.8.11"),sQuery(id+"F0.wireOp",EDGE,"E11.9.0"),sQuery(id+"F0.wireOp",EDGE,"E11.9.1"),sQuery(id+"F0.wireOp",EDGE,"E11.9.3"),sQuery(id+"F0.wireOp",EDGE,"E11.9.4"),sQuery(id+"F0.wireOp",EDGE,"E11.9.5"),sQuery(id+"F0.wireOp",EDGE,"E11.9.6"),sQuery(id+"F0.wireOp",EDGE,"E11.9.7"),sQuery(id+"F0.wireOp",EDGE,"E11.9.8"),sQuery(id+"F0.wireOp",EDGE,"E11.9.10"),sQuery(id+"F0.wireOp",EDGE,"E11.9.11"),sQuery(id+"F0.wireOp",EDGE,"E11.10.0"),sQuery(id+"F0.wireOp",EDGE,"E11.10.1"),sQuery(id+"F0.wireOp",EDGE,"E11.10.3"),sQuery(id+"F0.wireOp",EDGE,"E11.10.4"),sQuery(id+"F0.wireOp",EDGE,"E11.10.5"),sQuery(id+"F0.wireOp",EDGE,"E11.10.6"),sQuery(id+"F0.wireOp",EDGE,"E11.10.7"),sQuery(id+"F0.wireOp",EDGE,"E11.10.8"),sQuery(id+"F0.wireOp",EDGE,"E11.10.10"),sQuery(id+"F0.wireOp",EDGE,"E11.10.11"),sQuery(id+"F0.wireOp",EDGE,"E11.11.0"),sQuery(id+"F0.wireOp",EDGE,"E11.11.1"),sQuery(id+"F0.wireOp",EDGE,"E11.11.3"),sQuery(id+"F0.wireOp",EDGE,"E11.11.4"),sQuery(id+"F0.wireOp",EDGE,"E11.11.5"),sQuery(id+"F0.wireOp",EDGE,"E11.11.6"),sQuery(id+"F0.wireOp",EDGE,"E11.11.7"),sQuery(id+"F0.wireOp",EDGE,"E11.11.8"),sQuery(id+"F0.wireOp",EDGE,"E11.11.10"),sQuery(id+"F0.wireOp",EDGE,"E11.11.11"),sQuery(id+"F0.wireOp",EDGE,"E11.12.0"),sQuery(id+"F0.wireOp",EDGE,"E11.12.1"),sQuery(id+"F0.wireOp",EDGE,"E11.12.3"),sQuery(id+"F0.wireOp",EDGE,"E11.12.4"),sQuery(id+"F0.wireOp",EDGE,"E11.12.5"),sQuery(id+"F0.wireOp",EDGE,"E11.12.6"),sQuery(id+"F0.wireOp",EDGE,"E11.12.7"),sQuery(id+"F0.wireOp",EDGE,"E11.12.8"),sQuery(id+"F0.wireOp",EDGE,"E11.12.10"),sQuery(id+"F0.wireOp",EDGE,"E11.12.11"),sQuery(id+"F0.wireOp",EDGE,"E11.13.0"),sQuery(id+"F0.wireOp",EDGE,"E11.13.1"),sQuery(id+"F0.wireOp",EDGE,"E11.13.3"),sQuery(id+"F0.wireOp",EDGE,"E11.13.4"),sQuery(id+"F0.wireOp",EDGE,"E11.13.5"),sQuery(id+"F0.wireOp",EDGE,"E11.13.6"),sQuery(id+"F0.wireOp",EDGE,"E11.13.7"),sQuery(id+"F0.wireOp",EDGE,"E11.13.8"),sQuery(id+"F0.wireOp",EDGE,"E11.13.10"),sQuery(id+"F0.wireOp",EDGE,"E11.13.11"),sQuery(id+"F0.wireOp",EDGE,"E11.14.0"),sQuery(id+"F0.wireOp",EDGE,"E11.14.1"),sQuery(id+"F0.wireOp",EDGE,"E11.14.3"),sQuery(id+"F0.wireOp",EDGE,"E11.14.4"),sQuery(id+"F0.wireOp",EDGE,"E11.14.5"),sQuery(id+"F0.wireOp",EDGE,"E11.14.6"),sQuery(id+"F0.wireOp",EDGE,"E11.14.7"),sQuery(id+"F0.wireOp",EDGE,"E11.14.8"),sQuery(id+"F0.wireOp",EDGE,"E11.14.10"),sQuery(id+"F0.wireOp",EDGE,"E11.14.11"),sQuery(id+"F0.wireOp",EDGE,"E11.15.0"),sQuery(id+"F0.wireOp",EDGE,"E11.15.1"),sQuery(id+"F0.wireOp",EDGE,"E11.15.3"),sQuery(id+"F0.wireOp",EDGE,"E11.15.4"),sQuery(id+"F0.wireOp",EDGE,"E11.15.5"),sQuery(id+"F0.wireOp",EDGE,"E11.15.6"),sQuery(id+"F0.wireOp",EDGE,"E11.15.7"),sQuery(id+"F0.wireOp",EDGE,"E11.15.8"),sQuery(id+"F0.wireOp",EDGE,"E11.15.10"),sQuery(id+"F0.wireOp",EDGE,"E11.15.11"),sQuery(id+"F0.wireOp",EDGE,"E11.16.0"),sQuery(id+"F0.wireOp",EDGE,"E11.16.1"),sQuery(id+"F0.wireOp",EDGE,"E11.16.3"),sQuery(id+"F0.wireOp",EDGE,"E11.16.4"),sQuery(id+"F0.wireOp",EDGE,"E11.16.5"),sQuery(id+"F0.wireOp",EDGE,"E11.16.6"),sQuery(id+"F0.wireOp",EDGE,"E11.16.7"),sQuery(id+"F0.wireOp",EDGE,"E11.16.8"),sQuery(id+"F0.wireOp",EDGE,"E11.16.10"),sQuery(id+"F0.wireOp",EDGE,"E11.16.11"),sQuery(id+"F0.wireOp",EDGE,"E11.17.0"),sQuery(id+"F0.wireOp",EDGE,"E11.17.1"),sQuery(id+"F0.wireOp",EDGE,"E11.17.3"),sQuery(id+"F0.wireOp",EDGE,"E11.17.4"),sQuery(id+"F0.wireOp",EDGE,"E11.17.5"),sQuery(id+"F0.wireOp",EDGE,"E11.17.6"),sQuery(id+"F0.wireOp",EDGE,"E11.17.7"),sQuery(id+"F0.wireOp",EDGE,"E11.17.8"),sQuery(id+"F0.wireOp",EDGE,"E11.17.10"),sQuery(id+"F0.wireOp",EDGE,"E11.17.11"),sQuery(id+"F0.wireOp",EDGE,"E11.18.0"),sQuery(id+"F0.wireOp",EDGE,"E11.18.1"),sQuery(id+"F0.wireOp",EDGE,"E11.18.3"),sQuery(id+"F0.wireOp",EDGE,"E11.18.4"),sQuery(id+"F0.wireOp",EDGE,"E11.18.5"),sQuery(id+"F0.wireOp",EDGE,"E11.18.6"),sQuery(id+"F0.wireOp",EDGE,"E11.18.7"),sQuery(id+"F0.wireOp",EDGE,"E11.18.8"),sQuery(id+"F0.wireOp",EDGE,"E11.18.10"),sQuery(id+"F0.wireOp",EDGE,"E11.18.11"),sQuery(id+"F0.wireOp",EDGE,"E11.19.0"),sQuery(id+"F0.wireOp",EDGE,"E11.19.1"),sQuery(id+"F0.wireOp",EDGE,"E11.19.3"),sQuery(id+"F0.wireOp",EDGE,"E11.19.4"),sQuery(id+"F0.wireOp",EDGE,"E11.19.5"),sQuery(id+"F0.wireOp",EDGE,"E11.19.6"),sQuery(id+"F0.wireOp",EDGE,"E11.19.7"),sQuery(id+"F0.wireOp",EDGE,"E11.19.8"),sQuery(id+"F0.wireOp",EDGE,"E11.19.10"),sQuery(id+"F0.wireOp",EDGE,"E11.19.11"),sQuery(id+"F0.wireOp",EDGE,"E11.20.0"),sQuery(id+"F0.wireOp",EDGE,"E11.20.1"),sQuery(id+"F0.wireOp",EDGE,"E11.20.3"),sQuery(id+"F0.wireOp",EDGE,"E11.20.4"),sQuery(id+"F0.wireOp",EDGE,"E11.20.5"),sQuery(id+"F0.wireOp",EDGE,"E11.20.6"),sQuery(id+"F0.wireOp",EDGE,"E11.20.7"),sQuery(id+"F0.wireOp",EDGE,"E11.20.8"),sQuery(id+"F0.wireOp",EDGE,"E11.20.10"),sQuery(id+"F0.wireOp",EDGE,"E11.20.11"),sQuery(id+"F0.wireOp",EDGE,"E11.21.0"),sQuery(id+"F0.wireOp",EDGE,"E11.21.1"),sQuery(id+"F0.wireOp",EDGE,"E11.21.3"),sQuery(id+"F0.wireOp",EDGE,"E11.21.4"),sQuery(id+"F0.wireOp",EDGE,"E11.21.5"),sQuery(id+"F0.wireOp",EDGE,"E11.21.6"),sQuery(id+"F0.wireOp",EDGE,"E11.21.7"),sQuery(id+"F0.wireOp",EDGE,"E11.21.8"),sQuery(id+"F0.wireOp",EDGE,"E11.21.10"),sQuery(id+"F0.wireOp",EDGE,"E11.21.11"),sQuery(id+"F0.wireOp",EDGE,"E11.22.0"),sQuery(id+"F0.wireOp",EDGE,"E11.22.1"),sQuery(id+"F0.wireOp",EDGE,"E11.22.3"),sQuery(id+"F0.wireOp",EDGE,"E11.22.4"),sQuery(id+"F0.wireOp",EDGE,"E11.22.5"),sQuery(id+"F0.wireOp",EDGE,"E11.22.6"),sQuery(id+"F0.wireOp",EDGE,"E11.22.7"),sQuery(id+"F0.wireOp",EDGE,"E11.22.8"),sQuery(id+"F0.wireOp",EDGE,"E11.22.10"),sQuery(id+"F0.wireOp",EDGE,"E11.22.11"),sQuery(id+"F0.wireOp",EDGE,"E11.23.0"),sQuery(id+"F0.wireOp",EDGE,"E11.23.1"),sQuery(id+"F0.wireOp",EDGE,"E11.23.3"),sQuery(id+"F0.wireOp",EDGE,"E11.23.4"),sQuery(id+"F0.wireOp",EDGE,"E11.23.5"),sQuery(id+"F0.wireOp",EDGE,"E11.23.6"),sQuery(id+"F0.wireOp",EDGE,"E11.23.7"),sQuery(id+"F0.wireOp",EDGE,"E11.23.8"),sQuery(id+"F0.wireOp",EDGE,"E11.23.10"),sQuery(id+"F0.wireOp",EDGE,"E11.23.11"),sQuery(id+"F0.wireOp",EDGE,"E11.24.0"),sQuery(id+"F0.wireOp",EDGE,"E11.24.1"),sQuery(id+"F0.wireOp",EDGE,"E11.24.3"),sQuery(id+"F0.wireOp",EDGE,"E11.24.4"),sQuery(id+"F0.wireOp",EDGE,"E11.24.5"),sQuery(id+"F0.wireOp",EDGE,"E11.24.6"),sQuery(id+"F0.wireOp",EDGE,"E11.24.7"),sQuery(id+"F0.wireOp",EDGE,"E11.24.8"),sQuery(id+"F0.wireOp",EDGE,"E11.24.10"),sQuery(id+"F0.wireOp",EDGE,"E11.24.11"),sQuery(id+"F0.wireOp",EDGE,"E11.25.0"),sQuery(id+"F0.wireOp",EDGE,"E11.25.1"),sQuery(id+"F0.wireOp",EDGE,"E11.25.3"),sQuery(id+"F0.wireOp",EDGE,"E11.25.4"),sQuery(id+"F0.wireOp",EDGE,"E11.25.5"),sQuery(id+"F0.wireOp",EDGE,"E11.25.6"),sQuery(id+"F0.wireOp",EDGE,"E11.25.7"),sQuery(id+"F0.wireOp",EDGE,"E11.25.8"),sQuery(id+"F0.wireOp",EDGE,"E11.25.10"),sQuery(id+"F0.wireOp",EDGE,"E11.25.11"),sQuery(id+"F0.wireOp",EDGE,"E11.26.0"),sQuery(id+"F0.wireOp",EDGE,"E11.26.1"),sQuery(id+"F0.wireOp",EDGE,"E11.26.3"),sQuery(id+"F0.wireOp",EDGE,"E11.26.4"),sQuery(id+"F0.wireOp",EDGE,"E11.26.5"),sQuery(id+"F0.wireOp",EDGE,"E11.26.6"),sQuery(id+"F0.wireOp",EDGE,"E11.26.7"),sQuery(id+"F0.wireOp",EDGE,"E11.26.8"),sQuery(id+"F0.wireOp",EDGE,"E11.26.10"),sQuery(id+"F0.wireOp",EDGE,"E11.26.11"),sQuery(id+"F0.wireOp",EDGE,"E11.27.0"),sQuery(id+"F0.wireOp",EDGE,"E11.27.1"),sQuery(id+"F0.wireOp",EDGE,"E11.27.3"),sQuery(id+"F0.wireOp",EDGE,"E11.27.4"),sQuery(id+"F0.wireOp",EDGE,"E11.27.5"),sQuery(id+"F0.wireOp",EDGE,"E11.27.6"),sQuery(id+"F0.wireOp",EDGE,"E11.27.7"),sQuery(id+"F0.wireOp",EDGE,"E11.27.8"),sQuery(id+"F0.wireOp",EDGE,"E11.27.10"),sQuery(id+"F0.wireOp",EDGE,"E11.27.11"),sQuery(id+"F0.wireOp",EDGE,"E11.28.0"),sQuery(id+"F0.wireOp",EDGE,"E11.28.1"),sQuery(id+"F0.wireOp",EDGE,"E11.28.3"),sQuery(id+"F0.wireOp",EDGE,"E11.28.4"),sQuery(id+"F0.wireOp",EDGE,"E11.28.5"),sQuery(id+"F0.wireOp",EDGE,"E11.28.6"),sQuery(id+"F0.wireOp",EDGE,"E11.28.7"),sQuery(id+"F0.wireOp",EDGE,"E11.28.8"),sQuery(id+"F0.wireOp",EDGE,"E11.28.10"),sQuery(id+"F0.wireOp",EDGE,"E11.28.11"),sQuery(id+"F0.wireOp",EDGE,"E11.29.0"),sQuery(id+"F0.wireOp",EDGE,"E11.29.1"),sQuery(id+"F0.wireOp",EDGE,"E11.29.3"),sQuery(id+"F0.wireOp",EDGE,"E11.29.4"),sQuery(id+"F0.wireOp",EDGE,"E11.29.5"),sQuery(id+"F0.wireOp",EDGE,"E11.29.6"),sQuery(id+"F0.wireOp",EDGE,"E11.29.7"),sQuery(id+"F0.wireOp",EDGE,"E11.29.8"),sQuery(id+"F0.wireOp",EDGE,"E11.29.10"),sQuery(id+"F0.wireOp",EDGE,"E11.29.11"),sQuery(id+"F0.wireOp",EDGE,"E11.30.0"),sQuery(id+"F0.wireOp",EDGE,"E11.30.1"),sQuery(id+"F0.wireOp",EDGE,"E11.30.3"),sQuery(id+"F0.wireOp",EDGE,"E11.30.4"),sQuery(id+"F0.wireOp",EDGE,"E11.30.5"),sQuery(id+"F0.wireOp",EDGE,"E11.30.6"),sQuery(id+"F0.wireOp",EDGE,"E11.30.7"),sQuery(id+"F0.wireOp",EDGE,"E11.30.8"),sQuery(id+"F0.wireOp",EDGE,"E11.30.10"),sQuery(id+"F0.wireOp",EDGE,"E11.30.11"),sQuery(id+"F0.wireOp",EDGE,"E11.31.0"),sQuery(id+"F0.wireOp",EDGE,"E11.31.1"),sQuery(id+"F0.wireOp",EDGE,"E11.31.3"),sQuery(id+"F0.wireOp",EDGE,"E11.31.4"),sQuery(id+"F0.wireOp",EDGE,"E11.31.5"),sQuery(id+"F0.wireOp",EDGE,"E11.31.6"),sQuery(id+"F0.wireOp",EDGE,"E11.31.7"),sQuery(id+"F0.wireOp",EDGE,"E11.31.8"),sQuery(id+"F0.wireOp",EDGE,"E11.31.10"),sQuery(id+"F0.wireOp",EDGE,"E11.31.11"),sQuery(id+"F0.wireOp",EDGE,"E11.32.0"),sQuery(id+"F0.wireOp",EDGE,"E11.32.1"),sQuery(id+"F0.wireOp",EDGE,"E11.32.3"),sQuery(id+"F0.wireOp",EDGE,"E11.32.4"),sQuery(id+"F0.wireOp",EDGE,"E11.32.5"),sQuery(id+"F0.wireOp",EDGE,"E11.32.6"),sQuery(id+"F0.wireOp",EDGE,"E11.32.7"),sQuery(id+"F0.wireOp",EDGE,"E11.32.8"),sQuery(id+"F0.wireOp",EDGE,"E11.32.10"),sQuery(id+"F0.wireOp",EDGE,"E11.32.11"),sQuery(id+"F0.wireOp",EDGE,"E11.33.0"),sQuery(id+"F0.wireOp",EDGE,"E11.33.1"),sQuery(id+"F0.wireOp",EDGE,"E11.33.3"),sQuery(id+"F0.wireOp",EDGE,"E11.33.4"),sQuery(id+"F0.wireOp",EDGE,"E11.33.5"),sQuery(id+"F0.wireOp",EDGE,"E11.33.6"),sQuery(id+"F0.wireOp",EDGE,"E11.33.7"),sQuery(id+"F0.wireOp",EDGE,"E11.33.8"),sQuery(id+"F0.wireOp",EDGE,"E11.33.10"),sQuery(id+"F0.wireOp",EDGE,"E11.33.11"),sQuery(id+"F0.wireOp",EDGE,"E11.34.0"),sQuery(id+"F0.wireOp",EDGE,"E11.34.1"),sQuery(id+"F0.wireOp",EDGE,"E11.34.3"),sQuery(id+"F0.wireOp",EDGE,"E11.34.4"),sQuery(id+"F0.wireOp",EDGE,"E11.34.5"),sQuery(id+"F0.wireOp",EDGE,"E11.34.6"),sQuery(id+"F0.wireOp",EDGE,"E11.34.7"),sQuery(id+"F0.wireOp",EDGE,"E11.34.8"),sQuery(id+"F0.wireOp",EDGE,"E11.34.10"),sQuery(id+"F0.wireOp",EDGE,"E11.34.11"),sQuery(id+"F0.wireOp",EDGE,"E11.35.0"),sQuery(id+"F0.wireOp",EDGE,"E11.35.1"),sQuery(id+"F0.wireOp",EDGE,"E11.35.3"),sQuery(id+"F0.wireOp",EDGE,"E11.35.4"),sQuery(id+"F0.wireOp",EDGE,"E11.35.5"),sQuery(id+"F0.wireOp",EDGE,"E11.35.6"),sQuery(id+"F0.wireOp",EDGE,"E11.35.7"),sQuery(id+"F0.wireOp",EDGE,"E11.35.8"),sQuery(id+"F0.wireOp",EDGE,"E11.35.10"),sQuery(id+"F0.wireOp",EDGE,"E11.35.11"),sQuery(id+"F0.wireOp",EDGE,"E12.trimOffspring"),sQuery(id+"F0.wireOp",EDGE,"E13.trimOffspring"),sQuery(id+"F0.wireOp",EDGE,"E14.trimOffspring"),sQuery(id+"F0.wireOp",EDGE,"E15.trimOffspring"),sQuery(id+"F0.wireOp",EDGE,"E16.trimOffspring"),sQuery(id+"F0.wireOp",EDGE,"E17.trimOffspring"),sQuery(id+"F0.wireOp",EDGE,"E18.trimOffspring"),sQuery(id+"F0.wireOp",EDGE,"E19.trimOffspring"),sQuery(id+"F0.wireOp",EDGE,"E20.trimOffspring"),sQuery(id+"F0.wireOp",EDGE,"E21.trimOffspring"),sQuery(id+"F0.wireOp",EDGE,"E22.trimOffspring"),sQuery(id+"F0.wireOp",EDGE,"E23.trimOffspring"),sQuery(id+"F0.wireOp",EDGE,"E24.trimOffspring"),sQuery(id+"F0.wireOp",EDGE,"E25.trimOffspring"),sQuery(id+"F0.wireOp",EDGE,"E26.trimOffspring"),sQuery(id+"F0.wireOp",EDGE,"E27.trimOffspring"),sQuery(id+"F0.wireOp",EDGE,"E28.trimOffspring"),sQuery(id+"F0.wireOp",EDGE,"E29.trimOffspring"),sQuery(id+"F0.wireOp",EDGE,"E30.trimOffspring"),sQuery(id+"F0.wireOp",EDGE,"E31.trimOffspring"),sQuery(id+"F0.wireOp",EDGE,"E32.trimOffspring"),sQuery(id+"F0.wireOp",EDGE,"E33.trimOffspring"),sQuery(id+"F0.wireOp",EDGE,"E34.trimOffspring"),sQuery(id+"F0.wireOp",EDGE,"E35.trimOffspring"),sQuery(id+"F0.wireOp",EDGE,"E36.trimOffspring"),sQuery(id+"F0.wireOp",EDGE,"E37.trimOffspring"),sQuery(id+"F0.wireOp",EDGE,"E38.trimOffspring"),sQuery(id+"F0.wireOp",EDGE,"E39.trimOffspring"),sQuery(id+"F0.wireOp",EDGE,"E40.trimOffspring"),sQuery(id+"F0.wireOp",EDGE,"E41.trimOffspring"),sQuery(id+"F0.wireOp",EDGE,"E42.trimOffspring"),sQuery(id+"F0.wireOp",EDGE,"E43.trimOffspring"),sQuery(id+"F0.wireOp",EDGE,"E44.trimOffspring"),sQuery(id+"F0.wireOp",EDGE,"E45.trimOffspring"),sQuery(id+"F0.wireOp",EDGE,"E46.trimOffspring")])],"isStart":false});
            var sketch = newSketch(context, id + "F7", { "sketchPlane" : qUnion([Q0])});
            skPoint(sketch, "E63", {"position": v(-0.08, 19.85) * mm});
            skPoint(sketch, "E64", {"position": v(1.47, 17.95) * mm});
            skPoint(sketch, "E65", {"position": v(0.2, 16.04) * mm});
            skPoint(sketch, "E66", {"position": v(-1.06, 14.14) * mm});
            skPoint(sketch, "E67", {"position": v(0.2, 12.23) * mm});
            skArc(sketch, "E68", {"start": v(1.34, 16.18) * mm, "mid": v(-0.98, 14.7) * mm, "end": v(0.2, 12.23) * mm});
            skArc(sketch, "E69", {"start": v(1.05, 16.68) * mm, "mid": v(1.35, 18.57) * mm, "end": v(-0.08, 19.85) * mm});
            skArc(sketch, "E70", {"start": v(1.34, 16.18) * mm, "mid": v(1.88, 18.7) * mm, "end": v(-0.05, 20.4) * mm});
            skArc(sketch, "E71", {"start": v(1.05, 16.68) * mm, "mid": v(-1.43, 14.86) * mm, "end": v(-0.35, 11.99) * mm});
            skPoint(sketch, "E72.second.point", {"position": v(-0.35, 11.99) * mm});
            skPoint(sketch, "E72.third.point", {"position": v(0.1, 11.43) * mm});
            skArc(sketch, "E73", {"start": v(-0.05, 20.4) * mm, "mid": v(-0.3, 20.14) * mm, "end": v(-0.08, 19.85) * mm});
            skPoint(sketch, "E73.second.point", {"position": v(-0.05, 20.4) * mm});
            skPoint(sketch, "E73.third.point", {"position": v(-0.05, 19.85) * mm});
            skCircle(sketch, "E74", {"center": v(1, 14.14) * mm, "radius": 1.73 * mm});
            skPoint(sketch, "E75.1.0", {"position": v(-9.97, 17.08) * mm});
            skPoint(sketch, "E75.1.1", {"position": v(-7.68, 16.2) * mm});
            skPoint(sketch, "E75.1.2", {"position": v(-7.83, 13.92) * mm});
            skPoint(sketch, "E75.1.3", {"position": v(-7.97, 11.64) * mm});
            skPoint(sketch, "E75.1.4", {"position": v(-5.91, 10.62) * mm});
            skArc(sketch, "E75.1.5", {"start": v(-6.91, 14.6) * mm, "mid": v(-8.18, 12.17) * mm, "end": v(-5.91, 10.62) * mm});
            skArc(sketch, "E75.1.6", {"start": v(-7.4, 14.9) * mm, "mid": v(-8.1, 16.69) * mm, "end": v(-9.97, 17.08) * mm});
            skArc(sketch, "E75.1.7", {"start": v(-6.91, 14.6) * mm, "mid": v(-7.7, 17.06) * mm, "end": v(-10.22, 17.57) * mm});
            skArc(sketch, "E75.1.8", {"start": v(-7.4, 14.9) * mm, "mid": v(-8.65, 12.08) * mm, "end": v(-6.27, 10.14) * mm});
            skArc(sketch, "E75.1.9", {"start": v(-6.27, 10.14) * mm, "mid": v(-5.52, 9.96) * mm, "end": v(-5.91, 10.62) * mm});
            skPoint(sketch, "E75.1.10", {"position": v(-6.27, 10.14) * mm});
            skPoint(sketch, "E75.1.11", {"position": v(-5.62, 9.87) * mm});
            skArc(sketch, "E75.1.12", {"start": v(-10.22, 17.57) * mm, "mid": v(-10.3, 17.22) * mm, "end": v(-9.97, 17.08) * mm});
            skPoint(sketch, "E75.1.13", {"position": v(-10.22, 17.57) * mm});
            skPoint(sketch, "E75.1.14", {"position": v(-9.94, 17.1) * mm});
            skCircle(sketch, "E75.1.15", {"center": v(-6.18, 12.67) * mm, "radius": 1.73 * mm});
            skPoint(sketch, "E75.2.0", {"position": v(-17.16, 9.73) * mm});
            skPoint(sketch, "E75.2.1", {"position": v(-14.73, 10.12) * mm});
            skPoint(sketch, "E75.2.2", {"position": v(-13.72, 8.06) * mm});
            skPoint(sketch, "E75.2.3", {"position": v(-12.7, 6.02) * mm});
            skPoint(sketch, "E75.2.4", {"position": v(-10.41, 6.17) * mm});
            skArc(sketch, "E75.2.5", {"start": v(-13.27, 9.12) * mm, "mid": v(-13.15, 6.37) * mm, "end": v(-10.41, 6.17) * mm});
            skArc(sketch, "E75.2.6", {"start": v(-13.84, 9.12) * mm, "mid": v(-15.33, 10.33) * mm, "end": v(-17.16, 9.73) * mm});
            skArc(sketch, "E75.2.7", {"start": v(-13.27, 9.12) * mm, "mid": v(-15.17, 10.85) * mm, "end": v(-17.61, 10.03) * mm});
            skArc(sketch, "E75.2.8", {"start": v(-13.84, 9.12) * mm, "mid": v(-13.51, 6.07) * mm, "end": v(-10.48, 5.57) * mm});
            skArc(sketch, "E75.2.9", {"start": v(-10.48, 5.57) * mm, "mid": v(-9.74, 5.8) * mm, "end": v(-10.41, 6.17) * mm});
            skPoint(sketch, "E75.2.10", {"position": v(-10.48, 5.57) * mm});
            skPoint(sketch, "E75.2.11", {"position": v(-9.78, 5.67) * mm});
            skArc(sketch, "E75.2.12", {"start": v(-17.61, 10.03) * mm, "mid": v(-17.51, 9.69) * mm, "end": v(-17.16, 9.73) * mm});
            skPoint(sketch, "E75.2.13", {"position": v(-17.61, 10.03) * mm});
            skPoint(sketch, "E75.2.14", {"position": v(-17.14, 9.76) * mm});
            skCircle(sketch, "E75.2.15", {"center": v(-11.67, 7.81) * mm, "radius": 1.73 * mm});
            skPoint(sketch, "E75.3.0", {"position": v(-19.7, -0.23) * mm});
            skPoint(sketch, "E75.3.1", {"position": v(-17.8, 1.32) * mm});
            skPoint(sketch, "E75.3.2", {"position": v(-15.9, 0.05) * mm});
            skPoint(sketch, "E75.3.3", {"position": v(-13.99, -1.2) * mm});
            skPoint(sketch, "E75.3.4", {"position": v(-12.08, 0.06) * mm});
            skArc(sketch, "E75.3.5", {"start": v(-16.03, 1.19) * mm, "mid": v(-14.56, -1.13) * mm, "end": v(-12.08, 0.06) * mm});
            skArc(sketch, "E75.3.6", {"start": v(-16.53, 0.9) * mm, "mid": v(-18.43, 1.2) * mm, "end": v(-19.7, -0.23) * mm});
            skArc(sketch, "E75.3.7", {"start": v(-16.03, 1.19) * mm, "mid": v(-18.55, 1.73) * mm, "end": v(-20.25, -0.2) * mm});
            skArc(sketch, "E75.3.8", {"start": v(-16.53, 0.9) * mm, "mid": v(-14.71, -1.58) * mm, "end": v(-11.84, -0.5) * mm});
            skArc(sketch, "E75.3.9", {"start": v(-11.84, -0.5) * mm, "mid": v(-11.31, 0.07) * mm, "end": v(-12.08, 0.06) * mm});
            skPoint(sketch, "E75.3.10", {"position": v(-11.84, -0.5) * mm});
            skPoint(sketch, "E75.3.11", {"position": v(-11.28, -0.06) * mm});
            skArc(sketch, "E75.3.12", {"start": v(-20.25, -0.2) * mm, "mid": v(-19.99, -0.44) * mm, "end": v(-19.7, -0.23) * mm});
            skPoint(sketch, "E75.3.13", {"position": v(-20.25, -0.2) * mm});
            skPoint(sketch, "E75.3.14", {"position": v(-19.7, -0.2) * mm});
            skCircle(sketch, "E75.3.15", {"center": v(-14, 0.86) * mm, "radius": 1.73 * mm});
            skPoint(sketch, "E75.4.0", {"position": v(-16.93, -10.12) * mm});
            skPoint(sketch, "E75.4.1", {"position": v(-16.05, -7.83) * mm});
            skPoint(sketch, "E75.4.2", {"position": v(-13.77, -7.98) * mm});
            skPoint(sketch, "E75.4.3", {"position": v(-11.49, -8.12) * mm});
            skPoint(sketch, "E75.4.4", {"position": v(-10.47, -6.06) * mm});
            skArc(sketch, "E75.4.5", {"start": v(-14.46, -7.06) * mm, "mid": v(-12.02, -8.33) * mm, "end": v(-10.47, -6.06) * mm});
            skArc(sketch, "E75.4.6", {"start": v(-14.75, -7.56) * mm, "mid": v(-16.54, -8.24) * mm, "end": v(-16.93, -10.12) * mm});
            skArc(sketch, "E75.4.7", {"start": v(-14.46, -7.06) * mm, "mid": v(-16.9, -7.85) * mm, "end": v(-17.42, -10.37) * mm});
            skArc(sketch, "E75.4.8", {"start": v(-14.75, -7.56) * mm, "mid": v(-11.93, -8.8) * mm, "end": v(-9.99, -6.42) * mm});
            skArc(sketch, "E75.4.9", {"start": v(-9.99, -6.42) * mm, "mid": v(-9.81, -5.67) * mm, "end": v(-10.47, -6.06) * mm});
            skPoint(sketch, "E75.4.10", {"position": v(-9.99, -6.42) * mm});
            skPoint(sketch, "E75.4.11", {"position": v(-9.72, -5.76) * mm});
            skArc(sketch, "E75.4.12", {"start": v(-17.42, -10.37) * mm, "mid": v(-17.07, -10.45) * mm, "end": v(-16.93, -10.12) * mm});
            skPoint(sketch, "E75.4.13", {"position": v(-17.42, -10.37) * mm});
            skPoint(sketch, "E75.4.14", {"position": v(-16.94, -10.1) * mm});
            skCircle(sketch, "E75.4.15", {"center": v(-12.52, -6.33) * mm, "radius": 1.73 * mm});
            skPoint(sketch, "E75.5.0", {"position": v(-9.58, -17.3) * mm});
            skPoint(sketch, "E75.5.1", {"position": v(-9.97, -14.88) * mm});
            skPoint(sketch, "E75.5.2", {"position": v(-7.92, -13.87) * mm});
            skPoint(sketch, "E75.5.3", {"position": v(-5.87, -12.85) * mm});
            skPoint(sketch, "E75.5.4", {"position": v(-6.02, -10.56) * mm});
            skArc(sketch, "E75.5.5", {"start": v(-8.97, -13.42) * mm, "mid": v(-6.23, -13.3) * mm, "end": v(-6.02, -10.56) * mm});
            skArc(sketch, "E75.5.6", {"start": v(-8.97, -14) * mm, "mid": v(-10.18, -15.48) * mm, "end": v(-9.58, -17.3) * mm});
            skArc(sketch, "E75.5.7", {"start": v(-8.97, -13.42) * mm, "mid": v(-10.7, -15.32) * mm, "end": v(-9.88, -17.76) * mm});
            skArc(sketch, "E75.5.8", {"start": v(-8.97, -14) * mm, "mid": v(-5.92, -13.66) * mm, "end": v(-5.42, -10.63) * mm});
            skArc(sketch, "E75.5.9", {"start": v(-5.42, -10.63) * mm, "mid": v(-5.64, -9.9) * mm, "end": v(-6.02, -10.56) * mm});
            skPoint(sketch, "E75.5.10", {"position": v(-5.42, -10.63) * mm});
            skPoint(sketch, "E75.5.11", {"position": v(-5.52, -9.93) * mm});
            skArc(sketch, "E75.5.12", {"start": v(-9.88, -17.76) * mm, "mid": v(-9.54, -17.66) * mm, "end": v(-9.58, -17.3) * mm});
            skPoint(sketch, "E75.5.13", {"position": v(-9.88, -17.76) * mm});
            skPoint(sketch, "E75.5.14", {"position": v(-9.6, -17.28) * mm});
            skCircle(sketch, "E75.5.15", {"center": v(-7.66, -11.82) * mm, "radius": 1.73 * mm});
            skPoint(sketch, "E75.6.0", {"position": v(0.38, -19.85) * mm});
            skPoint(sketch, "E75.6.1", {"position": v(-1.17, -17.95) * mm});
            skPoint(sketch, "E75.6.2", {"position": v(0.1, -16.04) * mm});
            skPoint(sketch, "E75.6.3", {"position": v(1.36, -14.14) * mm});
            skPoint(sketch, "E75.6.4", {"position": v(0.09, -12.23) * mm});
            skArc(sketch, "E75.6.5", {"start": v(-1.04, -16.18) * mm, "mid": v(1.28, -14.7) * mm, "end": v(0.09, -12.23) * mm});
            skArc(sketch, "E75.6.6", {"start": v(-0.75, -16.68) * mm, "mid": v(-1.06, -18.57) * mm, "end": v(0.38, -19.85) * mm});
            skArc(sketch, "E75.6.7", {"start": v(-1.04, -16.18) * mm, "mid": v(-1.59, -18.7) * mm, "end": v(0.35, -20.4) * mm});
            skArc(sketch, "E75.6.8", {"start": v(-0.75, -16.68) * mm, "mid": v(1.73, -14.86) * mm, "end": v(0.64, -11.99) * mm});
            skArc(sketch, "E75.6.9", {"start": v(0.64, -11.99) * mm, "mid": v(0.08, -11.46) * mm, "end": v(0.09, -12.23) * mm});
            skPoint(sketch, "E75.6.10", {"position": v(0.64, -11.99) * mm});
            skPoint(sketch, "E75.6.11", {"position": v(0.2, -11.43) * mm});
            skArc(sketch, "E75.6.12", {"start": v(0.35, -20.4) * mm, "mid": v(0.6, -20.14) * mm, "end": v(0.38, -19.85) * mm});
            skPoint(sketch, "E75.6.13", {"position": v(0.35, -20.4) * mm});
            skPoint(sketch, "E75.6.14", {"position": v(0.34, -19.85) * mm});
            skCircle(sketch, "E75.6.15", {"center": v(-0.7, -14.14) * mm, "radius": 1.73 * mm});
            skPoint(sketch, "E75.7.0", {"position": v(10.27, -17.08) * mm});
            skPoint(sketch, "E75.7.1", {"position": v(7.98, -16.2) * mm});
            skPoint(sketch, "E75.7.2", {"position": v(8.13, -13.92) * mm});
            skPoint(sketch, "E75.7.3", {"position": v(8.26, -11.64) * mm});
            skPoint(sketch, "E75.7.4", {"position": v(6.21, -10.62) * mm});
            skArc(sketch, "E75.7.5", {"start": v(7.21, -14.6) * mm, "mid": v(8.48, -12.17) * mm, "end": v(6.21, -10.62) * mm});
            skArc(sketch, "E75.7.6", {"start": v(7.7, -14.9) * mm, "mid": v(8.4, -16.69) * mm, "end": v(10.27, -17.08) * mm});
            skArc(sketch, "E75.7.7", {"start": v(7.21, -14.6) * mm, "mid": v(8, -17.06) * mm, "end": v(10.52, -17.57) * mm});
            skArc(sketch, "E75.7.8", {"start": v(7.7, -14.9) * mm, "mid": v(8.95, -12.08) * mm, "end": v(6.57, -10.14) * mm});
            skArc(sketch, "E75.7.9", {"start": v(6.57, -10.14) * mm, "mid": v(5.82, -9.96) * mm, "end": v(6.21, -10.62) * mm});
            skPoint(sketch, "E75.7.10", {"position": v(6.57, -10.14) * mm});
            skPoint(sketch, "E75.7.11", {"position": v(5.91, -9.87) * mm});
            skArc(sketch, "E75.7.12", {"start": v(10.52, -17.57) * mm, "mid": v(10.6, -17.22) * mm, "end": v(10.27, -17.08) * mm});
            skPoint(sketch, "E75.7.13", {"position": v(10.52, -17.57) * mm});
            skPoint(sketch, "E75.7.14", {"position": v(10.24, -17.1) * mm});
            skCircle(sketch, "E75.7.15", {"center": v(6.48, -12.67) * mm, "radius": 1.73 * mm});
            skPoint(sketch, "E75.8.0", {"position": v(17.45, -9.73) * mm});
            skPoint(sketch, "E75.8.1", {"position": v(15.03, -10.12) * mm});
            skPoint(sketch, "E75.8.2", {"position": v(14.02, -8.06) * mm});
            skPoint(sketch, "E75.8.3", {"position": v(13, -6.02) * mm});
            skPoint(sketch, "E75.8.4", {"position": v(10.71, -6.17) * mm});
            skArc(sketch, "E75.8.5", {"start": v(13.57, -9.12) * mm, "mid": v(13.45, -6.37) * mm, "end": v(10.71, -6.17) * mm});
            skArc(sketch, "E75.8.6", {"start": v(14.14, -9.12) * mm, "mid": v(15.63, -10.33) * mm, "end": v(17.45, -9.73) * mm});
            skArc(sketch, "E75.8.7", {"start": v(13.57, -9.12) * mm, "mid": v(15.47, -10.85) * mm, "end": v(17.91, -10.03) * mm});
            skArc(sketch, "E75.8.8", {"start": v(14.14, -9.12) * mm, "mid": v(13.8, -6.07) * mm, "end": v(10.78, -5.57) * mm});
            skArc(sketch, "E75.8.9", {"start": v(10.78, -5.57) * mm, "mid": v(10.04, -5.8) * mm, "end": v(10.71, -6.17) * mm});
            skPoint(sketch, "E75.8.10", {"position": v(10.78, -5.57) * mm});
            skPoint(sketch, "E75.8.11", {"position": v(10.08, -5.67) * mm});
            skArc(sketch, "E75.8.12", {"start": v(17.91, -10.03) * mm, "mid": v(17.8, -9.69) * mm, "end": v(17.45, -9.73) * mm});
            skPoint(sketch, "E75.8.13", {"position": v(17.91, -10.03) * mm});
            skPoint(sketch, "E75.8.14", {"position": v(17.43, -9.76) * mm});
            skCircle(sketch, "E75.8.15", {"center": v(11.96, -7.81) * mm, "radius": 1.73 * mm});
            skPoint(sketch, "E75.9.0", {"position": v(20, 0.23) * mm});
            skPoint(sketch, "E75.9.1", {"position": v(18.1, -1.32) * mm});
            skPoint(sketch, "E75.9.2", {"position": v(16.2, -0.05) * mm});
            skPoint(sketch, "E75.9.3", {"position": v(14.29, 1.2) * mm});
            skPoint(sketch, "E75.9.4", {"position": v(12.38, -0.06) * mm});
            skArc(sketch, "E75.9.5", {"start": v(16.33, -1.19) * mm, "mid": v(14.85, 1.13) * mm, "end": v(12.38, -0.06) * mm});
            skArc(sketch, "E75.9.6", {"start": v(16.83, -0.9) * mm, "mid": v(18.72, -1.2) * mm, "end": v(20, 0.23) * mm});
            skArc(sketch, "E75.9.7", {"start": v(16.33, -1.19) * mm, "mid": v(18.84, -1.73) * mm, "end": v(20.55, 0.2) * mm});
            skArc(sketch, "E75.9.8", {"start": v(16.83, -0.9) * mm, "mid": v(15.01, 1.58) * mm, "end": v(12.14, 0.5) * mm});
            skArc(sketch, "E75.9.9", {"start": v(12.14, 0.5) * mm, "mid": v(11.61, -0.07) * mm, "end": v(12.38, -0.06) * mm});
            skPoint(sketch, "E75.9.10", {"position": v(12.14, 0.5) * mm});
            skPoint(sketch, "E75.9.11", {"position": v(11.58, 0.06) * mm});
            skArc(sketch, "E75.9.12", {"start": v(20.55, 0.2) * mm, "mid": v(20.29, 0.44) * mm, "end": v(20, 0.23) * mm});
            skPoint(sketch, "E75.9.13", {"position": v(20.55, 0.2) * mm});
            skPoint(sketch, "E75.9.14", {"position": v(20, 0.2) * mm});
            skCircle(sketch, "E75.9.15", {"center": v(14.29, -0.86) * mm, "radius": 1.73 * mm});
            skPoint(sketch, "E75.10.0", {"position": v(17.23, 10.12) * mm});
            skPoint(sketch, "E75.10.1", {"position": v(16.35, 7.83) * mm});
            skPoint(sketch, "E75.10.2", {"position": v(14.07, 7.98) * mm});
            skPoint(sketch, "E75.10.3", {"position": v(11.79, 8.12) * mm});
            skPoint(sketch, "E75.10.4", {"position": v(10.77, 6.06) * mm});
            skArc(sketch, "E75.10.5", {"start": v(14.75, 7.06) * mm, "mid": v(12.32, 8.33) * mm, "end": v(10.77, 6.06) * mm});
            skArc(sketch, "E75.10.6", {"start": v(15.04, 7.56) * mm, "mid": v(16.84, 8.24) * mm, "end": v(17.23, 10.12) * mm});
            skArc(sketch, "E75.10.7", {"start": v(14.75, 7.06) * mm, "mid": v(17.2, 7.85) * mm, "end": v(17.71, 10.37) * mm});
            skArc(sketch, "E75.10.8", {"start": v(15.04, 7.56) * mm, "mid": v(12.23, 8.8) * mm, "end": v(10.28, 6.42) * mm});
            skArc(sketch, "E75.10.9", {"start": v(10.28, 6.42) * mm, "mid": v(10.1, 5.67) * mm, "end": v(10.77, 6.06) * mm});
            skPoint(sketch, "E75.10.10", {"position": v(10.28, 6.42) * mm});
            skPoint(sketch, "E75.10.11", {"position": v(10.02, 5.76) * mm});
            skArc(sketch, "E75.10.12", {"start": v(17.71, 10.37) * mm, "mid": v(17.37, 10.45) * mm, "end": v(17.23, 10.12) * mm});
            skPoint(sketch, "E75.10.13", {"position": v(17.71, 10.37) * mm});
            skPoint(sketch, "E75.10.14", {"position": v(17.24, 10.1) * mm});
            skCircle(sketch, "E75.10.15", {"center": v(12.82, 6.33) * mm, "radius": 1.73 * mm});
            skPoint(sketch, "E75.11.0", {"position": v(9.88, 17.3) * mm});
            skPoint(sketch, "E75.11.1", {"position": v(10.27, 14.88) * mm});
            skPoint(sketch, "E75.11.2", {"position": v(8.21, 13.87) * mm});
            skPoint(sketch, "E75.11.3", {"position": v(6.17, 12.85) * mm});
            skPoint(sketch, "E75.11.4", {"position": v(6.32, 10.56) * mm});
            skArc(sketch, "E75.11.5", {"start": v(9.27, 13.42) * mm, "mid": v(6.52, 13.3) * mm, "end": v(6.32, 10.56) * mm});
            skArc(sketch, "E75.11.6", {"start": v(9.27, 14) * mm, "mid": v(10.48, 15.48) * mm, "end": v(9.88, 17.3) * mm});
            skArc(sketch, "E75.11.7", {"start": v(9.27, 13.42) * mm, "mid": v(11, 15.32) * mm, "end": v(10.18, 17.76) * mm});
            skArc(sketch, "E75.11.8", {"start": v(9.27, 14) * mm, "mid": v(6.21, 13.66) * mm, "end": v(5.72, 10.63) * mm});
            skArc(sketch, "E75.11.9", {"start": v(5.72, 10.63) * mm, "mid": v(5.94, 9.9) * mm, "end": v(6.32, 10.56) * mm});
            skPoint(sketch, "E75.11.10", {"position": v(5.72, 10.63) * mm});
            skPoint(sketch, "E75.11.11", {"position": v(5.81, 9.93) * mm});
            skArc(sketch, "E75.11.12", {"start": v(10.18, 17.76) * mm, "mid": v(9.83, 17.66) * mm, "end": v(9.88, 17.3) * mm});
            skPoint(sketch, "E75.11.13", {"position": v(10.18, 17.76) * mm});
            skPoint(sketch, "E75.11.14", {"position": v(9.9, 17.28) * mm});
            skCircle(sketch, "E75.11.15", {"center": v(7.96, 11.82) * mm, "radius": 1.73 * mm});
            skPoint(sketch, "E75.center", {"position": v(0.15, 0) * mm});
            skArc(sketch, "E76", {"start": v(-0.35, 11.99) * mm, "mid": v(0.22, 11.46) * mm, "end": v(0.2, 12.23) * mm});
            skArc(sketch, "E77", {"start": v(0, 9.22) * mm, "mid": v(-0.64, 8.58) * mm, "end": v(0, 7.94) * mm});
            skArc(sketch, "E78.1.0", {"start": v(-7.94, 0) * mm, "mid": v(-8.58, 0.64) * mm, "end": v(-9.22, 0) * mm});
            skArc(sketch, "E78.2.0", {"start": v(0, -9.22) * mm, "mid": v(0.64, -8.58) * mm, "end": v(0, -7.94) * mm});
            skArc(sketch, "E78.3.0", {"start": v(7.94, 0) * mm, "mid": v(8.58, -0.64) * mm, "end": v(9.22, 0) * mm});
            skPoint(sketch, "E78.center", {"position": v(0, 0) * mm});
            skArc(sketch, "E79", {"start": v(-9.22, 0) * mm, "mid": v(-6.52, -6.52) * mm, "end": v(0, -9.22) * mm});
            skArc(sketch, "E80", {"start": v(-7.94, 0) * mm, "mid": v(-5.61, -5.61) * mm, "end": v(0, -7.94) * mm});
            skArc(sketch, "E81.trimOffspring", {"start": v(9.22, 0) * mm, "mid": v(6.52, 6.52) * mm, "end": v(0, 9.22) * mm});
            skArc(sketch, "E82.trimOffspring", {"start": v(7.94, 0) * mm, "mid": v(5.61, 5.61) * mm, "end": v(0, 7.94) * mm});
            skSolve(sketch);
        }
        {
            var Q0;
            Q0 = qSketchRegion(id + "F7", true);
            extrude(context, id + "F8", {"entities" : qUnion([Q0]), "operationType" : NewBodyOperationType.REMOVE, "oppositeDirection" : true, "depth" : 25.4 * mm});
        }
        {
            var Q0;
            Q0=makeQuery(id+"F8.boolean.opBoolean","COPY",FACE,{"derivedFrom":makeQuery(id+"F8.opExtrude","SWEPT_FACE",FACE,{"disambiguationData":[OSD([sQuery(id+"F7.wireOp",EDGE,"E75.1.15")])]})});
            var Q1;
            Q1=makeQuery(id+"F8.boolean.opBoolean","COPY",FACE,{"derivedFrom":makeQuery(id+"F8.opExtrude","SWEPT_FACE",FACE,{"disambiguationData":[OSD([sQuery(id+"F7.wireOp",EDGE,"E75.1.6")])]})});
            var Q2;
            Q2=makeQuery(id+"F8.boolean.opBoolean","COPY",FACE,{"derivedFrom":makeQuery(id+"F8.opExtrude","SWEPT_FACE",FACE,{"disambiguationData":[OSD([sQuery(id+"F7.wireOp",EDGE,"E75.1.7")])]})});
            var Q3;
            Q3=makeQuery(id+"F8.boolean.opBoolean","COPY",FACE,{"derivedFrom":makeQuery(id+"F8.opExtrude","SWEPT_FACE",FACE,{"disambiguationData":[OSD([sQuery(id+"F7.wireOp",EDGE,"E75.1.8")])]})});
            var Q4;
            Q4=makeQuery(id+"F8.boolean.opBoolean","COPY",FACE,{"derivedFrom":makeQuery(id+"F8.opExtrude","SWEPT_FACE",FACE,{"disambiguationData":[OSD([sQuery(id+"F7.wireOp",EDGE,"E69")])]})});
            var Q5;
            Q5=makeQuery(id+"F8.boolean.opBoolean","COPY",FACE,{"derivedFrom":makeQuery(id+"F8.opExtrude","SWEPT_FACE",FACE,{"disambiguationData":[OSD([sQuery(id+"F7.wireOp",EDGE,"E73")])]})});
            var Q6;
            Q6=makeQuery(id+"F8.boolean.opBoolean","COPY",FACE,{"derivedFrom":makeQuery(id+"F8.opExtrude","SWEPT_FACE",FACE,{"disambiguationData":[OSD([sQuery(id+"F7.wireOp",EDGE,"E71")])]})});
            var Q7;
            Q7=makeQuery(id+"F8.boolean.opBoolean","COPY",FACE,{"derivedFrom":makeQuery(id+"F8.opExtrude","SWEPT_FACE",FACE,{"disambiguationData":[OSD([sQuery(id+"F7.wireOp",EDGE,"E68")])]})});
            var Q8;
            Q8=makeQuery(id+"F8.boolean.opBoolean","COPY",FACE,{"derivedFrom":makeQuery(id+"F8.opExtrude","SWEPT_FACE",FACE,{"disambiguationData":[OSD([sQuery(id+"F7.wireOp",EDGE,"E74")])]})});
            var Q9;
            Q9=makeQuery(id+"F8.boolean.opBoolean","COPY",FACE,{"derivedFrom":makeQuery(id+"F8.opExtrude","SWEPT_FACE",FACE,{"disambiguationData":[OSD([sQuery(id+"F7.wireOp",EDGE,"E75.11.6")])]})});
            var Q10;
            Q10=makeQuery(id+"F8.boolean.opBoolean","COPY",FACE,{"derivedFrom":makeQuery(id+"F8.opExtrude","SWEPT_FACE",FACE,{"disambiguationData":[OSD([sQuery(id+"F7.wireOp",EDGE,"E75.11.8")])]})});
            var Q11;
            Q11=makeQuery(id+"F8.boolean.opBoolean","COPY",FACE,{"derivedFrom":makeQuery(id+"F8.opExtrude","SWEPT_FACE",FACE,{"disambiguationData":[OSD([sQuery(id+"F7.wireOp",EDGE,"E75.11.9")])]})});
            var Q12;
            Q12=makeQuery(id+"F8.boolean.opBoolean","COPY",FACE,{"derivedFrom":makeQuery(id+"F8.opExtrude","SWEPT_FACE",FACE,{"disambiguationData":[OSD([sQuery(id+"F7.wireOp",EDGE,"E75.11.15")])]})});
            var Q13;
            Q13=makeQuery(id+"F8.boolean.opBoolean","COPY",FACE,{"derivedFrom":makeQuery(id+"F8.opExtrude","SWEPT_FACE",FACE,{"disambiguationData":[OSD([sQuery(id+"F7.wireOp",EDGE,"E75.11.7")])]})});
            var Q14;
            Q14=makeQuery(id+"F8.boolean.opBoolean","COPY",FACE,{"derivedFrom":makeQuery(id+"F8.opExtrude","SWEPT_FACE",FACE,{"disambiguationData":[OSD([sQuery(id+"F7.wireOp",EDGE,"E75.10.8")])]})});
            var Q15;
            Q15=makeQuery(id+"F8.boolean.opBoolean","COPY",FACE,{"derivedFrom":makeQuery(id+"F8.opExtrude","SWEPT_FACE",FACE,{"disambiguationData":[OSD([sQuery(id+"F7.wireOp",EDGE,"E75.10.6")])]})});
            var Q16;
            Q16=makeQuery(id+"F8.boolean.opBoolean","COPY",FACE,{"derivedFrom":makeQuery(id+"F8.opExtrude","SWEPT_FACE",FACE,{"disambiguationData":[OSD([sQuery(id+"F7.wireOp",EDGE,"E75.10.7")])]})});
            var Q17;
            Q17=makeQuery(id+"F8.boolean.opBoolean","COPY",FACE,{"derivedFrom":makeQuery(id+"F8.opExtrude","SWEPT_FACE",FACE,{"disambiguationData":[OSD([sQuery(id+"F7.wireOp",EDGE,"E75.10.15")])]})});
            var Q18;
            Q18=makeQuery(id+"F8.boolean.opBoolean","COPY",FACE,{"derivedFrom":makeQuery(id+"F8.opExtrude","SWEPT_FACE",FACE,{"disambiguationData":[OSD([sQuery(id+"F7.wireOp",EDGE,"E75.9.8")])]})});
            var Q19;
            Q19=makeQuery(id+"F8.boolean.opBoolean","COPY",FACE,{"derivedFrom":makeQuery(id+"F8.opExtrude","SWEPT_FACE",FACE,{"disambiguationData":[OSD([sQuery(id+"F7.wireOp",EDGE,"E75.9.6")])]})});
            var Q20;
            Q20=makeQuery(id+"F8.boolean.opBoolean","COPY",FACE,{"derivedFrom":makeQuery(id+"F8.opExtrude","SWEPT_FACE",FACE,{"disambiguationData":[OSD([sQuery(id+"F7.wireOp",EDGE,"E75.9.7")])]})});
            var Q21;
            Q21=makeQuery(id+"F8.boolean.opBoolean","COPY",FACE,{"derivedFrom":makeQuery(id+"F8.opExtrude","SWEPT_FACE",FACE,{"disambiguationData":[OSD([sQuery(id+"F7.wireOp",EDGE,"E75.9.15")])]})});
            var Q22;
            Q22=makeQuery(id+"F8.boolean.opBoolean","COPY",FACE,{"derivedFrom":makeQuery(id+"F8.opExtrude","SWEPT_FACE",FACE,{"disambiguationData":[OSD([sQuery(id+"F7.wireOp",EDGE,"E75.8.15")])]})});
            var Q23;
            Q23=makeQuery(id+"F8.boolean.opBoolean","COPY",FACE,{"derivedFrom":makeQuery(id+"F8.opExtrude","SWEPT_FACE",FACE,{"disambiguationData":[OSD([sQuery(id+"F7.wireOp",EDGE,"E75.8.8")])]})});
            var Q24;
            Q24=makeQuery(id+"F8.boolean.opBoolean","COPY",FACE,{"derivedFrom":makeQuery(id+"F8.opExtrude","SWEPT_FACE",FACE,{"disambiguationData":[OSD([sQuery(id+"F7.wireOp",EDGE,"E75.8.6")])]})});
            var Q25;
            Q25=makeQuery(id+"F8.boolean.opBoolean","COPY",FACE,{"derivedFrom":makeQuery(id+"F8.opExtrude","SWEPT_FACE",FACE,{"disambiguationData":[OSD([sQuery(id+"F7.wireOp",EDGE,"E75.8.7")])]})});
            var Q26;
            Q26=makeQuery(id+"F8.boolean.opBoolean","COPY",FACE,{"derivedFrom":makeQuery(id+"F8.opExtrude","SWEPT_FACE",FACE,{"disambiguationData":[OSD([sQuery(id+"F7.wireOp",EDGE,"E75.7.15")])]})});
            var Q27;
            Q27=makeQuery(id+"F8.boolean.opBoolean","COPY",FACE,{"derivedFrom":makeQuery(id+"F8.opExtrude","SWEPT_FACE",FACE,{"disambiguationData":[OSD([sQuery(id+"F7.wireOp",EDGE,"E75.7.7")])]})});
            var Q28;
            Q28=makeQuery(id+"F8.boolean.opBoolean","COPY",FACE,{"derivedFrom":makeQuery(id+"F8.opExtrude","SWEPT_FACE",FACE,{"disambiguationData":[OSD([sQuery(id+"F7.wireOp",EDGE,"E75.7.8")])]})});
            var Q29;
            Q29=makeQuery(id+"F8.boolean.opBoolean","COPY",FACE,{"derivedFrom":makeQuery(id+"F8.opExtrude","SWEPT_FACE",FACE,{"disambiguationData":[OSD([sQuery(id+"F7.wireOp",EDGE,"E75.6.15")])]})});
            var Q30;
            Q30=makeQuery(id+"F8.boolean.opBoolean","COPY",FACE,{"derivedFrom":makeQuery(id+"F8.opExtrude","SWEPT_FACE",FACE,{"disambiguationData":[OSD([sQuery(id+"F7.wireOp",EDGE,"E75.6.8")])]})});
            var Q31;
            Q31=makeQuery(id+"F8.boolean.opBoolean","COPY",FACE,{"derivedFrom":makeQuery(id+"F8.opExtrude","SWEPT_FACE",FACE,{"disambiguationData":[OSD([sQuery(id+"F7.wireOp",EDGE,"E75.6.7")])]})});
            var Q32;
            Q32=makeQuery(id+"F8.boolean.opBoolean","COPY",FACE,{"derivedFrom":makeQuery(id+"F8.opExtrude","SWEPT_FACE",FACE,{"disambiguationData":[OSD([sQuery(id+"F7.wireOp",EDGE,"E75.5.15")])]})});
            var Q33;
            Q33=makeQuery(id+"F8.boolean.opBoolean","COPY",FACE,{"derivedFrom":makeQuery(id+"F8.opExtrude","SWEPT_FACE",FACE,{"disambiguationData":[OSD([sQuery(id+"F7.wireOp",EDGE,"E75.5.7")])]})});
            var Q34;
            Q34=makeQuery(id+"F8.boolean.opBoolean","COPY",FACE,{"derivedFrom":makeQuery(id+"F8.opExtrude","SWEPT_FACE",FACE,{"disambiguationData":[OSD([sQuery(id+"F7.wireOp",EDGE,"E75.5.8")])]})});
            var Q35;
            Q35=makeQuery(id+"F8.boolean.opBoolean","COPY",FACE,{"derivedFrom":makeQuery(id+"F8.opExtrude","SWEPT_FACE",FACE,{"disambiguationData":[OSD([sQuery(id+"F7.wireOp",EDGE,"E75.4.15")])]})});
            var Q36;
            Q36=makeQuery(id+"F8.boolean.opBoolean","COPY",FACE,{"derivedFrom":makeQuery(id+"F8.opExtrude","SWEPT_FACE",FACE,{"disambiguationData":[OSD([sQuery(id+"F7.wireOp",EDGE,"E75.4.8")])]})});
            var Q37;
            Q37=makeQuery(id+"F8.boolean.opBoolean","COPY",FACE,{"derivedFrom":makeQuery(id+"F8.opExtrude","SWEPT_FACE",FACE,{"disambiguationData":[OSD([sQuery(id+"F7.wireOp",EDGE,"E75.4.7")])]})});
            var Q38;
            Q38=makeQuery(id+"F8.boolean.opBoolean","COPY",FACE,{"derivedFrom":makeQuery(id+"F8.opExtrude","SWEPT_FACE",FACE,{"disambiguationData":[OSD([sQuery(id+"F7.wireOp",EDGE,"E75.3.15")])]})});
            var Q39;
            Q39=makeQuery(id+"F8.boolean.opBoolean","COPY",FACE,{"derivedFrom":makeQuery(id+"F8.opExtrude","SWEPT_FACE",FACE,{"disambiguationData":[OSD([sQuery(id+"F7.wireOp",EDGE,"E75.3.8")])]})});
            var Q40;
            Q40=makeQuery(id+"F8.boolean.opBoolean","COPY",FACE,{"derivedFrom":makeQuery(id+"F8.opExtrude","SWEPT_FACE",FACE,{"disambiguationData":[OSD([sQuery(id+"F7.wireOp",EDGE,"E75.3.7")])]})});
            var Q41;
            Q41=makeQuery(id+"F8.boolean.opBoolean","COPY",FACE,{"derivedFrom":makeQuery(id+"F8.opExtrude","SWEPT_FACE",FACE,{"disambiguationData":[OSD([sQuery(id+"F7.wireOp",EDGE,"E75.2.15")])]})});
            var Q42;
            Q42=makeQuery(id+"F8.boolean.opBoolean","COPY",FACE,{"derivedFrom":makeQuery(id+"F8.opExtrude","SWEPT_FACE",FACE,{"disambiguationData":[OSD([sQuery(id+"F7.wireOp",EDGE,"E75.2.7")])]})});
            var Q43;
            Q43=makeQuery(id+"F8.boolean.opBoolean","COPY",FACE,{"derivedFrom":makeQuery(id+"F8.opExtrude","SWEPT_FACE",FACE,{"disambiguationData":[OSD([sQuery(id+"F7.wireOp",EDGE,"E75.2.8")])]})});
            var Q44;
            Q44=makeQuery(id+"F8.boolean.opBoolean","COPY",FACE,{"derivedFrom":makeQuery(id+"F8.opExtrude","SWEPT_FACE",FACE,{"disambiguationData":[OSD([sQuery(id+"F7.wireOp",EDGE,"E82.trimOffspring")])]})});
            var Q45;
            Q45=makeQuery(id+"F8.boolean.opBoolean","COPY",FACE,{"derivedFrom":makeQuery(id+"F8.opExtrude","SWEPT_FACE",FACE,{"disambiguationData":[OSD([sQuery(id+"F7.wireOp",EDGE,"E79")])]})});
            var Q46;
            Q46=makeQuery(id+"F6.hole-3.boolean.opBoolean","COPY",FACE,{"derivedFrom":makeQuery(id+"F6.hole-3.opRevolve","SWEPT_FACE",FACE,{"disambiguationData":[OSD([sQuery(id+"F6.hole-3.sketch.wireOp",EDGE,"core_line_2")])]})});
            var Q47;
            Q47=makeQuery(id+"F6.hole-0.boolean.opBoolean","COPY",FACE,{"derivedFrom":makeQuery(id+"F6.hole-0.opRevolve","SWEPT_FACE",FACE,{"disambiguationData":[OSD([sQuery(id+"F6.hole-0.sketch.wireOp",EDGE,"core_line_2")])]})});
            var Q48;
            Q48=makeQuery(id+"F6.hole-1.boolean.opBoolean","COPY",FACE,{"derivedFrom":makeQuery(id+"F6.hole-1.opRevolve","SWEPT_FACE",FACE,{"disambiguationData":[OSD([sQuery(id+"F6.hole-1.sketch.wireOp",EDGE,"core_line_2")])]})});
            var Q49;
            Q49=makeQuery(id+"F6.hole-2.boolean.opBoolean","COPY",FACE,{"derivedFrom":makeQuery(id+"F6.hole-2.opRevolve","SWEPT_FACE",FACE,{"disambiguationData":[OSD([sQuery(id+"F6.hole-2.sketch.wireOp",EDGE,"core_line_2")])]})});
            var Q50;
            Q50=makeQuery(id+"F5.hole-0.boolean.opBoolean","COPY",FACE,{"derivedFrom":makeQuery(id+"F5.hole-0.opRevolve","SWEPT_FACE",FACE,{"disambiguationData":[OSD([sQuery(id+"F5.hole-0.sketch.wireOp",EDGE,"core_line_2")])]})});
            chamfer(context, id + "F9", {"entities" : qUnion([Q0, Q1, Q2, Q3, Q4, Q5, Q6, Q7, Q8, Q9, Q10, Q11, Q12, Q13, Q14, Q15, Q16, Q17, Q18, Q19, Q20, Q21, Q22, Q23, Q24, Q25, Q26, Q27, Q28, Q29, Q30, Q31, Q32, Q33, Q34, Q35, Q36, Q37, Q38, Q39, Q40, Q41, Q42, Q43, Q44, Q45, Q46, Q47, Q48, Q49, Q50]), "width" : 0.25 * mm, "tangentPropagation" : true});
        }
    });
